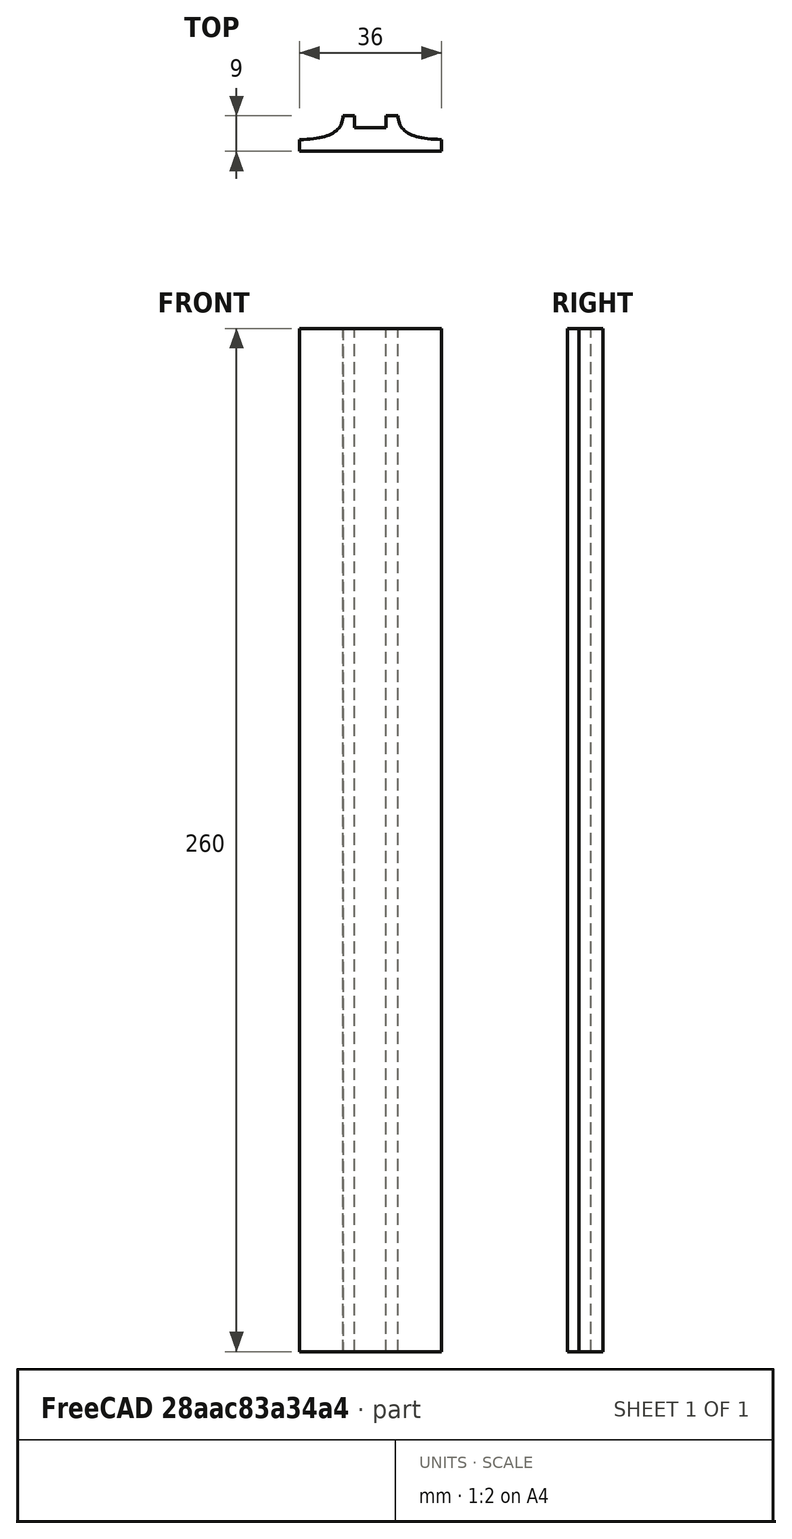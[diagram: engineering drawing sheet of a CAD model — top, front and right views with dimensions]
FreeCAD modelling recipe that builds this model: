
FCSTD DOCUMENT  (FreeCAD 0.19R0.19.2)
Label: laptopStand302.FCStd
License: All rights reserved
LicenseURL: http://en.wikipedia.org/wiki/All_rights_reserved
objects: Sketcher::SketchObject×12, Part::Extrusion×1
note: 13 computed .brp shape members not serialized (recipe doc carries the construction recipe); baked Part::Feature solids carry a one-line shape summary decoded from their .brp

FEATURE [Sketcher::SketchObject] Sketch001  label="legTop"
  FullyConstrained = true
  MapMode = 4
  Placement = pos=(0,0,0) rot=(0.57735,0.57735,0.57735;2.0944rad)
  sketch-geometry (41):
    g0: BSplineCurve PolesCount=3 KnotsCount=2 Degree=2 IsPeriodic=0
    g1: ArcOfCircle CenterX=73.1223 CenterY=-32.291 CenterZ=0 NormalX=0 NormalY=0 NormalZ=1 AngleXU=0 Radius=13 StartAngle=5.92268 EndAngle=9.06428
    g2: ArcOfCircle CenterX=66.7816 CenterY=-49.1439 CenterZ=0 NormalX=0 NormalY=0 NormalZ=1 AngleXU=0 Radius=13 StartAngle=2.78068 EndAngle=5.92131
    g3-g6: Circle x4 (B-spline internal-alignment scaffolding for g7; pole/knot coordinates omitted)
    g7: BSplineCurve PolesCount=4 KnotsCount=2 Degree=3 IsPeriodic=0
    g8: GeomPoint X=28.8094 Y=-19.0875 Z=0
    g9: GeomPoint X=47.0443 Y=-50.4712 Z=0
    g10: Circle CenterX=53.5586 CenterY=-23.2695 CenterZ=0 NormalX=0 NormalY=0 NormalZ=1 AngleXU=0 Radius=3.24518
    g11: LineSegment StartX=17.2232 StartY=-16.0875 StartZ=0 EndX=17.2232 EndY=-19.0875 EndZ=0
    g12: ArcOfCircle CenterX=17.2475 CenterY=-181.166 CenterZ=0 NormalX=0 NormalY=0 NormalZ=1 AngleXU=0 Radius=13 StartAngle=5.92268 EndAngle=7.49361
    g13: ArcOfCircle CenterX=29.5716 CenterY=-148.408 CenterZ=0 NormalX=0 NormalY=0 NormalZ=1 AngleXU=0 Radius=13 StartAngle=4.35228 EndAngle=5.92131
    g14: ArcOfCircle CenterX=35.8967 CenterY=-131.555 CenterZ=0 NormalX=0 NormalY=0 NormalZ=1 AngleXU=0 Radius=13 StartAngle=5.92268 EndAngle=7.49902
    g15: ArcOfCircle CenterX=48.1805 CenterY=-98.7782 CenterZ=0 NormalX=0 NormalY=0 NormalZ=1 AngleXU=0 Radius=13 StartAngle=4.34921 EndAngle=5.92131
    g16: ArcOfCircle CenterX=54.5183 CenterY=-81.9247 CenterZ=0 NormalX=0 NormalY=0 NormalZ=1 AngleXU=0 Radius=13 StartAngle=5.92268 EndAngle=8.70432
    g17: ArcOfCircle CenterX=20.184 CenterY=-217.506 CenterZ=0 NormalX=0 NormalY=0 NormalZ=1 AngleXU=0 Radius=3.81084 StartAngle=1.88136 EndAngle=6.80465
    g18: ArcOfCircle CenterX=36.3663 CenterY=-113.042 CenterZ=0 NormalX=0 NormalY=0 NormalZ=1 AngleXU=0 Radius=3.60555 StartAngle=0.230024 EndAngle=5.3372
    g19: ArcOfCircle CenterX=17.7945 CenterY=-162.686 CenterZ=0 NormalX=0 NormalY=0 NormalZ=1 AngleXU=0 Radius=3.60555 StartAngle=0.230024 EndAngle=5.3372
    g20: ArcOfCircle CenterX=49.8795 CenterY=-62.6074 CenterZ=0 NormalX=0 NormalY=0 NormalZ=1 AngleXU=0 Radius=3.84187 StartAngle=4.46973 EndAngle=9.40343
    g21: LineSegment StartX=48.9563 StartY=-66.3367 StartZ=0 EndX=44.7488 EndY=-73.3482 EndZ=0
    g22: LineSegment StartX=41.085 StartY=-66.3176 StartZ=0 EndX=46.0385 EndY=-62.5254 EndZ=0
    g23: LineSegment StartX=47.0443 StartY=-50.4712 StartZ=0 EndX=41.085 EndY=-66.3176 EndZ=0
    g24: LineSegment StartX=17.2232 StartY=-16.0875 StartZ=0 EndX=117.223 EndY=-16.0875 EndZ=0
    g25: LineSegment StartX=28.8094 StartY=-19.0875 StartZ=0 EndX=17.2232 EndY=-19.0875 EndZ=0
    g26: LineSegment StartX=117.223 StartY=-16.0875 StartZ=0 EndX=117.223 EndY=-19.0875 EndZ=0
    g27: LineSegment StartX=85.2866 StartY=-36.8766 StartZ=0 EndX=78.9396 EndY=-53.7463 EndZ=0
    g28: LineSegment StartX=60.9579 StartY=-27.7053 StartZ=0 EndX=54.6191 EndY=-44.5532 EndZ=0
    g29: LineSegment StartX=23.4884 StartY=-215.608 StartZ=0 EndX=94.6579 EndY=-26.1359 EndZ=0
    g30: LineSegment StartX=19.0195 StartY=-213.878 StartZ=0 EndX=29.4118 EndY=-185.752 EndZ=0
    g31: LineSegment StartX=22.7134 StartY=-166.661 StartZ=0 EndX=21.8316 EndY=-169.001 EndZ=0
    g32: LineSegment StartX=19.9036 StartY=-165.61 StartZ=0 EndX=22.7134 EndY=-166.661 EndZ=0
    g33: LineSegment StartX=21.3051 StartY=-161.864 StartZ=0 EndX=24.1149 EndY=-162.915 EndZ=0
    g34: LineSegment StartX=24.1149 StartY=-162.915 StartZ=0 EndX=24.9906 EndY=-160.574 EndZ=0
    g35: LineSegment StartX=41.7296 StartY=-153.01 StartZ=0 EndX=48.061 EndY=-136.14 EndZ=0
    g36: LineSegment StartX=41.2852 StartY=-117.017 StartZ=0 EndX=40.4148 EndY=-119.365 EndZ=0
    g37: LineSegment StartX=38.4753 StartY=-115.966 StartZ=0 EndX=41.2852 EndY=-117.017 EndZ=0
    g38: LineSegment StartX=39.8769 StartY=-112.22 StartZ=0 EndX=42.6867 EndY=-113.271 EndZ=0
    g39: LineSegment StartX=42.6867 StartY=-113.271 StartZ=0 EndX=43.5622 EndY=-110.93 EndZ=0
    g40: LineSegment StartX=66.6827 StartY=-86.5104 StartZ=0 EndX=60.3386 EndY=-103.381 EndZ=0
  constraints (65):
    c: Block(g0)
    c: Block(g1)
    c: Block(g2)
    c: Weight(g3) = 1
    c: Equal(g3,g4)
    c: Equal(g3,g5)
    c: Equal(g3,g6)
    c: InternalAlignment(g3-g6 -> g7) x4
    c: InternalAlignment(g8,g7)
    c: InternalAlignment(g9,g7)
    c: Block(g10)
    c: Block(g7)
    c: Vertical(g11)
    c: Block(g12)
    c: Block(g13)
    c: Block(g14)
    c: Block(g15)
    c: Block(g16)
    c: Block(g17)
    c: Block(g18)
    c: Block(g19)
    c: Block(g20)
    c: Coincident(g21,g20)
    c: Coincident(g21,g16)
    c: Coincident(g22,g20)
    c: Block(g22)
    c: Coincident(g23,g7)
    c: Coincident(g23,g22)
    c: Coincident(g24,g11)
    c: Horizontal(g24)
    c: Coincident(g25,g7)
    c: Coincident(g25,g11)
    c: Horizontal(g25)
    c: Coincident(g26,g24)
    c: Coincident(g26,g0)
    c: Vertical(g26)
    c: Block(g24)
    c: Coincident(g27,g1)
    c: Coincident(g27,g2)
    c: Coincident(g28,g1)
    c: Coincident(g28,g2)
    c: Coincident(g29,g17)
    c: Coincident(g29,g0)
    c: Coincident(g30,g17)
    c: Coincident(g30,g12)
    c: Coincident(g31,g12)
    c: Coincident(g32,g19)
    c: Coincident(g32,g31)
    c: Block(g31)
    c: Coincident(g33,g19)
    c: Coincident(g34,g33)
    c: Coincident(g34,g13)
    c: Block(g34)
    c: Coincident(g35,g13)
    c: Coincident(g35,g14)
    c: Coincident(g36,g14)
    c: Coincident(g37,g18)
    c: Coincident(g37,g36)
    c: Block(g36)
    c: Coincident(g38,g18)
    c: Coincident(g39,g38)
    c: Coincident(g39,g15)
    c: Block(g39)
    c: Coincident(g40,g16)
    c: Coincident(g40,g15)
FEATURE [Sketcher::SketchObject] Sketch002
  FullyConstrained = true
  sketch-geometry (20):
    g0: LineSegment StartX=-2.77179 StartY=-200.304 StartZ=0 EndX=5.22821 EndY=-200.304 EndZ=0
    g1: LineSegment StartX=5.22821 StartY=-200.304 StartZ=0 EndX=5.22821 EndY=-197.304 EndZ=0
    g2: LineSegment StartX=-2.77179 StartY=-200.304 StartZ=0 EndX=-2.77179 EndY=-197.304 EndZ=0
    g3: LineSegment StartX=5.22821 StartY=-197.304 StartZ=0 EndX=8.22821 EndY=-197.304 EndZ=0
    g4: LineSegment StartX=-2.77179 StartY=-197.304 StartZ=0 EndX=-5.77179 EndY=-197.304 EndZ=0
    g5: LineSegment StartX=19.2282 StartY=-203.304 StartZ=0 EndX=19.2282 EndY=-206.304 EndZ=0
    g6: LineSegment StartX=-16.7718 StartY=-203.304 StartZ=0 EndX=-16.7718 EndY=-206.304 EndZ=0
    g7: LineSegment StartX=-16.7718 StartY=-206.304 StartZ=0 EndX=19.2282 EndY=-206.304 EndZ=0
    g8: Circle CenterX=-16.7718 CenterY=-203.304 CenterZ=0 NormalX=0 NormalY=0 NormalZ=1 AngleXU=0 Radius=1
    g9: Circle CenterX=-5.77179 CenterY=-203.304 CenterZ=0 NormalX=0 NormalY=0 NormalZ=1 AngleXU=0 Radius=1
    g10: Circle CenterX=-5.77179 CenterY=-197.304 CenterZ=0 NormalX=0 NormalY=0 NormalZ=1 AngleXU=0 Radius=1
    g11: BSplineCurve PolesCount=3 KnotsCount=2 Degree=2 IsPeriodic=0
    g12: GeomPoint X=-16.7718 Y=-203.304 Z=0
    g13: GeomPoint X=-5.77179 Y=-197.304 Z=0
    g14: Circle CenterX=19.2282 CenterY=-203.304 CenterZ=0 NormalX=0 NormalY=0 NormalZ=1 AngleXU=0 Radius=1
    g15: Circle CenterX=8.22821 CenterY=-203.304 CenterZ=0 NormalX=0 NormalY=0 NormalZ=1 AngleXU=0 Radius=1
    g16: Circle CenterX=8.22821 CenterY=-197.304 CenterZ=0 NormalX=0 NormalY=0 NormalZ=1 AngleXU=0 Radius=1
    g17: BSplineCurve PolesCount=3 KnotsCount=2 Degree=2 IsPeriodic=0
    g18: GeomPoint X=19.2282 Y=-203.304 Z=0
    g19: GeomPoint X=8.22821 Y=-197.304 Z=0
  constraints (41):
    c: Horizontal(g0)
    c: Distance(g0) = 8
    c: Coincident(g1,g0)
    c: Vertical(g1)
    c: Distance(g1) = 3
    c: Coincident(g2,g0)
    c: Vertical(g2)
    c: Distance(g2) = 3
    c: Coincident(g3,g1)
    c: Horizontal(g3)
    c: Distance(g3) = 3
    c: Coincident(g4,g2)
    c: Horizontal(g4)
    c: Distance(g4) = 3
    c: Vertical(g5)
    c: Vertical(g6)
    c: Coincident(g7,g6)
    c: Coincident(g7,g5)
    c: Weight(g8) = 1
    c: Equal(g8,g9)
    c: Equal(g8,g10)
    c: Coincident(g11,g4)
    c: InternalAlignment(g8,g11)
    c: InternalAlignment(g9,g11)
    c: InternalAlignment(g10,g11)
    c: InternalAlignment(g12,g11)
    c: InternalAlignment(g13,g11)
    c: Coincident(g17,g5)
    c: Weight(g14) = 1
    c: Equal(g14,g15)
    c: Equal(g14,g16)
    c: Coincident(g17,g3)
    c: InternalAlignment(g14,g17)
    c: InternalAlignment(g15,g17)
    c: InternalAlignment(g16,g17)
    c: InternalAlignment(g18,g17)
    c: InternalAlignment(g19,g17)
    c: Block(g7)
    c: Block(g17)
    c: Block(g11)
    c: Block(g6)
FEATURE [Part::Extrusion] Extrude003
  Base = -> Sketch002
  Dir = (0,0,1)
  DirMode = 2
  FaceMakerClass = Part::FaceMakerBullseye
  LengthFwd = 260
  LengthRev = 0
  Solid = true
  Symmetric = false
FEATURE [Sketcher::SketchObject] Sketch003  label="original"
  FullyConstrained = false
  sketch-geometry (469):
    g0: LineSegment StartX=-42.9272 StartY=136.221 StartZ=0 EndX=-42.9272 EndY=-103.779 EndZ=0
    g1: LineSegment StartX=407.073 StartY=136.221 StartZ=0 EndX=407.073 EndY=-103.779 EndZ=0
    g2: ArcOfCircle CenterX=-26.9272 CenterY=-83.7794 CenterZ=0 NormalX=0 NormalY=0 NormalZ=1 AngleXU=0 Radius=8 StartAngle=3.14159 EndAngle=6.28319
    g3: ArcOfCircle CenterX=391.073 CenterY=-83.7794 CenterZ=0 NormalX=0 NormalY=0 NormalZ=1 AngleXU=0 Radius=8 StartAngle=3.14159 EndAngle=6.28319
    g4: Circle CenterX=175.022 CenterY=27.0628 CenterZ=0 NormalX=0 NormalY=0 NormalZ=1 AngleXU=0 Radius=1
    g5: Circle CenterX=179.022 CenterY=24.8665 CenterZ=0 NormalX=0 NormalY=0 NormalZ=1 AngleXU=0 Radius=1
    g6: Circle CenterX=179.022 CenterY=27.0628 CenterZ=0 NormalX=0 NormalY=0 NormalZ=1 AngleXU=0 Radius=1
    g7: BSplineCurve PolesCount=3 KnotsCount=2 Degree=2 IsPeriodic=0
    g8: GeomPoint X=175.022 Y=27.0628 Z=0
    g9: GeomPoint X=179.022 Y=27.0628 Z=0
    g10: Circle CenterX=189.124 CenterY=27.0628 CenterZ=0 NormalX=0 NormalY=0 NormalZ=1 AngleXU=0 Radius=1
    g11: Circle CenterX=185.124 CenterY=24.8665 CenterZ=0 NormalX=0 NormalY=0 NormalZ=1 AngleXU=0 Radius=1
    g12: Circle CenterX=185.124 CenterY=27.0628 CenterZ=0 NormalX=0 NormalY=0 NormalZ=1 AngleXU=0 Radius=1
    g13: BSplineCurve PolesCount=3 KnotsCount=2 Degree=2 IsPeriodic=0
    g14: GeomPoint X=189.124 Y=27.0628 Z=0
    g15: GeomPoint X=185.124 Y=27.0628 Z=0
    g16: Circle CenterX=175.022 CenterY=5.37834 CenterZ=0 NormalX=0 NormalY=0 NormalZ=1 AngleXU=0 Radius=1
    g17: Circle CenterX=179.022 CenterY=7.57463 CenterZ=0 NormalX=0 NormalY=0 NormalZ=1 AngleXU=0 Radius=1
    g18: Circle CenterX=179.022 CenterY=5.34704 CenterZ=0 NormalX=0 NormalY=0 NormalZ=1 AngleXU=0 Radius=1
    g19: BSplineCurve PolesCount=3 KnotsCount=2 Degree=2 IsPeriodic=0
    g20: GeomPoint X=175.022 Y=5.37834 Z=0
    g21: GeomPoint X=179.022 Y=5.34704 Z=0
    g22: Circle CenterX=189.124 CenterY=5.37834 CenterZ=0 NormalX=0 NormalY=0 NormalZ=1 AngleXU=0 Radius=1
    g23: Circle CenterX=185.124 CenterY=7.57463 CenterZ=0 NormalX=0 NormalY=0 NormalZ=1 AngleXU=0 Radius=1
    g24: Circle CenterX=185.124 CenterY=5.34704 CenterZ=0 NormalX=0 NormalY=0 NormalZ=1 AngleXU=0 Radius=1
    g25: BSplineCurve PolesCount=3 KnotsCount=2 Degree=2 IsPeriodic=0
    g26: GeomPoint X=189.124 Y=5.37834 Z=0
    g27: GeomPoint X=185.124 Y=5.34704 Z=0
    g28: Circle CenterX=165.871 CenterY=18.1458 CenterZ=0 NormalX=0 NormalY=0 NormalZ=1 AngleXU=0 Radius=1
    g29: Circle CenterX=169.377 CenterY=16.2206 CenterZ=0 NormalX=0 NormalY=0 NormalZ=1 AngleXU=0 Radius=1
    g30: Circle CenterX=165.871 CenterY=14.2956 CenterZ=0 NormalX=0 NormalY=0 NormalZ=1 AngleXU=0 Radius=1
    g31: BSplineCurve PolesCount=3 KnotsCount=2 Degree=2 IsPeriodic=0
    g32: GeomPoint X=165.871 Y=18.1458 Z=0
    g33: GeomPoint X=165.871 Y=14.2956 Z=0
    g34: Circle CenterX=198.275 CenterY=18.1318 CenterZ=0 NormalX=0 NormalY=0 NormalZ=1 AngleXU=0 Radius=1
    g35: Circle CenterX=194.768 CenterY=16.2206 CenterZ=0 NormalX=0 NormalY=0 NormalZ=1 AngleXU=0 Radius=1
    g36: Circle CenterX=198.264 CenterY=14.2963 CenterZ=0 NormalX=0 NormalY=0 NormalZ=1 AngleXU=0 Radius=1
    g37: BSplineCurve PolesCount=3 KnotsCount=2 Degree=2 IsPeriodic=0
    g38: GeomPoint X=198.275 Y=18.1318 Z=0
    g39: GeomPoint X=198.264 Y=14.2963 Z=0
    g40: LineSegment StartX=407.073 StartY=-103.779 StartZ=0 EndX=-42.9272 EndY=-103.779 EndZ=0
    g41: Circle CenterX=125.607 CenterY=54.1951 CenterZ=0 NormalX=0 NormalY=0 NormalZ=1 AngleXU=0 Radius=1
    g42: Circle CenterX=139.632 CenterY=46.4944 CenterZ=0 NormalX=0 NormalY=0 NormalZ=1 AngleXU=0 Radius=1
    g43: Circle CenterX=127.326 CenterY=56.7187 CenterZ=0 NormalX=0 NormalY=0 NormalZ=1 AngleXU=0 Radius=1
    g44: BSplineCurve PolesCount=3 KnotsCount=2 Degree=2 IsPeriodic=0
    g45: GeomPoint X=125.607 Y=54.1951 Z=0
    g46: GeomPoint X=127.326 Y=56.7187 Z=0
    g47: Circle CenterX=236.824 CenterY=56.7187 CenterZ=0 NormalX=0 NormalY=0 NormalZ=1 AngleXU=0 Radius=1
    g48: Circle CenterX=224.513 CenterY=46.4944 CenterZ=0 NormalX=0 NormalY=0 NormalZ=1 AngleXU=0 Radius=1
    g49: Circle CenterX=238.538 CenterY=54.1951 CenterZ=0 NormalX=0 NormalY=0 NormalZ=1 AngleXU=0 Radius=1
    g50: BSplineCurve PolesCount=3 KnotsCount=2 Degree=2 IsPeriodic=0
    g51: GeomPoint X=236.824 Y=56.7187 Z=0
    g52: GeomPoint X=238.538 Y=54.1951 Z=0
    g53: Circle CenterX=238.538 CenterY=-21.7516 CenterZ=0 NormalX=0 NormalY=0 NormalZ=1 AngleXU=0 Radius=1
    g54: Circle CenterX=224.513 CenterY=-14.0532 CenterZ=0 NormalX=0 NormalY=0 NormalZ=1 AngleXU=0 Radius=1
    g55: Circle CenterX=236.584 CenterY=-24.2775 CenterZ=0 NormalX=0 NormalY=0 NormalZ=1 AngleXU=0 Radius=1
    g56: BSplineCurve PolesCount=3 KnotsCount=2 Degree=2 IsPeriodic=0
    g57: GeomPoint X=238.538 Y=-21.7516 Z=0
    g58: GeomPoint X=236.584 Y=-24.2775 Z=0
    g59: Circle CenterX=125.607 CenterY=-21.7539 CenterZ=0 NormalX=0 NormalY=0 NormalZ=1 AngleXU=0 Radius=1
    g60: Circle CenterX=139.632 CenterY=-14.0532 CenterZ=0 NormalX=0 NormalY=0 NormalZ=1 AngleXU=0 Radius=1
    g61: Circle CenterX=127.325 CenterY=-24.2775 CenterZ=0 NormalX=0 NormalY=0 NormalZ=1 AngleXU=0 Radius=1
    g62: BSplineCurve PolesCount=3 KnotsCount=2 Degree=2 IsPeriodic=0
    g63: GeomPoint X=125.607 Y=-21.7539 Z=0
    g64: GeomPoint X=127.325 Y=-24.2775 Z=0
    g65: Circle CenterX=302.996 CenterY=111.695 CenterZ=0 NormalX=0 NormalY=0 NormalZ=1 AngleXU=0 Radius=1
    g66: Circle CenterX=306.073 CenterY=114.251 CenterZ=0 NormalX=0 NormalY=0 NormalZ=1 AngleXU=0 Radius=1
    g67: Circle CenterX=306.073 CenterY=110.251 CenterZ=0 NormalX=0 NormalY=0 NormalZ=1 AngleXU=0 Radius=1
    g68: BSplineCurve PolesCount=3 KnotsCount=2 Degree=2 IsPeriodic=0
    g69: GeomPoint X=302.996 Y=111.695 Z=0
    g70: GeomPoint X=306.073 Y=110.251 Z=0
    g71: Circle CenterX=306.073 CenterY=95.2763 CenterZ=0 NormalX=0 NormalY=0 NormalZ=1 AngleXU=0 Radius=1
    g72: Circle CenterX=306.073 CenterY=91.2763 CenterZ=0 NormalX=0 NormalY=0 NormalZ=1 AngleXU=0 Radius=1
    g73: Circle CenterX=302.567 CenterY=89.3511 CenterZ=0 NormalX=0 NormalY=0 NormalZ=1 AngleXU=0 Radius=1
    g74: BSplineCurve PolesCount=3 KnotsCount=2 Degree=2 IsPeriodic=0
    g75: GeomPoint X=306.073 Y=95.2763 Z=0
    g76: GeomPoint X=302.567 Y=89.3511 Z=0
    g77: LineSegment StartX=306.073 StartY=110.251 StartZ=0 EndX=306.073 EndY=95.2763 EndZ=0
    g78: LineSegment StartX=302.996 StartY=111.695 StartZ=0 EndX=236.824 EndY=56.7187 EndZ=0
    g79: LineSegment StartX=238.538 StartY=54.1951 StartZ=0 EndX=302.567 EndY=89.3511 EndZ=0
    g80: Circle CenterX=61.1496 CenterY=111.695 CenterZ=0 NormalX=0 NormalY=0 NormalZ=1 AngleXU=0 Radius=1
    g81: Circle CenterX=58.0728 CenterY=114.251 CenterZ=0 NormalX=0 NormalY=0 NormalZ=1 AngleXU=0 Radius=1
    g82: Circle CenterX=58.0728 CenterY=110.251 CenterZ=0 NormalX=0 NormalY=0 NormalZ=1 AngleXU=0 Radius=1
    g83: BSplineCurve PolesCount=3 KnotsCount=2 Degree=2 IsPeriodic=0
    g84: GeomPoint X=61.1496 Y=111.695 Z=0
    g85: GeomPoint X=58.0728 Y=110.251 Z=0
    g86: Circle CenterX=61.5791 CenterY=89.3511 CenterZ=0 NormalX=0 NormalY=0 NormalZ=1 AngleXU=0 Radius=1
    g87: Circle CenterX=58.0728 CenterY=91.2763 CenterZ=0 NormalX=0 NormalY=0 NormalZ=1 AngleXU=0 Radius=1
    g88: Circle CenterX=58.0728 CenterY=95.2763 CenterZ=0 NormalX=0 NormalY=0 NormalZ=1 AngleXU=0 Radius=1
    g89: BSplineCurve PolesCount=3 KnotsCount=2 Degree=2 IsPeriodic=0
    g90: GeomPoint X=61.5791 Y=89.3511 Z=0
    g91: GeomPoint X=58.0728 Y=95.2763 Z=0
    g92: LineSegment StartX=58.0728 StartY=110.251 StartZ=0 EndX=58.0728 EndY=95.2763 EndZ=0
    g93: LineSegment StartX=61.1496 StartY=111.695 StartZ=0 EndX=127.326 EndY=56.7187 EndZ=0
    g94: LineSegment StartX=125.607 StartY=54.1951 StartZ=0 EndX=61.5791 EndY=89.3511 EndZ=0
    g95: Circle CenterX=61.5791 CenterY=-56.9099 CenterZ=0 NormalX=0 NormalY=0 NormalZ=1 AngleXU=0 Radius=1
    g96: Circle CenterX=58.0728 CenterY=-58.8351 CenterZ=0 NormalX=0 NormalY=0 NormalZ=1 AngleXU=0 Radius=1
    g97: Circle CenterX=58.0728 CenterY=-62.8351 CenterZ=0 NormalX=0 NormalY=0 NormalZ=1 AngleXU=0 Radius=1
    g98: BSplineCurve PolesCount=3 KnotsCount=2 Degree=2 IsPeriodic=0
    g99: GeomPoint X=61.5791 Y=-56.9099 Z=0
    g100: GeomPoint X=58.0728 Y=-62.8351 Z=0
    g101: Circle CenterX=58.0728 CenterY=-77.8102 CenterZ=0 NormalX=0 NormalY=0 NormalZ=1 AngleXU=0 Radius=1
    g102: Circle CenterX=58.0728 CenterY=-81.8102 CenterZ=0 NormalX=0 NormalY=0 NormalZ=1 AngleXU=0 Radius=1
    g103: Circle CenterX=61.1496 CenterY=-79.2541 CenterZ=0 NormalX=0 NormalY=0 NormalZ=1 AngleXU=0 Radius=1
    g104: BSplineCurve PolesCount=3 KnotsCount=2 Degree=2 IsPeriodic=0
    g105: GeomPoint X=58.0728 Y=-77.8102 Z=0
    g106: GeomPoint X=61.1496 Y=-79.2541 Z=0
    g107: LineSegment StartX=58.0728 StartY=-62.8351 StartZ=0 EndX=58.0728 EndY=-77.8102 EndZ=0
    g108: LineSegment StartX=61.1496 StartY=-79.2541 StartZ=0 EndX=127.325 EndY=-24.2775 EndZ=0
    g109: LineSegment StartX=125.607 StartY=-21.7539 StartZ=0 EndX=61.5791 EndY=-56.9099 EndZ=0
    g110: Circle CenterX=302.567 CenterY=-56.9099 CenterZ=0 NormalX=0 NormalY=0 NormalZ=1 AngleXU=0 Radius=1
    g111: Circle CenterX=306.073 CenterY=-58.8351 CenterZ=0 NormalX=0 NormalY=0 NormalZ=1 AngleXU=0 Radius=1
    g112: Circle CenterX=306.073 CenterY=-62.8351 CenterZ=0 NormalX=0 NormalY=0 NormalZ=1 AngleXU=0 Radius=1
    g113: BSplineCurve PolesCount=3 KnotsCount=2 Degree=2 IsPeriodic=0
    g114: GeomPoint X=302.567 Y=-56.9099 Z=0
    g115: GeomPoint X=306.073 Y=-62.8351 Z=0
    g116: Circle CenterX=302.996 CenterY=-79.2541 CenterZ=0 NormalX=0 NormalY=0 NormalZ=1 AngleXU=0 Radius=1
    g117: Circle CenterX=306.073 CenterY=-81.8102 CenterZ=0 NormalX=0 NormalY=0 NormalZ=1 AngleXU=0 Radius=1
    g118: Circle CenterX=306.073 CenterY=-77.8102 CenterZ=0 NormalX=0 NormalY=0 NormalZ=1 AngleXU=0 Radius=1
    g119: BSplineCurve PolesCount=3 KnotsCount=2 Degree=2 IsPeriodic=0
    g120: GeomPoint X=302.996 Y=-79.2541 Z=0
    g121: GeomPoint X=306.073 Y=-77.8102 Z=0
    g122: LineSegment StartX=306.073 StartY=-62.8351 StartZ=0 EndX=306.073 EndY=-77.8102 EndZ=0
    g123: LineSegment StartX=302.996 StartY=-79.2541 StartZ=0 EndX=236.584 EndY=-24.2775 EndZ=0
    g124: LineSegment StartX=238.538 StartY=-21.7516 StartZ=0 EndX=302.567 EndY=-56.9099 EndZ=0
    g125: Circle CenterX=61.6457 CenterY=-88.8112 CenterZ=0 NormalX=0 NormalY=0 NormalZ=1 AngleXU=0 Radius=1
    g126: Circle CenterX=58.0728 CenterY=-91.7794 CenterZ=0 NormalX=0 NormalY=0 NormalZ=1 AngleXU=0 Radius=1
    g127: Circle CenterX=63.9135 CenterY=-91.7791 CenterZ=0 NormalX=0 NormalY=0 NormalZ=1 AngleXU=0 Radius=1
    g128: BSplineCurve PolesCount=3 KnotsCount=2 Degree=2 IsPeriodic=0
    g129: GeomPoint X=61.6457 Y=-88.8112 Z=0
    g130: GeomPoint X=63.9135 Y=-91.7791 Z=0
    g131: Circle CenterX=179.022 CenterY=-85.8163 CenterZ=0 NormalX=0 NormalY=0 NormalZ=1 AngleXU=0 Radius=1
    g132: Circle CenterX=179.022 CenterY=-91.7794 CenterZ=0 NormalX=0 NormalY=0 NormalZ=1 AngleXU=0 Radius=1
    g133: Circle CenterX=171.895 CenterY=-91.7791 CenterZ=0 NormalX=0 NormalY=0 NormalZ=1 AngleXU=0 Radius=1
    g134: BSplineCurve PolesCount=3 KnotsCount=2 Degree=2 IsPeriodic=0
    g135: GeomPoint X=179.022 Y=-85.8163 Z=0
    g136: GeomPoint X=171.895 Y=-91.7791 Z=0
    g137: Circle CenterX=185.124 CenterY=-86.2028 CenterZ=0 NormalX=0 NormalY=0 NormalZ=1 AngleXU=0 Radius=1
    g138: Circle CenterX=185.124 CenterY=-91.7794 CenterZ=0 NormalX=0 NormalY=0 NormalZ=1 AngleXU=0 Radius=1
    g139: Circle CenterX=191.747 CenterY=-91.7794 CenterZ=0 NormalX=0 NormalY=0 NormalZ=1 AngleXU=0 Radius=1
    g140: BSplineCurve PolesCount=3 KnotsCount=2 Degree=2 IsPeriodic=0
    g141: GeomPoint X=185.124 Y=-86.2028 Z=0
    g142: GeomPoint X=191.747 Y=-91.7794 Z=0
    g143: Circle CenterX=299.888 CenterY=-86.6413 CenterZ=0 NormalX=0 NormalY=0 NormalZ=1 AngleXU=0 Radius=1
    g144: Circle CenterX=306.073 CenterY=-91.7794 CenterZ=0 NormalX=0 NormalY=0 NormalZ=1 AngleXU=0 Radius=1
    g145: Circle CenterX=298.776 CenterY=-91.7794 CenterZ=0 NormalX=0 NormalY=0 NormalZ=1 AngleXU=0 Radius=1
    g146: BSplineCurve PolesCount=3 KnotsCount=2 Degree=2 IsPeriodic=0
    g147: GeomPoint X=299.888 Y=-86.6413 Z=0
    g148: GeomPoint X=298.776 Y=-91.7794 Z=0
    g149: LineSegment StartX=189.124 StartY=5.37834 StartZ=0 EndX=299.888 EndY=-86.6413 EndZ=0
    g150: LineSegment StartX=298.776 StartY=-91.7794 StartZ=0 EndX=191.747 EndY=-91.7794 EndZ=0
    g151: LineSegment StartX=185.124 StartY=-86.2028 StartZ=0 EndX=185.124 EndY=5.34704 EndZ=0
    g152: LineSegment StartX=179.022 StartY=5.34704 StartZ=0 EndX=179.022 EndY=-85.8163 EndZ=0
    g153: LineSegment StartX=171.895 StartY=-91.7791 StartZ=0 EndX=63.9135 EndY=-91.7791 EndZ=0
    g154: LineSegment StartX=61.6457 StartY=-88.8112 StartZ=0 EndX=175.022 EndY=5.37834 EndZ=0
    g155: Circle CenterX=302.073 CenterY=124.221 CenterZ=0 NormalX=0 NormalY=0 NormalZ=1 AngleXU=0 Radius=1
    g156: Circle CenterX=306.073 CenterY=124.221 CenterZ=0 NormalX=0 NormalY=0 NormalZ=1 AngleXU=0 Radius=1
    g157: Circle CenterX=302.996 CenterY=121.665 CenterZ=0 NormalX=0 NormalY=0 NormalZ=1 AngleXU=0 Radius=1
    g158: BSplineCurve PolesCount=3 KnotsCount=2 Degree=2 IsPeriodic=0
    g159: GeomPoint X=302.073 Y=124.221 Z=0
    g160: GeomPoint X=302.996 Y=121.665 Z=0
    g161: Circle CenterX=189.124 CenterY=124.221 CenterZ=0 NormalX=0 NormalY=0 NormalZ=1 AngleXU=0 Radius=1
    g162: Circle CenterX=185.124 CenterY=124.221 CenterZ=0 NormalX=0 NormalY=0 NormalZ=1 AngleXU=0 Radius=1
    g163: Circle CenterX=185.124 CenterY=120.221 CenterZ=0 NormalX=0 NormalY=0 NormalZ=1 AngleXU=0 Radius=1
    g164: BSplineCurve PolesCount=3 KnotsCount=2 Degree=2 IsPeriodic=0
    g165: GeomPoint X=189.124 Y=124.221 Z=0
    g166: GeomPoint X=185.124 Y=120.221 Z=0
    g167: Circle CenterX=175.022 CenterY=124.221 CenterZ=0 NormalX=0 NormalY=0 NormalZ=1 AngleXU=0 Radius=1
    g168: Circle CenterX=179.022 CenterY=124.221 CenterZ=0 NormalX=0 NormalY=0 NormalZ=1 AngleXU=0 Radius=1
    g169: Circle CenterX=179.022 CenterY=120.221 CenterZ=0 NormalX=0 NormalY=0 NormalZ=1 AngleXU=0 Radius=1
    g170: BSplineCurve PolesCount=3 KnotsCount=2 Degree=2 IsPeriodic=0
    g171: GeomPoint X=175.022 Y=124.221 Z=0
    g172: GeomPoint X=179.022 Y=120.221 Z=0
    g173: Circle CenterX=62.0728 CenterY=124.221 CenterZ=0 NormalX=0 NormalY=0 NormalZ=1 AngleXU=0 Radius=1
    g174: Circle CenterX=58.0728 CenterY=124.221 CenterZ=0 NormalX=0 NormalY=0 NormalZ=1 AngleXU=0 Radius=1
    g175: Circle CenterX=61.1496 CenterY=121.665 CenterZ=0 NormalX=0 NormalY=0 NormalZ=1 AngleXU=0 Radius=1
    g176: BSplineCurve PolesCount=3 KnotsCount=2 Degree=2 IsPeriodic=0
    g177: GeomPoint X=62.0728 Y=124.221 Z=0
    g178: GeomPoint X=61.1496 Y=121.665 Z=0
    g179: LineSegment StartX=179.022 StartY=120.221 StartZ=0 EndX=179.022 EndY=27.0628 EndZ=0
    g180: LineSegment StartX=185.124 StartY=27.0628 StartZ=0 EndX=185.124 EndY=120.221 EndZ=0
    g181: LineSegment StartX=302.996 StartY=121.665 StartZ=0 EndX=189.124 EndY=27.0628 EndZ=0
    g182: LineSegment StartX=175.022 StartY=27.0628 StartZ=0 EndX=61.1496 EndY=121.665 EndZ=0
    g183: Circle CenterX=61.5791 CenterY=75.4095 CenterZ=0 NormalX=0 NormalY=0 NormalZ=1 AngleXU=0 Radius=1
    g184: Circle CenterX=58.0728 CenterY=77.3346 CenterZ=0 NormalX=0 NormalY=0 NormalZ=1 AngleXU=0 Radius=1
    g185: Circle CenterX=58.0728 CenterY=73.3346 CenterZ=0 NormalX=0 NormalY=0 NormalZ=1 AngleXU=0 Radius=1
    g186: BSplineCurve PolesCount=3 KnotsCount=2 Degree=2 IsPeriodic=0
    g187: GeomPoint X=61.5791 Y=75.4095 Z=0
    g188: GeomPoint X=58.0728 Y=73.3346 Z=0
    g189: Circle CenterX=58.0728 CenterY=-40.8935 CenterZ=0 NormalX=0 NormalY=0 NormalZ=1 AngleXU=0 Radius=1
    g190: Circle CenterX=58.0728 CenterY=-44.8935 CenterZ=0 NormalX=0 NormalY=0 NormalZ=1 AngleXU=0 Radius=1
    g191: Circle CenterX=61.5791 CenterY=-42.9683 CenterZ=0 NormalX=0 NormalY=0 NormalZ=1 AngleXU=0 Radius=1
    g192: BSplineCurve PolesCount=3 KnotsCount=2 Degree=2 IsPeriodic=0
    g193: GeomPoint X=58.0728 Y=-40.8935 Z=0
    g194: GeomPoint X=61.5791 Y=-42.9683 Z=0
    g195: LineSegment StartX=61.5791 StartY=-42.9683 StartZ=0 EndX=165.871 EndY=14.2956 EndZ=0
    g196: LineSegment StartX=165.871 StartY=18.1458 StartZ=0 EndX=61.5791 EndY=75.4095 EndZ=0
    g197: LineSegment StartX=58.0728 StartY=73.3346 StartZ=0 EndX=58.0728 EndY=-40.8935 EndZ=0
    g198: Circle CenterX=302.567 CenterY=-42.9683 CenterZ=0 NormalX=0 NormalY=0 NormalZ=1 AngleXU=0 Radius=1
    g199: Circle CenterX=306.073 CenterY=-44.8935 CenterZ=0 NormalX=0 NormalY=0 NormalZ=1 AngleXU=0 Radius=1
    g200: Circle CenterX=306.073 CenterY=-40.8935 CenterZ=0 NormalX=0 NormalY=0 NormalZ=1 AngleXU=0 Radius=1
    g201: BSplineCurve PolesCount=3 KnotsCount=2 Degree=2 IsPeriodic=0
    g202: GeomPoint X=302.567 Y=-42.9683 Z=0
    g203: GeomPoint X=306.073 Y=-40.8935 Z=0
    g204: Circle CenterX=306.073 CenterY=73.3346 CenterZ=0 NormalX=0 NormalY=0 NormalZ=1 AngleXU=0 Radius=1
    g205: Circle CenterX=306.073 CenterY=77.3346 CenterZ=0 NormalX=0 NormalY=0 NormalZ=1 AngleXU=0 Radius=1
    g206: Circle CenterX=302.535 CenterY=75.4095 CenterZ=0 NormalX=0 NormalY=0 NormalZ=1 AngleXU=0 Radius=1
    g207: BSplineCurve PolesCount=3 KnotsCount=2 Degree=2 IsPeriodic=0
    g208: GeomPoint X=306.073 Y=73.3346 Z=0
    g209: GeomPoint X=302.535 Y=75.4095 Z=0
    g210: LineSegment StartX=302.567 StartY=-42.9683 StartZ=0 EndX=198.264 EndY=14.2963 EndZ=0
    g211: LineSegment StartX=198.275 StartY=18.1318 StartZ=0 EndX=302.535 EndY=75.4095 EndZ=0
    g212: LineSegment StartX=306.073 StartY=73.3346 StartZ=0 EndX=306.073 EndY=-40.8935 EndZ=0
    g213: LineSegment StartX=322.073 StartY=105.865 StartZ=0 EndX=328.643 EndY=105.865 EndZ=0
    g214: LineSegment StartX=318.073 StartY=120.221 StartZ=0 EndX=318.073 EndY=109.865 EndZ=0
    g215: LineSegment StartX=336.157 StartY=107.779 StartZ=0 EndX=362.567 EndY=122.294 EndZ=0
    g216: Circle CenterX=362.073 CenterY=124.221 CenterZ=0 NormalX=0 NormalY=0 NormalZ=1 AngleXU=0 Radius=1
    g217: Circle CenterX=366.073 CenterY=124.221 CenterZ=0 NormalX=0 NormalY=0 NormalZ=1 AngleXU=0 Radius=1
    g218: Circle CenterX=362.567 CenterY=122.294 CenterZ=0 NormalX=0 NormalY=0 NormalZ=1 AngleXU=0 Radius=1
    g219: BSplineCurve PolesCount=3 KnotsCount=2 Degree=2 IsPeriodic=0
    g220: GeomPoint X=362.073 Y=124.221 Z=0
    g221: GeomPoint X=362.567 Y=122.294 Z=0
    g222: Circle CenterX=322.073 CenterY=124.221 CenterZ=0 NormalX=0 NormalY=0 NormalZ=1 AngleXU=0 Radius=1
    g223: Circle CenterX=318.073 CenterY=124.221 CenterZ=0 NormalX=0 NormalY=0 NormalZ=1 AngleXU=0 Radius=1
    g224: Circle CenterX=318.073 CenterY=120.221 CenterZ=0 NormalX=0 NormalY=0 NormalZ=1 AngleXU=0 Radius=1
    g225: BSplineCurve PolesCount=3 KnotsCount=2 Degree=2 IsPeriodic=0
    g226: GeomPoint X=322.073 Y=124.221 Z=0
    g227: GeomPoint X=318.073 Y=120.221 Z=0
    g228: Circle CenterX=322.073 CenterY=105.865 CenterZ=0 NormalX=0 NormalY=0 NormalZ=1 AngleXU=0 Radius=1
    g229: Circle CenterX=318.073 CenterY=105.865 CenterZ=0 NormalX=0 NormalY=0 NormalZ=1 AngleXU=0 Radius=1
    g230: Circle CenterX=318.073 CenterY=109.865 CenterZ=0 NormalX=0 NormalY=0 NormalZ=1 AngleXU=0 Radius=1
    g231: BSplineCurve PolesCount=3 KnotsCount=2 Degree=2 IsPeriodic=0
    g232: GeomPoint X=322.073 Y=105.865 Z=0
    g233: GeomPoint X=318.073 Y=109.865 Z=0
    g234: Circle CenterX=336.157 CenterY=107.779 CenterZ=0 NormalX=0 NormalY=0 NormalZ=1 AngleXU=0 Radius=1
    g235: Circle CenterX=332.651 CenterY=105.853 CenterZ=0 NormalX=0 NormalY=0 NormalZ=1 AngleXU=0 Radius=1
    g236: Circle CenterX=328.643 CenterY=105.865 CenterZ=0 NormalX=0 NormalY=0 NormalZ=1 AngleXU=0 Radius=1
    g237: BSplineCurve PolesCount=3 KnotsCount=2 Degree=2 IsPeriodic=0
    g238: GeomPoint X=336.157 Y=107.779 Z=0
    g239: GeomPoint X=328.643 Y=105.865 Z=0
    g240: LineSegment StartX=322.073 StartY=124.221 StartZ=0 EndX=362.073 EndY=124.221 EndZ=0
    g241: Circle CenterX=371.567 CenterY=-80.8644 CenterZ=0 NormalX=0 NormalY=0 NormalZ=1 AngleXU=0 Radius=1
    g242: Circle CenterX=375.073 CenterY=-82.7896 CenterZ=0 NormalX=0 NormalY=0 NormalZ=1 AngleXU=0 Radius=1
    g243: Circle CenterX=375.073 CenterY=-78.7896 CenterZ=0 NormalX=0 NormalY=0 NormalZ=1 AngleXU=0 Radius=1
    g244: BSplineCurve PolesCount=3 KnotsCount=2 Degree=2 IsPeriodic=0
    g245: GeomPoint X=371.567 Y=-80.8644 Z=0
    g246: GeomPoint X=375.073 Y=-78.7896 Z=0
    g247: Circle CenterX=321.579 CenterY=-53.4075 CenterZ=0 NormalX=0 NormalY=0 NormalZ=1 AngleXU=0 Radius=1
    g248: Circle CenterX=318.073 CenterY=-51.4823 CenterZ=0 NormalX=0 NormalY=0 NormalZ=1 AngleXU=0 Radius=1
    g249: Circle CenterX=318.073 CenterY=-47.4805 CenterZ=0 NormalX=0 NormalY=0 NormalZ=1 AngleXU=0 Radius=1
    g250: BSplineCurve PolesCount=3 KnotsCount=2 Degree=2 IsPeriodic=0
    g251: GeomPoint X=321.579 Y=-53.4075 Z=0
    g252: GeomPoint X=318.073 Y=-47.4805 Z=0
    g253: LineSegment StartX=371.567 StartY=-80.8644 StartZ=0 EndX=321.579 EndY=-53.4075 EndZ=0
    g254: Circle CenterX=321.579 CenterY=-67.3492 CenterZ=0 NormalX=0 NormalY=0 NormalZ=1 AngleXU=0 Radius=1
    g255: Circle CenterX=318.073 CenterY=-65.424 CenterZ=0 NormalX=0 NormalY=0 NormalZ=1 AngleXU=0 Radius=1
    g256: Circle CenterX=318.073 CenterY=-69.424 CenterZ=0 NormalX=0 NormalY=0 NormalZ=1 AngleXU=0 Radius=1
    g257: BSplineCurve PolesCount=3 KnotsCount=2 Degree=2 IsPeriodic=0
    g258: GeomPoint X=321.579 Y=-67.3492 Z=0
    g259: GeomPoint X=318.073 Y=-69.424 Z=0
    g260: Circle CenterX=362.567 CenterY=-89.8542 CenterZ=0 NormalX=0 NormalY=0 NormalZ=1 AngleXU=0 Radius=1
    g261: Circle CenterX=366.073 CenterY=-91.7794 CenterZ=0 NormalX=0 NormalY=0 NormalZ=1 AngleXU=0 Radius=1
    g262: Circle CenterX=362.073 CenterY=-91.7794 CenterZ=0 NormalX=0 NormalY=0 NormalZ=1 AngleXU=0 Radius=1
    g263: BSplineCurve PolesCount=3 KnotsCount=2 Degree=2 IsPeriodic=0
    g264: GeomPoint X=362.567 Y=-89.8542 Z=0
    g265: GeomPoint X=362.073 Y=-91.7794 Z=0
    g266: Circle CenterX=322.073 CenterY=-91.7794 CenterZ=0 NormalX=0 NormalY=0 NormalZ=1 AngleXU=0 Radius=1
    g267: Circle CenterX=318.073 CenterY=-91.7794 CenterZ=0 NormalX=0 NormalY=0 NormalZ=1 AngleXU=0 Radius=1
    g268: Circle CenterX=318.073 CenterY=-87.7794 CenterZ=0 NormalX=0 NormalY=0 NormalZ=1 AngleXU=0 Radius=1
    g269: BSplineCurve PolesCount=3 KnotsCount=2 Degree=2 IsPeriodic=0
    g270: GeomPoint X=322.073 Y=-91.7794 Z=0
    g271: GeomPoint X=318.073 Y=-87.7794 Z=0
    g272: LineSegment StartX=362.567 StartY=-89.8542 StartZ=0 EndX=321.579 EndY=-67.3492 EndZ=0
    g273: LineSegment StartX=318.073 StartY=-69.424 StartZ=0 EndX=318.073 EndY=-87.7794 EndZ=0
    g274: LineSegment StartX=322.073 StartY=-91.7794 StartZ=0 EndX=362.073 EndY=-91.7794 EndZ=0
    g275: Circle CenterX=2.07281 CenterY=124.221 CenterZ=0 NormalX=0 NormalY=0 NormalZ=1 AngleXU=0 Radius=1
    g276: Circle CenterX=1.57905 CenterY=122.295 CenterZ=0 NormalX=0 NormalY=0 NormalZ=1 AngleXU=0 Radius=1
    g277: BSplineCurve PolesCount=3 KnotsCount=2 Degree=2 IsPeriodic=0
    g278: GeomPoint X=2.07281 Y=124.221 Z=0
    g279: GeomPoint X=1.57905 Y=122.295 Z=0
    g280: Circle CenterX=42.0728 CenterY=124.221 CenterZ=0 NormalX=0 NormalY=0 NormalZ=1 AngleXU=0 Radius=1
    g281: Circle CenterX=46.0728 CenterY=124.221 CenterZ=0 NormalX=0 NormalY=0 NormalZ=1 AngleXU=0 Radius=1
    g282: Circle CenterX=46.0728 CenterY=120.221 CenterZ=0 NormalX=0 NormalY=0 NormalZ=1 AngleXU=0 Radius=1
    g283: BSplineCurve PolesCount=3 KnotsCount=2 Degree=2 IsPeriodic=0
    g284: GeomPoint X=42.0728 Y=124.221 Z=0
    g285: GeomPoint X=46.0728 Y=120.221 Z=0
    g286: Circle CenterX=46.0728 CenterY=109.865 CenterZ=0 NormalX=0 NormalY=0 NormalZ=1 AngleXU=0 Radius=1
    g287: Circle CenterX=46.0728 CenterY=105.865 CenterZ=0 NormalX=0 NormalY=0 NormalZ=1 AngleXU=0 Radius=1
    g288: Circle CenterX=42.0728 CenterY=105.865 CenterZ=0 NormalX=0 NormalY=0 NormalZ=1 AngleXU=0 Radius=1
    g289: BSplineCurve PolesCount=3 KnotsCount=2 Degree=2 IsPeriodic=0
    g290: GeomPoint X=46.0728 Y=109.865 Z=0
    g291: GeomPoint X=42.0728 Y=105.865 Z=0
    g292: Circle CenterX=35.5028 CenterY=105.865 CenterZ=0 NormalX=0 NormalY=0 NormalZ=1 AngleXU=0 Radius=1
    g293: Circle CenterX=31.5028 CenterY=105.865 CenterZ=0 NormalX=0 NormalY=0 NormalZ=1 AngleXU=0 Radius=1
    g294: Circle CenterX=27.9965 CenterY=107.79 CenterZ=0 NormalX=0 NormalY=0 NormalZ=1 AngleXU=0 Radius=1
    g295: BSplineCurve PolesCount=3 KnotsCount=2 Degree=2 IsPeriodic=0
    g296: GeomPoint X=35.5028 Y=105.865 Z=0
    g297: GeomPoint X=27.9965 Y=107.79 Z=0
    g298: LineSegment StartX=2.07281 StartY=124.221 StartZ=0 EndX=42.0728 EndY=124.221 EndZ=0
    g299: LineSegment StartX=46.0728 StartY=120.221 StartZ=0 EndX=46.0728 EndY=109.865 EndZ=0
    g300: LineSegment StartX=42.0728 StartY=105.865 StartZ=0 EndX=35.5028 EndY=105.865 EndZ=0
    g301: LineSegment StartX=27.9965 StartY=107.79 StartZ=0 EndX=1.57905 EndY=122.295 EndZ=0
    g302: Circle CenterX=42.5666 CenterY=-67.3492 CenterZ=0 NormalX=0 NormalY=0 NormalZ=1 AngleXU=0 Radius=1
    g303: Circle CenterX=46.0728 CenterY=-65.424 CenterZ=0 NormalX=0 NormalY=0 NormalZ=1 AngleXU=0 Radius=1
    g304: Circle CenterX=46.0728 CenterY=-69.424 CenterZ=0 NormalX=0 NormalY=0 NormalZ=1 AngleXU=0 Radius=1
    g305: BSplineCurve PolesCount=3 KnotsCount=2 Degree=2 IsPeriodic=0
    g306: GeomPoint X=42.5666 Y=-67.3492 Z=0
    g307: GeomPoint X=46.0728 Y=-69.424 Z=0
    g308: Circle CenterX=46.0728 CenterY=-87.7794 CenterZ=0 NormalX=0 NormalY=0 NormalZ=1 AngleXU=0 Radius=1
    g309: Circle CenterX=46.0728 CenterY=-91.7794 CenterZ=0 NormalX=0 NormalY=0 NormalZ=1 AngleXU=0 Radius=1
    g310: Circle CenterX=42.0728 CenterY=-91.7794 CenterZ=0 NormalX=0 NormalY=0 NormalZ=1 AngleXU=0 Radius=1
    g311: BSplineCurve PolesCount=3 KnotsCount=2 Degree=2 IsPeriodic=0
    g312: GeomPoint X=46.0728 Y=-87.7794 Z=0
    g313: GeomPoint X=42.0728 Y=-91.7794 Z=0
    g314: Circle CenterX=2.07281 CenterY=-91.7794 CenterZ=0 NormalX=0 NormalY=0 NormalZ=1 AngleXU=0 Radius=1
    g315: Circle CenterX=-1.92719 CenterY=-91.7794 CenterZ=0 NormalX=0 NormalY=0 NormalZ=1 AngleXU=0 Radius=1
    g316: Circle CenterX=1.57905 CenterY=-89.8542 CenterZ=0 NormalX=0 NormalY=0 NormalZ=1 AngleXU=0 Radius=1
    g317: BSplineCurve PolesCount=3 KnotsCount=2 Degree=2 IsPeriodic=0
    g318: GeomPoint X=2.07281 Y=-91.7794 Z=0
    g319: GeomPoint X=1.57905 Y=-89.8542 Z=0
    g320: LineSegment StartX=2.07281 StartY=-91.7794 StartZ=0 EndX=42.0728 EndY=-91.7794 EndZ=0
    g321: LineSegment StartX=46.0728 StartY=-87.7794 StartZ=0 EndX=46.0728 EndY=-69.424 EndZ=0
    g322: LineSegment StartX=42.5666 StartY=-67.3492 StartZ=0 EndX=1.57905 EndY=-89.8542 EndZ=0
    g323: Circle CenterX=322.073 CenterY=76.4095 CenterZ=0 NormalX=0 NormalY=0 NormalZ=1 AngleXU=0 Radius=4
    g324: BSplineCurve PolesCount=3 KnotsCount=2 Degree=2 IsPeriodic=0
    g325: GeomPoint X=318.073 Y=72.4095 Z=0
    g326: GeomPoint X=322.073 Y=76.4095 Z=0
    g327: Circle CenterX=375.073 CenterY=72.4095 CenterZ=0 NormalX=0 NormalY=0 NormalZ=1 AngleXU=0 Radius=1
    g328: Circle CenterX=375.073 CenterY=76.4095 CenterZ=0 NormalX=0 NormalY=0 NormalZ=1 AngleXU=0 Radius=1
    g329: Circle CenterX=371.073 CenterY=76.4095 CenterZ=0 NormalX=0 NormalY=0 NormalZ=1 AngleXU=0 Radius=1
    g330: BSplineCurve PolesCount=3 KnotsCount=2 Degree=2 IsPeriodic=0
    g331: GeomPoint X=375.073 Y=72.4095 Z=0
    g332: GeomPoint X=371.073 Y=76.4095 Z=0
    g333: LineSegment StartX=322.073 StartY=76.4095 StartZ=0 EndX=371.073 EndY=76.4095 EndZ=0
    g334: LineSegment StartX=318.073 StartY=72.4095 StartZ=0 EndX=318.073 EndY=-47.4805 EndZ=0
    g335: LineSegment StartX=375.073 StartY=72.4095 StartZ=0 EndX=375.073 EndY=-78.7896 EndZ=0
    g336: ArcOfCircle CenterX=-26.9272 CenterY=22.1087 CenterZ=0 NormalX=0 NormalY=0 NormalZ=1 AngleXU=0 Radius=4 StartAngle=5e-16 EndAngle=3.14159
    g337: LineSegment StartX=-22.9272 StartY=22.1087 StartZ=0 EndX=-18.9272 EndY=-83.7794 EndZ=0
    g338: LineSegment StartX=-34.9272 StartY=-83.7794 StartZ=0 EndX=-30.9272 EndY=22.1087 EndZ=0
    g339: ArcOfCircle CenterX=391.073 CenterY=22.1087 CenterZ=0 NormalX=0 NormalY=0 NormalZ=1 AngleXU=0 Radius=4 StartAngle=0 EndAngle=3.14159
    g340: LineSegment StartX=387.073 StartY=22.1087 StartZ=0 EndX=383.073 EndY=-83.7794 EndZ=0
    g341: LineSegment StartX=395.073 StartY=22.1087 StartZ=0 EndX=399.073 EndY=-83.7794 EndZ=0
    g342: Circle CenterX=-10.9272 CenterY=-78.7794 CenterZ=0 NormalX=0 NormalY=0 NormalZ=1 AngleXU=0 Radius=1
    g343: Circle CenterX=-10.9272 CenterY=-82.7794 CenterZ=0 NormalX=0 NormalY=0 NormalZ=1 AngleXU=0 Radius=1
    g344: Circle CenterX=-7.42095 CenterY=-80.8542 CenterZ=0 NormalX=0 NormalY=0 NormalZ=1 AngleXU=0 Radius=1
    g345: BSplineCurve PolesCount=3 KnotsCount=2 Degree=2 IsPeriodic=0
    g346: GeomPoint X=-10.9272 Y=-78.7794 Z=0
    g347: GeomPoint X=-7.42095 Y=-80.8542 Z=0
    g348: Circle CenterX=42.5666 CenterY=-53.4075 CenterZ=0 NormalX=0 NormalY=0 NormalZ=1 AngleXU=0 Radius=1
    g349: Circle CenterX=46.0728 CenterY=-51.4823 CenterZ=0 NormalX=0 NormalY=0 NormalZ=1 AngleXU=0 Radius=1
    g350: Circle CenterX=46.0728 CenterY=-47.4823 CenterZ=0 NormalX=0 NormalY=0 NormalZ=1 AngleXU=0 Radius=1
    g351: BSplineCurve PolesCount=3 KnotsCount=2 Degree=2 IsPeriodic=0
    g352: GeomPoint X=42.5666 Y=-53.4075 Z=0
    g353: GeomPoint X=46.0728 Y=-47.4823 Z=0
    g354: Circle CenterX=46.0728 CenterY=72.4095 CenterZ=0 NormalX=0 NormalY=0 NormalZ=1 AngleXU=0 Radius=1
    g355: Circle CenterX=46.0728 CenterY=76.4095 CenterZ=0 NormalX=0 NormalY=0 NormalZ=1 AngleXU=0 Radius=1
    g356: Circle CenterX=42.0728 CenterY=76.4095 CenterZ=0 NormalX=0 NormalY=0 NormalZ=1 AngleXU=0 Radius=1
    g357: BSplineCurve PolesCount=3 KnotsCount=2 Degree=2 IsPeriodic=0
    g358: GeomPoint X=46.0728 Y=72.4095 Z=0
    g359: GeomPoint X=42.0728 Y=76.4095 Z=0
    g360: Circle CenterX=-6.92719 CenterY=76.4095 CenterZ=0 NormalX=0 NormalY=0 NormalZ=1 AngleXU=0 Radius=1
    g361: Circle CenterX=-10.9272 CenterY=76.4095 CenterZ=0 NormalX=0 NormalY=0 NormalZ=1 AngleXU=0 Radius=1
    g362: Circle CenterX=-10.9272 CenterY=72.4095 CenterZ=0 NormalX=0 NormalY=0 NormalZ=1 AngleXU=0 Radius=1
    g363: BSplineCurve PolesCount=3 KnotsCount=2 Degree=2 IsPeriodic=0
    g364: GeomPoint X=-6.92719 Y=76.4095 Z=0
    g365: GeomPoint X=-10.9272 Y=72.4095 Z=0
    g366: LineSegment StartX=-10.9272 StartY=72.4095 StartZ=0 EndX=-10.9272 EndY=-78.7794 EndZ=0
    g367: LineSegment StartX=-7.42095 StartY=-80.8542 StartZ=0 EndX=42.5666 EndY=-53.4075 EndZ=0
    g368: LineSegment StartX=46.0728 StartY=-47.4823 StartZ=0 EndX=46.0728 EndY=72.4095 EndZ=0
    g369: LineSegment StartX=42.0728 StartY=76.4095 StartZ=0 EndX=-6.92719 EndY=76.4095 EndZ=0
    g370: LineSegment StartX=-42.9272 StartY=136.221 StartZ=0 EndX=407.073 EndY=136.221 EndZ=0
    g371: LineSegment StartX=232.072 StartY=136.221 StartZ=0 EndX=220.072 EndY=136.221 EndZ=0
    g372: LineSegment StartX=232.072 StartY=136.221 StartZ=0 EndX=232.072 EndY=124.221 EndZ=0
    g373: LineSegment StartX=220.072 StartY=136.221 StartZ=0 EndX=220.072 EndY=124.221 EndZ=0
    g374: LineSegment StartX=220.072 StartY=136.221 StartZ=0 EndX=226.072 EndY=136.221 EndZ=0
    g375: LineSegment StartX=220.072 StartY=136.221 StartZ=0 EndX=220.072 EndY=130.221 EndZ=0
    g376: LineSegment StartX=220.072 StartY=124.221 StartZ=0 EndX=226.072 EndY=124.221 EndZ=0
    g377: LineSegment StartX=232.072 StartY=124.221 StartZ=0 EndX=232.072 EndY=127.221 EndZ=0
    g378: LineSegment StartX=232.072 StartY=136.221 StartZ=0 EndX=232.072 EndY=133.221 EndZ=0
    g379-g383: Circle x5 (B-spline internal-alignment scaffolding for g384; pole/knot coordinates omitted)
    g384: BSplineCurve PolesCount=5 KnotsCount=3 Degree=3 IsPeriodic=0
    g385: GeomPoint X=232.072 Y=133.221 Z=0
    g386: GeomPoint X=223.072 Y=130.221 Z=0
    g387: GeomPoint X=232.072 Y=127.221 Z=0
    g388: LineSegment StartX=189.124 StartY=124.221 StartZ=0 EndX=302.073 EndY=124.221 EndZ=0
    g389: LineSegment StartX=132.072 StartY=136.221 StartZ=0 EndX=132.072 EndY=124.221 EndZ=0
    g390: LineSegment StartX=132.072 StartY=136.221 StartZ=0 EndX=144.072 EndY=136.221 EndZ=0
    g391: LineSegment StartX=144.072 StartY=136.221 StartZ=0 EndX=144.072 EndY=124.221 EndZ=0
    g392: LineSegment StartX=144.072 StartY=136.221 StartZ=0 EndX=138.072 EndY=136.221 EndZ=0
    g393: LineSegment StartX=144.072 StartY=136.221 StartZ=0 EndX=144.072 EndY=130.221 EndZ=0
    g394: LineSegment StartX=132.072 StartY=136.221 StartZ=0 EndX=132.072 EndY=133.221 EndZ=0
    g395: LineSegment StartX=132.072 StartY=133.221 StartZ=0 EndX=132.072 EndY=127.221 EndZ=0
    g396-g400: Circle x5 (B-spline internal-alignment scaffolding for g401; pole/knot coordinates omitted)
    g401: BSplineCurve PolesCount=5 KnotsCount=3 Degree=3 IsPeriodic=0
    g402: GeomPoint X=132.072 Y=133.221 Z=0
    g403: GeomPoint X=141.072 Y=130.221 Z=0
    g404: GeomPoint X=132.072 Y=127.221 Z=0
    g405: LineSegment StartX=132.072 StartY=124.221 StartZ=0 EndX=175.022 EndY=124.221 EndZ=0
    g406: LineSegment StartX=62.0728 StartY=124.221 StartZ=0 EndX=132.072 EndY=124.221 EndZ=0
    g407: LineSegment StartX=132.072 StartY=136.221 StartZ=0 EndX=131.457 EndY=138.832 EndZ=0
    ... +61 more geometry lines
  constraints (808):
    c: Vertical(g0)
    c: Vertical(g1)
    c: Block(g1)
    c: Block(g0)
    c: Weight(g4) = 1
    c: Equal(g4,g5)
    c: Equal(g4,g6)
    c: InternalAlignment(g4,g7)
    c: InternalAlignment(g5,g7)
    c: InternalAlignment(g6,g7)
    c: InternalAlignment(g8,g7)
    c: InternalAlignment(g9,g7)
    c: Weight(g10) = 1
    c: Equal(g10,g11)
    c: Equal(g10,g12)
    c: InternalAlignment(g10,g13)
    c: InternalAlignment(g11,g13)
    c: InternalAlignment(g12,g13)
    c: InternalAlignment(g14,g13)
    c: InternalAlignment(g15,g13)
    c: Block(g13)
    c: Block(g7)
    c: Weight(g16) = 1
    c: Equal(g16,g17)
    c: Equal(g16,g18)
    c: InternalAlignment(g16,g19)
    c: InternalAlignment(g17,g19)
    c: InternalAlignment(g18,g19)
    c: InternalAlignment(g20,g19)
    c: InternalAlignment(g21,g19)
    c: Weight(g22) = 1
    c: Equal(g22,g23)
    c: Equal(g22,g24)
    c: InternalAlignment(g22,g25)
    c: InternalAlignment(g23,g25)
    c: InternalAlignment(g24,g25)
    c: InternalAlignment(g26,g25)
    c: InternalAlignment(g27,g25)
    c: Block(g25)
    c: Block(g19)
    c: Weight(g28) = 1
    c: Equal(g28,g29)
    c: Equal(g28,g30)
    c: InternalAlignment(g28,g31)
    c: InternalAlignment(g29,g31)
    c: InternalAlignment(g30,g31)
    c: InternalAlignment(g32,g31)
    c: InternalAlignment(g33,g31)
    c: Weight(g34) = 1
    c: Equal(g34,g35)
    c: Equal(g34,g36)
    c: InternalAlignment(g34,g37)
    c: InternalAlignment(g35,g37)
    c: InternalAlignment(g36,g37)
    c: InternalAlignment(g38,g37)
    c: InternalAlignment(g39,g37)
    c: Block(g31)
    c: Block(g37)
    c: Coincident(g40,g1)
    c: Coincident(g40,g0)
    c: Horizontal(g40)
    c: Distance(g40) = 450
    c: Weight(g41) = 1
    c: Equal(g41,g42)
    c: Equal(g41,g43)
    c: InternalAlignment(g41,g44)
    c: InternalAlignment(g42,g44)
    c: InternalAlignment(g43,g44)
    c: InternalAlignment(g45,g44)
    c: InternalAlignment(g46,g44)
    c: Block(g44)
    c: Weight(g47) = 1
    c: Equal(g47,g48)
    c: Equal(g47,g49)
    c: InternalAlignment(g47,g50)
    c: InternalAlignment(g48,g50)
    c: InternalAlignment(g49,g50)
    c: InternalAlignment(g51,g50)
    c: InternalAlignment(g52,g50)
    c: Block(g50)
    c: Weight(g53) = 1
    c: Equal(g53,g54)
    c: Equal(g53,g55)
    c: InternalAlignment(g53,g56)
    c: InternalAlignment(g54,g56)
    c: InternalAlignment(g55,g56)
    c: InternalAlignment(g57,g56)
    c: InternalAlignment(g58,g56)
    c: Block(g56)
    c: Weight(g59) = 1
    c: Equal(g59,g60)
    c: Equal(g59,g61)
    c: InternalAlignment(g59,g62)
    c: InternalAlignment(g60,g62)
    c: InternalAlignment(g61,g62)
    c: InternalAlignment(g63,g62)
    c: InternalAlignment(g64,g62)
    c: Block(g62)
    c: Weight(g65) = 1
    c: Equal(g65,g66)
    c: Equal(g65,g67)
    c: InternalAlignment(g65,g68)
    c: InternalAlignment(g66,g68)
    c: InternalAlignment(g67,g68)
    c: InternalAlignment(g69,g68)
    c: InternalAlignment(g70,g68)
    c: Weight(g71) = 1
    c: Equal(g71,g72)
    c: Equal(g71,g73)
    c: InternalAlignment(g71,g74)
    c: InternalAlignment(g72,g74)
    c: InternalAlignment(g73,g74)
    c: InternalAlignment(g75,g74)
    c: InternalAlignment(g76,g74)
    c: Block(g68)
    c: Block(g74)
    c: Coincident(g77,g68)
    c: Coincident(g77,g74)
    c: Vertical(g77)
    c: Coincident(g78,g68)
    c: Coincident(g78,g50)
    c: Coincident(g79,g50)
    c: Coincident(g79,g74)
    c: Weight(g80) = 1
    c: Equal(g80,g81)
    c: Equal(g80,g82)
    c: InternalAlignment(g80,g83)
    c: InternalAlignment(g81,g83)
    c: InternalAlignment(g82,g83)
    c: InternalAlignment(g84,g83)
    c: InternalAlignment(g85,g83)
    c: Weight(g86) = 1
    c: Equal(g86,g87)
    c: Equal(g86,g88)
    c: InternalAlignment(g86,g89)
    c: InternalAlignment(g87,g89)
    c: InternalAlignment(g88,g89)
    c: InternalAlignment(g90,g89)
    c: InternalAlignment(g91,g89)
    c: Block(g83)
    c: Block(g89)
    c: Coincident(g92,g83)
    c: Coincident(g92,g89)
    c: Vertical(g92)
    c: Coincident(g93,g83)
    c: Coincident(g93,g44)
    c: Coincident(g94,g44)
    c: Coincident(g94,g89)
    c: Weight(g95) = 1
    c: Equal(g95,g96)
    c: Equal(g95,g97)
    c: InternalAlignment(g95,g98)
    c: InternalAlignment(g96,g98)
    c: InternalAlignment(g97,g98)
    c: InternalAlignment(g99,g98)
    c: InternalAlignment(g100,g98)
    c: Weight(g101) = 1
    c: Equal(g101,g102)
    c: Equal(g101,g103)
    c: InternalAlignment(g101,g104)
    c: InternalAlignment(g102,g104)
    c: InternalAlignment(g103,g104)
    c: InternalAlignment(g105,g104)
    c: InternalAlignment(g106,g104)
    c: Block(g98)
    c: Block(g104)
    c: Coincident(g107,g98)
    c: Coincident(g107,g104)
    c: Vertical(g107)
    c: Coincident(g108,g104)
    c: Coincident(g108,g62)
    c: Coincident(g109,g62)
    c: Coincident(g109,g98)
    c: Weight(g110) = 1
    c: Equal(g110,g111)
    c: Equal(g110,g112)
    c: InternalAlignment(g110,g113)
    c: InternalAlignment(g111,g113)
    c: InternalAlignment(g112,g113)
    c: InternalAlignment(g114,g113)
    c: InternalAlignment(g115,g113)
    c: Weight(g116) = 1
    c: Equal(g116,g117)
    c: Equal(g116,g118)
    c: InternalAlignment(g116,g119)
    c: InternalAlignment(g117,g119)
    c: InternalAlignment(g118,g119)
    c: InternalAlignment(g120,g119)
    c: InternalAlignment(g121,g119)
    c: Block(g113)
    c: Block(g119)
    c: Coincident(g122,g113)
    c: Coincident(g122,g119)
    c: Vertical(g122)
    c: Coincident(g123,g119)
    c: Coincident(g123,g56)
    c: Coincident(g124,g56)
    c: Coincident(g124,g113)
    c: Weight(g125) = 1
    c: Equal(g125,g126)
    c: Equal(g125,g127)
    c: InternalAlignment(g125,g128)
    c: InternalAlignment(g126,g128)
    c: InternalAlignment(g127,g128)
    c: InternalAlignment(g129,g128)
    c: InternalAlignment(g130,g128)
    c: Weight(g131) = 1
    c: Equal(g131,g132)
    c: Equal(g131,g133)
    c: InternalAlignment(g131,g134)
    c: InternalAlignment(g132,g134)
    c: InternalAlignment(g133,g134)
    c: InternalAlignment(g135,g134)
    c: InternalAlignment(g136,g134)
    c: Weight(g137) = 1
    c: Equal(g137,g138)
    c: Equal(g137,g139)
    c: InternalAlignment(g137,g140)
    c: InternalAlignment(g138,g140)
    c: InternalAlignment(g139,g140)
    c: InternalAlignment(g141,g140)
    c: InternalAlignment(g142,g140)
    c: Weight(g143) = 1
    c: Equal(g143,g144)
    c: Equal(g143,g145)
    c: InternalAlignment(g143,g146)
    c: InternalAlignment(g144,g146)
    c: InternalAlignment(g145,g146)
    c: InternalAlignment(g147,g146)
    c: InternalAlignment(g148,g146)
    c: Block(g146)
    c: Block(g140)
    c: Block(g134)
    c: Block(g128)
    c: Coincident(g149,g25)
    c: Coincident(g149,g146)
    c: Coincident(g150,g146)
    c: Coincident(g150,g140)
    c: Horizontal(g150)
    c: Coincident(g151,g140)
    c: Coincident(g151,g25)
    c: Vertical(g151)
    c: Coincident(g152,g19)
    c: Coincident(g152,g134)
    c: Vertical(g152)
    c: Coincident(g153,g134)
    c: Coincident(g153,g128)
    c: Horizontal(g153)
    c: Coincident(g154,g128)
    c: Coincident(g154,g19)
    c: Weight(g155) = 1
    c: Equal(g155,g156)
    c: Equal(g155,g157)
    c: InternalAlignment(g155,g158)
    c: InternalAlignment(g156,g158)
    c: InternalAlignment(g157,g158)
    c: InternalAlignment(g159,g158)
    c: InternalAlignment(g160,g158)
    c: Weight(g161) = 1
    c: Equal(g161,g162)
    c: Equal(g161,g163)
    c: InternalAlignment(g161,g164)
    c: InternalAlignment(g162,g164)
    c: InternalAlignment(g163,g164)
    c: InternalAlignment(g165,g164)
    c: InternalAlignment(g166,g164)
    c: Weight(g167) = 1
    c: Equal(g167,g168)
    c: Equal(g167,g169)
    c: InternalAlignment(g167,g170)
    c: InternalAlignment(g168,g170)
    c: InternalAlignment(g169,g170)
    c: InternalAlignment(g171,g170)
    c: InternalAlignment(g172,g170)
    c: Weight(g173) = 1
    c: Equal(g173,g174)
    c: Equal(g173,g175)
    c: InternalAlignment(g173,g176)
    c: InternalAlignment(g174,g176)
    c: InternalAlignment(g175,g176)
    c: InternalAlignment(g177,g176)
    c: InternalAlignment(g178,g176)
    c: Block(g176)
    c: Block(g170)
    c: Block(g164)
    c: Block(g158)
    c: Coincident(g179,g170)
    c: Coincident(g179,g7)
    c: Vertical(g179)
    c: Coincident(g180,g13)
    c: Coincident(g180,g164)
    c: Vertical(g180)
    c: Coincident(g181,g158)
    c: Coincident(g181,g13)
    c: Coincident(g182,g7)
    c: Weight(g183) = 1
    c: Equal(g183,g184)
    c: Equal(g183,g185)
    c: InternalAlignment(g183,g186)
    c: InternalAlignment(g184,g186)
    c: InternalAlignment(g185,g186)
    c: InternalAlignment(g187,g186)
    c: InternalAlignment(g188,g186)
    c: Weight(g189) = 1
    c: Equal(g189,g190)
    c: Equal(g189,g191)
    c: InternalAlignment(g189,g192)
    c: InternalAlignment(g190,g192)
    c: InternalAlignment(g191,g192)
    c: InternalAlignment(g193,g192)
    c: InternalAlignment(g194,g192)
    c: Block(g192)
    c: Block(g186)
    c: Coincident(g195,g192)
    c: Coincident(g195,g31)
    c: Coincident(g196,g31)
    c: Coincident(g196,g186)
    c: Coincident(g197,g186)
    c: Coincident(g197,g192)
    c: Vertical(g197)
    c: Weight(g198) = 1
    c: Equal(g198,g199)
    c: Equal(g198,g200)
    c: InternalAlignment(g198,g201)
    c: InternalAlignment(g199,g201)
    c: InternalAlignment(g200,g201)
    c: InternalAlignment(g202,g201)
    c: InternalAlignment(g203,g201)
    c: Weight(g204) = 1
    c: Equal(g204,g205)
    c: Equal(g204,g206)
    c: InternalAlignment(g204,g207)
    c: InternalAlignment(g205,g207)
    c: InternalAlignment(g206,g207)
    c: InternalAlignment(g208,g207)
    c: InternalAlignment(g209,g207)
    c: Block(g207)
    c: Block(g201)
    c: Coincident(g210,g201)
    c: Coincident(g210,g37)
    c: Coincident(g211,g37)
    c: Coincident(g211,g207)
    c: Coincident(g212,g207)
    c: Coincident(g212,g201)
    c: Vertical(g212)
    c: Horizontal(g213)
    c: Block(g213)
    c: Vertical(g214)
    c: Block(g214)
    c: Block(g215)
    c: Weight(g216) = 1
    c: Equal(g216,g217)
    c: Equal(g216,g218)
    c: InternalAlignment(g216,g219)
    c: InternalAlignment(g217,g219)
    c: InternalAlignment(g218,g219)
    c: InternalAlignment(g220,g219)
    c: InternalAlignment(g221,g219)
    c: Weight(g222) = 1
    c: Equal(g222,g223)
    c: Equal(g222,g224)
    c: InternalAlignment(g222,g225)
    c: InternalAlignment(g223,g225)
    c: InternalAlignment(g224,g225)
    c: InternalAlignment(g226,g225)
    c: InternalAlignment(g227,g225)
    c: Weight(g228) = 1
    c: Equal(g228,g229)
    c: Equal(g228,g230)
    c: InternalAlignment(g228,g231)
    c: InternalAlignment(g229,g231)
    c: InternalAlignment(g230,g231)
    c: InternalAlignment(g232,g231)
    c: InternalAlignment(g233,g231)
    c: Weight(g234) = 1
    c: Equal(g234,g235)
    c: Equal(g234,g236)
    c: InternalAlignment(g234,g237)
    c: InternalAlignment(g235,g237)
    c: InternalAlignment(g236,g237)
    c: InternalAlignment(g238,g237)
    c: InternalAlignment(g239,g237)
    c: Block(g219)
    c: Block(g225)
    c: Block(g231)
    c: Block(g237)
    c: Coincident(g240,g225)
    c: Coincident(g240,g219)
    c: Horizontal(g240)
    c: Block(g182)
    c: Weight(g241) = 1
    c: Equal(g241,g242)
    c: Equal(g241,g243)
    c: InternalAlignment(g241,g244)
    c: InternalAlignment(g242,g244)
    c: InternalAlignment(g243,g244)
    c: InternalAlignment(g245,g244)
    c: InternalAlignment(g246,g244)
    c: Weight(g247) = 1
    c: Equal(g247,g248)
    c: Equal(g247,g249)
    c: InternalAlignment(g247,g250)
    c: InternalAlignment(g248,g250)
    c: InternalAlignment(g249,g250)
    c: InternalAlignment(g251,g250)
    c: InternalAlignment(g252,g250)
    c: Block(g244)
    c: Block(g250)
    c: Coincident(g253,g244)
    c: Coincident(g253,g250)
    c: Weight(g254) = 1
    c: Equal(g254,g255)
    c: Equal(g254,g256)
    c: InternalAlignment(g254,g257)
    c: InternalAlignment(g255,g257)
    c: InternalAlignment(g256,g257)
    c: InternalAlignment(g258,g257)
    c: InternalAlignment(g259,g257)
    c: Weight(g260) = 1
    c: Equal(g260,g261)
    c: Equal(g260,g262)
    c: InternalAlignment(g260,g263)
    c: InternalAlignment(g261,g263)
    c: InternalAlignment(g262,g263)
    c: InternalAlignment(g264,g263)
    c: InternalAlignment(g265,g263)
    c: Weight(g266) = 1
    c: Equal(g266,g267)
    c: Equal(g266,g268)
    c: InternalAlignment(g266,g269)
    c: InternalAlignment(g267,g269)
    c: InternalAlignment(g268,g269)
    c: InternalAlignment(g270,g269)
    c: InternalAlignment(g271,g269)
    c: Block(g269)
    c: Block(g263)
    c: Block(g257)
    c: Coincident(g272,g263)
    c: Coincident(g272,g257)
    c: Coincident(g273,g257)
    c: Coincident(g273,g269)
    c: Vertical(g273)
    c: Coincident(g274,g269)
    c: Coincident(g274,g263)
    c: Horizontal(g274)
    c: Weight(g275) = 1
    c: Equal(g275,g276)
    c: InternalAlignment(g275,g277)
    c: InternalAlignment(g276,g277)
    c: InternalAlignment(g278,g277)
    c: InternalAlignment(g279,g277)
    c: Weight(g280) = 1
    c: InternalAlignment(g281,g283)
    c: InternalAlignment(g282,g283)
    c: InternalAlignment(g284,g283)
    c: InternalAlignment(g285,g283)
    c: Weight(g286) = 1
    c: Equal(g286,g287)
    c: Equal(g286,g288)
    c: InternalAlignment(g286,g289)
    c: InternalAlignment(g287,g289)
    c: InternalAlignment(g288,g289)
    c: InternalAlignment(g290,g289)
    c: InternalAlignment(g291,g289)
    c: Equal(g292,g293)
    c: Equal(g292,g294)
    c: InternalAlignment(g292,g295)
    c: InternalAlignment(g293,g295)
    c: InternalAlignment(g294,g295)
    c: InternalAlignment(g296,g295)
    c: InternalAlignment(g297,g295)
    c: Block(g283)
    c: Block(g289)
    c: Block(g295)
    c: Block(g277)
    c: Coincident(g298,g277)
    c: Coincident(g298,g283)
    c: Horizontal(g298)
    c: Coincident(g299,g283)
    c: Coincident(g299,g289)
    c: Vertical(g299)
    c: Coincident(g300,g289)
    c: Coincident(g300,g295)
    c: Horizontal(g300)
    c: Coincident(g301,g295)
    c: Coincident(g301,g277)
    c: Weight(g302) = 1
    c: Equal(g302,g303)
    c: Equal(g302,g304)
    c: InternalAlignment(g302,g305)
    c: InternalAlignment(g303,g305)
    c: InternalAlignment(g304,g305)
    c: InternalAlignment(g306,g305)
    c: InternalAlignment(g307,g305)
    c: Weight(g308) = 1
    c: Equal(g308,g309)
    c: Equal(g308,g310)
    c: InternalAlignment(g308,g311)
    c: InternalAlignment(g309,g311)
    c: InternalAlignment(g310,g311)
    c: InternalAlignment(g312,g311)
    c: Weight(g314) = 1
    c: Equal(g314,g315)
    c: Equal(g314,g316)
    c: InternalAlignment(g314,g317)
    c: InternalAlignment(g315,g317)
    c: InternalAlignment(g316,g317)
    c: InternalAlignment(g318,g317)
    c: InternalAlignment(g319,g317)
    c: Block(g317)
    c: Block(g311)
    c: Block(g305)
    c: Coincident(g320,g317)
    c: Coincident(g320,g311)
    c: Horizontal(g320)
    c: Coincident(g321,g311)
    c: Coincident(g321,g305)
    c: Vertical(g321)
    c: Coincident(g322,g305)
    c: Coincident(g322,g317)
    c: InternalAlignment(g323,g324)
    c: InternalAlignment(g325,g324)
    c: InternalAlignment(g326,g324)
    c: Block(g324)
    c: Equal(g327,g328)
    c: Equal(g327,g329)
    c: InternalAlignment(g327,g330)
    c: InternalAlignment(g328,g330)
    c: InternalAlignment(g329,g330)
    c: InternalAlignment(g331,g330)
    c: InternalAlignment(g332,g330)
    c: Block(g330)
    c: Coincident(g333,g324)
    c: Horizontal(g333)
    c: Block(g333)
    c: Coincident(g334,g324)
    c: Coincident(g334,g250)
    c: Vertical(g334)
    c: Coincident(g335,g330)
    c: Coincident(g335,g244)
    c: Vertical(g335)
    c: Block(g336)
    c: Block(g2)
    c: Distance(g334) = 119.89
    c: Coincident(g337,g336)
    c: Coincident(g337,g2)
    c: Coincident(g338,g2)
    c: Coincident(g338,g336)
    c: Block(g3)
    c: Block(g339)
    c: Coincident(g340,g339)
    c: Coincident(g340,g3)
    c: Coincident(g341,g339)
    c: Coincident(g341,g3)
    c: Block(g341)
    c: Block(g340)
    c: Weight(g342) = 1
    c: Equal(g342,g344)
    c: InternalAlignment(g342,g345)
    c: InternalAlignment(g343,g345)
    c: InternalAlignment(g344,g345)
    c: InternalAlignment(g346,g345)
    c: InternalAlignment(g347,g345)
    c: InternalAlignment(g352,g351)
    c: InternalAlignment(g353,g351)
    c: InternalAlignment(g355,g357)
    c: Horizontal(g369)
    c: Coincident(g370,g0)
    c: Horizontal(g370)
    c: Block(g370)
    c: Distance(g370) = 450
    c: Horizontal(g371)
    c: Distance(g371) = 12
    c: Coincident(g373,g371)
    c: Vertical(g373)
    c: Horizontal(g374)
    c: Vertical(g375)
    c: Distance(g375) = 6
    c: Coincident(g375,g371)
    c: Coincident(g374,g371)
    c: Block(g373)
    c: Coincident(g376,g373)
    c: Horizontal(g376)
    c: Distance(g376) = 6
    c: Vertical(g377)
    c: Distance(g377) = 3
    c: Vertical(g378)
    c: Distance(g378) = 3
    c: Coincident(g372,g377)
    c: Coincident(g384,g378)
    c: Weight(g379) = 1
    c: Equal(g379,g380)
    c: Coincident(g380,g374)
    c: Equal(g379,g381)
    c: Coincident(g381,g375)
    c: Equal(g379,g382)
    c: Coincident(g382,g376)
    c: Equal(g379,g383)
    c: Coincident(g384,g377)
    c: InternalAlignment(g379-g383 -> g384) x5
    c: InternalAlignment(g385,g384)
    c: InternalAlignment(g386,g384)
    c: InternalAlignment(g387,g384)
    c: Coincident(g388,g164)
    c: Coincident(g388,g158)
    c: Coincident(g392,g390)
    c: Vertical(g393)
    c: Distance(g393) = 6
    c: Coincident(g393,g390)
    c: Vertical(g394)
    c: Distance(g394) = 3
    c: Vertical(g395)
    c: Distance(g395) = 6
    c: Coincident(g395,g394)
    c: Coincident(g401,g394)
    c: Weight(g396) = 1
    c: Equal(g396,g397)
    c: Coincident(g397,g392)
    c: Equal(g396,g398)
    c: Coincident(g398,g393)
    c: Equal(g396,g399)
    c: Equal(g396,g400)
    c: Coincident(g401,g395)
    c: InternalAlignment(g396-g400 -> g401) x5
    c: InternalAlignment(g402,g401)
    c: InternalAlignment(g403,g401)
    c: InternalAlignment(g404,g401)
    c: Coincident(g405,g389)
    c: Coincident(g405,g170)
    c: Horizontal(g405)
    c: Block(g401)
    c: Coincident(g406,g176)
    c: Coincident(g406,g389)
    c: Horizontal(g406)
    c: Block(g405)
    c: Coincident(g408,g389)
    c: PointOnObject(g408,g153)
    c: Vertical(g408)
    c: Block(g409)
    c: Coincident(g410,g409)
    c: Vertical(g410)
    c: PointOnObject(g410,g40)
    c: Block(g410)
    c: Coincident(g411,g409)
    c: Vertical(g411)
    c: Block(g411)
    c: Vertical(g412)
    c: Distance(g412) = 3
    c: Equal(g379,g415) = 1
    c: Equal(g415,g416)
    c: InternalAlignment(g415,g417)
    c: InternalAlignment(g416,g417)
    c: InternalAlignment(g413,g417)
    c: InternalAlignment(g414,g417)
    c: InternalAlignment(g418,g417)
    c: Block(g417)
    c: Coincident(g418,g412)
    c: Coincident(g419,g417)
    c: PointOnObject(g419,g150)
    c: Vertical(g419)
    c: Distance(g420) = 3
    c: Block(g420)
    c: Distance(g421) = 3
    c: Parallel(g421,g420)
    c: Coincident(g421,g420)
    c: Coincident(g422,g420)
    c: Perpendicular(g422,g420)
    c: Distance(g422) = 3
    c: Coincident(g423,g421)
    c: Perpendicular(g423,g421)
    c: Distance(g423) = 3
    c: Coincident(g424,g420)
    c: Perpendicular(g424,g421)
    c: Distance(g424) = 6
    c: Coincident(g425,g424)
    c: PointOnObject(g423,g425)
    c: Coincident(g426,g420)
    c: PointOnObject(g426,g79)
    c: Block(g426)
    c: Distance(g427) = 2.76
    c: Coincident(g428,g427)
    c: Parallel(g427,g428)
    c: PointOnObject(g428,g181)
    c: Distance(g428) = 2.41
    c: Block(g428)
    c: Coincident(g429,g427)
    c: Distance(g429) = 6.6
    c: Perpendicular(g429,g428)
    c: Distance(g430) = 6.6
    c: Coincident(g431,g429)
    c: Coincident(g431,g430)
    c: Block(g432)
    c: Coincident(g433,g432)
    c: Vertical(g433)
    c: Distance(g433) = 3.6
    c: Coincident(g434,g427)
    c: Parallel(g427,g434)
    c: PointOnObject(g434,g78)
    c: Block(g434)
    c: Coincident(g435,g421)
    c: Parallel(g435,g421)
    c: PointOnObject(g435,g211)
    c: Block(g435)
    c: Coincident(g436,g435)
    c: Vertical(g436)
    c: PointOnObject(g436,g210)
    c: Coincident(g437,g436)
    c: Perpendicular(g437,g210)
    c: Distance(g437) = 3
    c: Coincident(g438,g437)
    c: Block(g437)
    c: Distance(g438) = 3
    c: Parallel(g437,g438)
    c: Coincident(g439,g438)
    c: Distance(g439) = 3
    c: Parallel(g438,g439)
    c: Coincident(g440,g439)
    c: Parallel(g440,g437)
    c: PointOnObject(g440,g124)
    c: PointOnObject(g441,g53)
    c: Tangent(g440,g441)
    c: Coincident(g442,g439)
    c: Perpendicular(g442,g439)
    c: Coincident(g443,g437)
    c: Parallel(g443,g442)
    c: Distance(g443) = 3
    c: Distance(g442) = 3
    c: PointOnObject(g442,g444)
    c: Block(g444)
    c: PointOnObject(g445,g123)
    c: Perpendicular(g123,g445)
    c: Distance(g445) = 2.41
    c: Block(g445)
    c: Coincident(g446,g445)
    c: Perpendicular(g123,g446)
    c: Distance(g446) = 2.76
    c: Coincident(g447,g446)
    c: Perpendicular(g123,g447)
    c: PointOnObject(g447,g149)
    c: Coincident(g448,g445)
    c: Parallel(g123,g448)
    c: Distance(g448) = 6.6
    c: Coincident(g449,g446)
    c: Parallel(g123,g449)
    c: Coincident(g450,g448)
    c: Distance(g449) = 6.6
    c: Coincident(g449,g450)
    c: Block(g149)
    c: Block(g124)
    c: Block(g211)
    c: Block(g181)
    c: Block(g78)
    c: Block(g79)
    c: Block(g430)
    c: Coincident(g451,g447)
    c: Distance(g451) = 46
    c: Parallel(g149,g451)
    c: Coincident(g452,g451)
    c: Horizontal(g452)
    c: PointOnObject(g452,g154)
    c: Coincident(g453,g451)
    c: Vertical(g453)
    c: Distance(g453) = 9
    c: Block(g452)
    c: PointOnObject(g454,g93)
    c: Distance(g455) = 6.6
    c: Distance(g456) = 6.6
    c: Block(g454)
    c: Coincident(g457,g456)
    c: Coincident(g457,g455)
    c: Perpendicular(g457,g182)
    c: Coincident(g458,g455)
    c: Perpendicular(g458,g182)
    c: PointOnObject(g458,g182)
    c: Block(g458)
    c: Block(g457)
    c: Block(g456)
    c: PointOnObject(g459,g196)
    c: Perpendicular(g196,g459)
    c: Distance(g459) = 3
    c: Coincident(g460,g459)
    c: Perpendicular(g196,g460)
    c: Distance(g460) = 3
    c: Coincident(g461,g460)
    c: Perpendicular(g196,g461)
    c: Distance(g461) = 3
    c: Coincident(g462,g461)
    c: Tangent(g462,g41)
    c: PointOnObject(g462,g94)
    c: Block(g462)
    c: Block(g459)
    c: Coincident(g463,g459)
    c: Parallel(g196,g463)
    c: Distance(g463) = 3
    c: Coincident(g464,g461)
    c: Distance(g464) = 3
    c: Parallel(g196,g464)
    c: Coincident(g465,g460)
    c: Distance(g465) = 6
    c: Parallel(g465,g196)
    c: Coincident(g466,g465)
    c: PointOnObject(g464,g466)
    c: Block(g466)
    c: Coincident(g467,g458)
    c: Vertical(g467)
    c: PointOnObject(g467,g195)
    c: Coincident(g468,g467)
    c: Perpendicular(g195,g468)
FEATURE [Sketcher::SketchObject] Sketch004  label="rightSideBottom"
  FullyConstrained = false
  sketch-geometry (91):
    g0: ArcOfCircle CenterX=391.073 CenterY=-83.7794 CenterZ=0 NormalX=0 NormalY=0 NormalZ=1 AngleXU=0 Radius=8 StartAngle=3.14159 EndAngle=6.28319
    g1: Circle CenterX=306.073 CenterY=-81.8102 CenterZ=0 NormalX=0 NormalY=0 NormalZ=1 AngleXU=0 Radius=1
    g2: Circle CenterX=306.073 CenterY=-77.8102 CenterZ=0 NormalX=0 NormalY=0 NormalZ=1 AngleXU=0 Radius=1
    g3: Circle CenterX=302.567 CenterY=-42.9683 CenterZ=0 NormalX=0 NormalY=0 NormalZ=1 AngleXU=0 Radius=1
    g4: Circle CenterX=306.073 CenterY=-44.8935 CenterZ=0 NormalX=0 NormalY=0 NormalZ=1 AngleXU=0 Radius=1
    g5: Circle CenterX=306.073 CenterY=-40.8935 CenterZ=0 NormalX=0 NormalY=0 NormalZ=1 AngleXU=0 Radius=1
    g6: BSplineCurve PolesCount=3 KnotsCount=2 Degree=2 IsPeriodic=0
    g7: GeomPoint X=302.567 Y=-42.9683 Z=0
    g8: GeomPoint X=306.073 Y=-40.8935 Z=0
    g9: Circle CenterX=371.567 CenterY=-80.8644 CenterZ=0 NormalX=0 NormalY=0 NormalZ=1 AngleXU=0 Radius=1
    g10: Circle CenterX=375.073 CenterY=-82.7896 CenterZ=0 NormalX=0 NormalY=0 NormalZ=1 AngleXU=0 Radius=1
    g11: Circle CenterX=375.073 CenterY=-78.7896 CenterZ=0 NormalX=0 NormalY=0 NormalZ=1 AngleXU=0 Radius=1
    g12: GeomPoint X=371.567 Y=-80.8644 Z=0
    g13: GeomPoint X=375.073 Y=-78.7896 Z=0
    g14: Circle CenterX=318.073 CenterY=-51.4823 CenterZ=0 NormalX=0 NormalY=0 NormalZ=1 AngleXU=0 Radius=1
    g15: Circle CenterX=318.073 CenterY=-47.4805 CenterZ=0 NormalX=0 NormalY=0 NormalZ=1 AngleXU=0 Radius=1
    g16: GeomPoint X=321.579 Y=-53.4075 Z=0
    g17: GeomPoint X=318.073 Y=-47.4805 Z=0
    g18: Circle CenterX=321.579 CenterY=-67.3492 CenterZ=0 NormalX=0 NormalY=0 NormalZ=1 AngleXU=0 Radius=1
    g19: Circle CenterX=318.073 CenterY=-65.424 CenterZ=0 NormalX=0 NormalY=0 NormalZ=1 AngleXU=0 Radius=1
    g20: Circle CenterX=318.073 CenterY=-69.424 CenterZ=0 NormalX=0 NormalY=0 NormalZ=1 AngleXU=0 Radius=1
    g21: GeomPoint X=321.579 Y=-67.3492 Z=0
    g22: GeomPoint X=318.073 Y=-69.424 Z=0
    g23: Circle CenterX=362.567 CenterY=-89.8542 CenterZ=0 NormalX=0 NormalY=0 NormalZ=1 AngleXU=0 Radius=1
    g24: Circle CenterX=366.073 CenterY=-91.7794 CenterZ=0 NormalX=0 NormalY=0 NormalZ=1 AngleXU=0 Radius=1
    g25: Circle CenterX=362.073 CenterY=-91.7794 CenterZ=0 NormalX=0 NormalY=0 NormalZ=1 AngleXU=0 Radius=1
    g26: GeomPoint X=362.567 Y=-89.8542 Z=0
    g27: GeomPoint X=362.073 Y=-91.7794 Z=0
    g28: Circle CenterX=322.073 CenterY=-91.7794 CenterZ=0 NormalX=0 NormalY=0 NormalZ=1 AngleXU=0 Radius=1
    g29: Circle CenterX=318.073 CenterY=-91.7794 CenterZ=0 NormalX=0 NormalY=0 NormalZ=1 AngleXU=0 Radius=1
    g30: Circle CenterX=318.073 CenterY=-87.7794 CenterZ=0 NormalX=0 NormalY=0 NormalZ=1 AngleXU=0 Radius=1
    g31: GeomPoint X=322.073 Y=-91.7794 Z=0
    g32: GeomPoint X=318.073 Y=-87.7794 Z=0
    g33: ArcOfCircle CenterX=391.073 CenterY=22.1087 CenterZ=0 NormalX=0 NormalY=0 NormalZ=1 AngleXU=0 Radius=4 StartAngle=0 EndAngle=3.14159
    g34: LineSegment StartX=387.073 StartY=22.1087 StartZ=0 EndX=383.073 EndY=-83.7794 EndZ=0
    g35: LineSegment StartX=395.073 StartY=22.1087 StartZ=0 EndX=399.073 EndY=-83.7794 EndZ=0
    g36: LineSegment StartX=232.072 StartY=-103.779 StartZ=0 EndX=232.072 EndY=-100.779 EndZ=0
    g37: GeomPoint X=232.072 Y=-94.7794 Z=0
    g38: GeomPoint X=223.072 Y=-97.7794 Z=0
    g39: Circle CenterX=232.072 CenterY=-94.7794 CenterZ=0 NormalX=0 NormalY=0 NormalZ=1 AngleXU=0 Radius=1
    g40: Circle CenterX=232.072 CenterY=-100.779 CenterZ=0 NormalX=0 NormalY=0 NormalZ=1 AngleXU=0 Radius=1
    g41: BSplineCurve PolesCount=5 KnotsCount=3 Degree=3 IsPeriodic=0
    g42: GeomPoint X=232.072 Y=-100.779 Z=0
    g43: LineSegment StartX=232.072 StartY=-94.7794 StartZ=0 EndX=232.072 EndY=-91.7794 EndZ=0
    g44: LineSegment StartX=245.072 StartY=-31.3037 StartZ=0 EndX=243.535 EndY=-33.1602 EndZ=0
    g45: LineSegment StartX=241.775 StartY=-35.2862 StartZ=0 EndX=240.266 EndY=-37.1092 EndZ=0
    g46: LineSegment StartX=243.535 StartY=-33.1602 StartZ=0 EndX=248.619 EndY=-37.3688 EndZ=0
    g47: LineSegment StartX=241.775 StartY=-35.2862 StartZ=0 EndX=246.859 EndY=-39.4949 EndZ=0
    g48: LineSegment StartX=248.619 StartY=-37.3688 StartZ=0 EndX=246.859 EndY=-39.4949 EndZ=0
    g49: LineSegment StartX=232.072 StartY=-103.779 StartZ=0 EndX=407.073 EndY=-103.779 EndZ=0
    g50: LineSegment StartX=299.888 StartY=-86.6413 StartZ=0 EndX=240.266 EndY=-37.1092 EndZ=0
    g51: LineSegment StartX=245.072 StartY=-11.4025 StartZ=0 EndX=302.567 EndY=-42.9683 EndZ=0
    g52: BSplineCurve PolesCount=3 KnotsCount=2 Degree=2 IsPeriodic=0
    g53: BSplineCurve PolesCount=3 KnotsCount=2 Degree=2 IsPeriodic=0
    g54: LineSegment StartX=321.579 StartY=-53.4075 StartZ=0 EndX=371.567 EndY=-80.8644 EndZ=0
    g55: BSplineCurve PolesCount=3 KnotsCount=2 Degree=2 IsPeriodic=0
    g56: BSplineCurve PolesCount=3 KnotsCount=2 Degree=2 IsPeriodic=0
    g57: BSplineCurve PolesCount=3 KnotsCount=2 Degree=2 IsPeriodic=0
    g58: LineSegment StartX=318.073 StartY=-69.424 StartZ=0 EndX=318.073 EndY=-87.7794 EndZ=0
    g59: LineSegment StartX=321.579 StartY=-67.3492 StartZ=0 EndX=362.567 EndY=-89.8542 EndZ=0
    g60: LineSegment StartX=362.073 StartY=-91.7794 StartZ=0 EndX=322.073 EndY=-91.7794 EndZ=0
    g61: BSplineCurve PolesCount=3 KnotsCount=2 Degree=2 IsPeriodic=0
    g62: BSplineCurve PolesCount=3 KnotsCount=2 Degree=2 IsPeriodic=0
    g63: LineSegment StartX=245.072 StartY=-31.3037 StartZ=0 EndX=302.996 EndY=-79.2541 EndZ=0
    g64: LineSegment StartX=302.567 StartY=-56.9099 StartZ=0 EndX=239.193 EndY=-22.1109 EndZ=0
    g65: LineSegment StartX=306.073 StartY=-62.8351 StartZ=0 EndX=306.073 EndY=-77.8102 EndZ=0
    g66: BSplineCurve PolesCount=3 KnotsCount=2 Degree=2 IsPeriodic=0
    g67: LineSegment StartX=298.776 StartY=-91.7794 StartZ=0 EndX=232.072 EndY=-91.7794 EndZ=0
    g68: LineSegment StartX=245.072 StartY=-11.4025 StartZ=0 EndX=243.628 EndY=-14.0323 EndZ=0
    g69: LineSegment StartX=240.741 StartY=-19.2917 StartZ=0 EndX=239.193 EndY=-22.1109 EndZ=0
    g70: LineSegment StartX=243.628 StartY=-14.0323 StartZ=0 EndX=246.258 EndY=-15.476 EndZ=0
    g71: LineSegment StartX=240.741 StartY=-19.2917 StartZ=0 EndX=243.37 EndY=-20.7355 EndZ=0
    g72: ArcOfCircle CenterX=247.444 CenterY=-19.5495 CenterZ=0 NormalX=0 NormalY=0 NormalZ=1 AngleXU=0 Radius=4.24264 StartAngle=3.4249 EndAngle=8.13729
    g73: LineSegment StartX=407.073 StartY=-103.779 StartZ=0 EndX=407.073 EndY=48.2206 EndZ=0
    g74: LineSegment StartX=375.073 StartY=48.2206 StartZ=0 EndX=375.073 EndY=-78.7896 EndZ=0
    g75: LineSegment StartX=375.073 StartY=48.2206 StartZ=0 EndX=382.073 EndY=48.2206 EndZ=0
    g76: LineSegment StartX=407.073 StartY=48.2206 StartZ=0 EndX=400.073 EndY=48.2206 EndZ=0
    g77: LineSegment StartX=394.073 StartY=48.2206 StartZ=0 EndX=394.073 EndY=52.2206 EndZ=0
    g78: LineSegment StartX=388.073 StartY=48.2206 StartZ=0 EndX=388.073 EndY=58.2206 EndZ=0
    g79: ArcOfCircle CenterX=385.073 CenterY=61.2206 CenterZ=0 NormalX=0 NormalY=0 NormalZ=1 AngleXU=0 Radius=4.24264 StartAngle=5.49779 EndAngle=10.2102
    g80: ArcOfCircle CenterX=397.073 CenterY=55.2206 CenterZ=0 NormalX=0 NormalY=0 NormalZ=1 AngleXU=0 Radius=4.24264 StartAngle=5.49779 EndAngle=10.2102
    g81: LineSegment StartX=382.073 StartY=58.2206 StartZ=0 EndX=382.073 EndY=48.2206 EndZ=0
    g82: LineSegment StartX=400.073 StartY=52.2206 StartZ=0 EndX=400.073 EndY=48.2206 EndZ=0
    g83: LineSegment StartX=394.073 StartY=48.2206 StartZ=0 EndX=388.073 EndY=48.2206 EndZ=0
    g84: LineSegment StartX=306.073 StartY=-40.8935 StartZ=0 EndX=306.073 EndY=-27.5935 EndZ=0
    g85: LineSegment StartX=318.073 StartY=-27.5935 StartZ=0 EndX=318.073 EndY=-47.4805 EndZ=0
    g86: LineSegment StartX=306.073 StartY=-27.5935 StartZ=0 EndX=310.073 EndY=-27.5935 EndZ=0
    g87: LineSegment StartX=318.073 StartY=-27.5935 StartZ=0 EndX=314.073 EndY=-27.5935 EndZ=0
    g88: LineSegment StartX=310.073 StartY=-27.5935 StartZ=0 EndX=310.073 EndY=-31.5935 EndZ=0
    g89: LineSegment StartX=314.073 StartY=-27.5935 StartZ=0 EndX=314.073 EndY=-31.5935 EndZ=0
    g90: ArcOfCircle CenterX=312.073 CenterY=-33.5935 CenterZ=0 NormalX=0 NormalY=0 NormalZ=1 AngleXU=0 Radius=2.82843 StartAngle=2.35619 EndAngle=7.06858
  constraints (121):
    c: Distance(g44) = 2.41
    c: Block(g44)
    c: Coincident(g46,g44)
    c: Coincident(g49,g36)
    c: Horizontal(g49)
    c: Block(g49)
    c: Coincident(g50,g45)
    c: Block(g50)
    c: Coincident(g51,g6)
    c: Block(g51)
    c: Coincident(g54,g52)
    c: Coincident(g54,g53)
    c: Coincident(g58,g56)
    c: Coincident(g58,g57)
    c: Vertical(g58)
    c: Coincident(g59,g56)
    c: Coincident(g59,g55)
    c: Coincident(g60,g55)
    c: Coincident(g60,g57)
    c: Horizontal(g60)
    c: Block(g61)
    c: Block(g62)
    c: Coincident(g63,g44)
    c: Coincident(g63,g62)
    c: Coincident(g64,g61)
    c: Coincident(g65,g61)
    c: Coincident(g65,g62)
    c: Vertical(g65)
    c: Block(g66)
    c: Coincident(g66,g50)
    c: Coincident(g67,g66)
    c: Coincident(g67,g43)
    c: Horizontal(g67)
    c: Coincident(g68,g51)
    c: Perpendicular(g68,g51)
    c: Coincident(g69,g64)
    c: Coincident(g70,g68)
    c: Distance(g70) = 3
    c: Distance(g71) = 3
    c: Perpendicular(g68,g70)
    c: Coincident(g72,g70)
    c: Coincident(g72,g71)
    c: Block(g72)
    c: Block(g69)
    c: Block(g71)
    c: Block(g54)
    c: Block(g59)
    c: Block(g58)
    c: Block(g60)
    c: Block(g67)
    c: Block(g43)
    c: Block(g36)
    c: Block(g48)
    c: Block(g46)
    c: Block(g47)
    c: Block(g45)
    c: Block(g35)
    c: Block(g34)
    c: Block(g0)
    c: Block(g33)
    c: Block(g52)
    c: Block(g6)
    c: Block(g41)
    c: Block(g57)
    c: Block(g55)
    c: Block(g53)
    c: Block(g68)
    c: Distance(g48) = 2.76
    c: Distance(g47) = 6.6
    c: Distance(g45) = 2.36657
    c: Coincident(g73,g49)
    c: Vertical(g73)
    c: Distance(g73) = 152
    c: Coincident(g74,g53)
    c: Vertical(g74)
    c: Block(g74)
    c: Coincident(g75,g74)
    c: Horizontal(g75)
    c: Distance(g75) = 7
    c: Horizontal(g76)
    c: Distance(g76) = 7
    c: Coincident(g76,g73)
    c: Vertical(g77)
    c: Distance(g77) = 4
    c: Vertical(g78)
    c: Distance(g78) = 10
    c: Coincident(g79,g78)
    c: Coincident(g80,g77)
    c: Block(g80)
    c: Block(g79)
    c: Coincident(g81,g79)
    c: Coincident(g81,g75)
    c: Vertical(g81)
    c: Coincident(g82,g80)
    c: Coincident(g82,g76)
    c: Vertical(g82)
    c: Coincident(g83,g77)
    c: Coincident(g83,g78)
    c: Horizontal(g83)
    c: Coincident(g84,g6)
    c: Vertical(g84)
    c: Distance(g84) = 13.3
    c: Coincident(g85,g52)
    c: Vertical(g85)
    c: Block(g85)
    c: Coincident(g86,g84)
    c: Horizontal(g86)
    c: Distance(g86) = 4
    c: Coincident(g87,g85)
    c: Horizontal(g87)
    c: Distance(g87) = 4
    c: Coincident(g88,g86)
    c: Vertical(g88)
    c: Coincident(g89,g87)
    c: Vertical(g89)
    c: Distance(g88) = 4
    c: Distance(g89) = 4
    c: Coincident(g90,g88)
    c: Coincident(g90,g89)
    c: Block(g90)
    c: Block(g56)
FEATURE [Sketcher::SketchObject] Sketch005  label="middleTop"
  FullyConstrained = true
  sketch-geometry (133):
    g0: Circle CenterX=175.025 CenterY=27.0667 CenterZ=0 NormalX=0 NormalY=0 NormalZ=1 AngleXU=0 Radius=1
    g1: Circle CenterX=179.022 CenterY=24.8665 CenterZ=0 NormalX=0 NormalY=0 NormalZ=1 AngleXU=0 Radius=1
    g2: Circle CenterX=179.022 CenterY=27.0606 CenterZ=0 NormalX=0 NormalY=0 NormalZ=1 AngleXU=0 Radius=1
    g3: BSplineCurve PolesCount=3 KnotsCount=2 Degree=2 IsPeriodic=0
    g4: GeomPoint X=175.025 Y=27.0667 Z=0
    g5: GeomPoint X=179.022 Y=27.0606 Z=0
    g6: Circle CenterX=189.124 CenterY=27.0628 CenterZ=0 NormalX=0 NormalY=0 NormalZ=1 AngleXU=0 Radius=1
    g7: Circle CenterX=185.124 CenterY=24.8665 CenterZ=0 NormalX=0 NormalY=0 NormalZ=1 AngleXU=0 Radius=1
    g8: Circle CenterX=185.124 CenterY=27.0606 CenterZ=0 NormalX=0 NormalY=0 NormalZ=1 AngleXU=0 Radius=1
    g9: BSplineCurve PolesCount=3 KnotsCount=2 Degree=2 IsPeriodic=0
    g10: GeomPoint X=189.124 Y=27.0628 Z=0
    g11: GeomPoint X=185.124 Y=27.0606 Z=0
    g12: Circle CenterX=165.871 CenterY=18.1458 CenterZ=0 NormalX=0 NormalY=0 NormalZ=1 AngleXU=0 Radius=1
    g13: Circle CenterX=169.377 CenterY=16.2206 CenterZ=0 NormalX=0 NormalY=0 NormalZ=1 AngleXU=0 Radius=1
    g14: Circle CenterX=165.871 CenterY=14.2956 CenterZ=0 NormalX=0 NormalY=0 NormalZ=1 AngleXU=0 Radius=1
    g15: BSplineCurve PolesCount=3 KnotsCount=2 Degree=2 IsPeriodic=0
    g16: GeomPoint X=165.871 Y=18.1458 Z=0
    g17: GeomPoint X=165.871 Y=14.2956 Z=0
    g18: Circle CenterX=198.275 CenterY=18.1318 CenterZ=0 NormalX=0 NormalY=0 NormalZ=1 AngleXU=0 Radius=1
    g19: Circle CenterX=194.768 CenterY=16.2206 CenterZ=0 NormalX=0 NormalY=0 NormalZ=1 AngleXU=0 Radius=1
    g20: Circle CenterX=198.264 CenterY=14.2963 CenterZ=0 NormalX=0 NormalY=0 NormalZ=1 AngleXU=0 Radius=1
    g21: BSplineCurve PolesCount=3 KnotsCount=2 Degree=2 IsPeriodic=0
    g22: GeomPoint X=198.275 Y=18.1318 Z=0
    g23: GeomPoint X=198.264 Y=14.2963 Z=0
    g24: Circle CenterX=125.607 CenterY=54.1951 CenterZ=0 NormalX=0 NormalY=0 NormalZ=1 AngleXU=0 Radius=1
    g25: Circle CenterX=139.632 CenterY=46.4944 CenterZ=0 NormalX=0 NormalY=0 NormalZ=1 AngleXU=0 Radius=1
    g26: Circle CenterX=127.326 CenterY=56.7187 CenterZ=0 NormalX=0 NormalY=0 NormalZ=1 AngleXU=0 Radius=1
    g27: BSplineCurve PolesCount=3 KnotsCount=2 Degree=2 IsPeriodic=0
    g28: GeomPoint X=125.607 Y=54.1951 Z=0
    g29: GeomPoint X=127.326 Y=56.7187 Z=0
    g30: Circle CenterX=236.824 CenterY=56.7187 CenterZ=0 NormalX=0 NormalY=0 NormalZ=1 AngleXU=0 Radius=1
    g31: Circle CenterX=224.513 CenterY=46.4944 CenterZ=0 NormalX=0 NormalY=0 NormalZ=1 AngleXU=0 Radius=1
    g32: Circle CenterX=238.538 CenterY=54.1951 CenterZ=0 NormalX=0 NormalY=0 NormalZ=1 AngleXU=0 Radius=1
    g33: BSplineCurve PolesCount=3 KnotsCount=2 Degree=2 IsPeriodic=0
    g34: GeomPoint X=236.824 Y=56.7187 Z=0
    g35: GeomPoint X=238.538 Y=54.1951 Z=0
    g36: Circle CenterX=189.121 CenterY=124.221 CenterZ=0 NormalX=0 NormalY=0 NormalZ=1 AngleXU=0 Radius=1
    g37: Circle CenterX=185.124 CenterY=124.221 CenterZ=0 NormalX=0 NormalY=0 NormalZ=1 AngleXU=0 Radius=1
    g38: Circle CenterX=185.124 CenterY=120.221 CenterZ=0 NormalX=0 NormalY=0 NormalZ=1 AngleXU=0 Radius=1
    g39: BSplineCurve PolesCount=3 KnotsCount=2 Degree=2 IsPeriodic=0
    g40: GeomPoint X=189.121 Y=124.221 Z=0
    g41: GeomPoint X=185.124 Y=120.221 Z=0
    g42: Circle CenterX=175.022 CenterY=124.221 CenterZ=0 NormalX=0 NormalY=0 NormalZ=1 AngleXU=0 Radius=1
    g43: Circle CenterX=179.022 CenterY=124.221 CenterZ=0 NormalX=0 NormalY=0 NormalZ=1 AngleXU=0 Radius=1
    g44: Circle CenterX=179.022 CenterY=120.221 CenterZ=0 NormalX=0 NormalY=0 NormalZ=1 AngleXU=0 Radius=1
    g45: BSplineCurve PolesCount=3 KnotsCount=2 Degree=2 IsPeriodic=0
    g46: GeomPoint X=175.022 Y=124.221 Z=0
    g47: GeomPoint X=179.022 Y=120.221 Z=0
    g48: LineSegment StartX=232.071 StartY=124.221 StartZ=0 EndX=232.071 EndY=127.221 EndZ=0
    g49-g52: Circle x4 (B-spline internal-alignment scaffolding for g53; pole/knot coordinates omitted)
    g53: BSplineCurve PolesCount=5 KnotsCount=3 Degree=3 IsPeriodic=0
    g54: GeomPoint X=232.072 Y=133.221 Z=0
    g55: GeomPoint X=223.072 Y=130.221 Z=0
    g56: GeomPoint X=232.071 Y=127.221 Z=0
    g57-g61: Circle x5 (B-spline internal-alignment scaffolding for g62; pole/knot coordinates omitted)
    g62: BSplineCurve PolesCount=5 KnotsCount=3 Degree=3 IsPeriodic=0
    g63: GeomPoint X=132.072 Y=133.221 Z=0
    g64: GeomPoint X=141.072 Y=130.221 Z=0
    g65: GeomPoint X=132.072 Y=127.221 Z=0
    g66: ArcOfCircle CenterX=247.391 CenterY=52.0843 CenterZ=0 NormalX=0 NormalY=0 NormalZ=1 AngleXU=0 Radius=4.24264 StartAngle=4.42912 EndAngle=9.14151
    g67: LineSegment StartX=240.687 StartY=51.8263 StartZ=0 EndX=239.192 EndY=54.5542 EndZ=0
    g68: LineSegment StartX=243.575 StartY=46.5669 StartZ=0 EndX=245.072 EndY=43.8408 EndZ=0
    g69: LineSegment StartX=240.168 StartY=69.471 StartZ=0 EndX=241.708 EndY=67.6172 EndZ=0
    g70: LineSegment StartX=246.783 StartY=71.8328 StartZ=0 EndX=248.546 EndY=69.7098 EndZ=0
    g71: LineSegment StartX=245.073 StartY=63.5726 StartZ=0 EndX=243.476 EndY=65.4955 EndZ=0
    g72: LineSegment StartX=123.967 StartY=69.4706 StartZ=0 EndX=122.37 EndY=67.5474 EndZ=0
    g73: LineSegment StartX=232.072 StartY=133.221 StartZ=0 EndX=232.072 EndY=136.221 EndZ=0
    g74: LineSegment StartX=232.072 StartY=136.221 StartZ=0 EndX=132.072 EndY=136.221 EndZ=0
    g75: LineSegment StartX=132.072 StartY=136.221 StartZ=0 EndX=132.072 EndY=133.221 EndZ=0
    g76: LineSegment StartX=132.072 StartY=127.221 StartZ=0 EndX=132.072 EndY=124.221 EndZ=0
    g77: LineSegment StartX=132.072 StartY=124.221 StartZ=0 EndX=175.022 EndY=124.221 EndZ=0
    g78: LineSegment StartX=189.121 StartY=124.221 StartZ=0 EndX=232.071 EndY=124.221 EndZ=0
    g79: LineSegment StartX=185.124 StartY=120.221 StartZ=0 EndX=185.124 EndY=27.0606 EndZ=0
    g80: LineSegment StartX=189.124 StartY=27.0628 StartZ=0 EndX=240.168 EndY=69.471 EndZ=0
    g81: LineSegment StartX=241.708 StartY=67.6172 StartZ=0 EndX=246.783 EndY=71.8328 EndZ=0
    g82: LineSegment StartX=248.546 StartY=69.7098 StartZ=0 EndX=243.476 EndY=65.4955 EndZ=0
    g83: LineSegment StartX=245.073 StartY=63.5726 StartZ=0 EndX=236.824 EndY=56.7187 EndZ=0
    g84: LineSegment StartX=238.538 StartY=54.1951 StartZ=0 EndX=239.192 EndY=54.5542 EndZ=0
    g85: LineSegment StartX=240.687 StartY=51.8263 StartZ=0 EndX=243.317 EndY=53.2701 EndZ=0
    g86: LineSegment StartX=246.205 StartY=48.0108 StartZ=0 EndX=243.575 EndY=46.5669 EndZ=0
    g87: LineSegment StartX=245.072 StartY=43.8408 StartZ=0 EndX=198.275 EndY=18.1318 EndZ=0
    g88: LineSegment StartX=165.871 StartY=18.1458 StartZ=0 EndX=118.934 EndY=43.9178 EndZ=0
    g89: LineSegment StartX=118.934 StartY=43.9178 StartZ=0 EndX=120.377 EndY=46.5474 EndZ=0
    g90: LineSegment StartX=117.748 StartY=47.9913 StartZ=0 EndX=120.377 EndY=46.5474 EndZ=0
    g91: LineSegment StartX=120.635 StartY=53.2507 StartZ=0 EndX=123.265 EndY=51.8068 EndZ=0
    g92: LineSegment StartX=123.265 StartY=51.8068 StartZ=0 EndX=124.73 EndY=54.6766 EndZ=0
    g93: ArcOfCircle CenterX=116.562 CenterY=52.0649 CenterZ=0 NormalX=0 NormalY=0 NormalZ=1 AngleXU=0 Radius=4.24264 StartAngle=0.283267 EndAngle=4.99566
    g94: LineSegment StartX=124.73 StartY=54.6766 StartZ=0 EndX=125.607 EndY=54.1951 EndZ=0
    g95: LineSegment StartX=127.326 StartY=56.7187 StartZ=0 EndX=119.072 EndY=63.5741 EndZ=0
    g96: LineSegment StartX=119.072 StartY=63.5741 StartZ=0 EndX=120.669 EndY=65.4973 EndZ=0
    g97: LineSegment StartX=120.669 StartY=65.4973 StartZ=0 EndX=115.591 EndY=69.7147 EndZ=0
    g98: LineSegment StartX=115.591 StartY=69.7147 StartZ=0 EndX=117.293 EndY=71.7641 EndZ=0
    g99: LineSegment StartX=117.293 StartY=71.7641 StartZ=0 EndX=122.37 EndY=67.5474 EndZ=0
    g100: LineSegment StartX=123.967 StartY=69.4706 StartZ=0 EndX=175.025 EndY=27.0667 EndZ=0
    g101: LineSegment StartX=179.022 StartY=27.0606 StartZ=0 EndX=179.022 EndY=120.221 EndZ=0
    g102-g117: Circle x16 (B-spline internal-alignment scaffolding for g118; pole/knot coordinates omitted)
    g118: BSplineCurve PolesCount=16 KnotsCount=14 Degree=3 IsPeriodic=0
    g119-g132: GeomPoint x14 (B-spline internal-alignment scaffolding for g118; pole/knot coordinates omitted)
  constraints (180):
    c: Weight(g0) = 1
    c: Equal(g0,g1)
    c: Equal(g0,g2)
    c: InternalAlignment(g0,g3)
    c: InternalAlignment(g1,g3)
    c: InternalAlignment(g2,g3)
    c: InternalAlignment(g4,g3)
    c: InternalAlignment(g5,g3)
    c: Weight(g6) = 1
    c: Equal(g6,g7)
    c: Equal(g6,g8)
    c: InternalAlignment(g6,g9)
    c: InternalAlignment(g7,g9)
    c: InternalAlignment(g8,g9)
    c: InternalAlignment(g10,g9)
    c: InternalAlignment(g11,g9)
    c: Block(g9)
    c: Block(g3)
    c: Weight(g12) = 1
    c: Equal(g12,g13)
    c: Equal(g12,g14)
    c: InternalAlignment(g12,g15)
    c: InternalAlignment(g13,g15)
    c: InternalAlignment(g14,g15)
    c: InternalAlignment(g16,g15)
    c: InternalAlignment(g17,g15)
    c: Weight(g18) = 1
    c: Equal(g18,g19)
    c: Equal(g18,g20)
    c: InternalAlignment(g18,g21)
    c: InternalAlignment(g19,g21)
    c: InternalAlignment(g20,g21)
    c: InternalAlignment(g22,g21)
    c: InternalAlignment(g23,g21)
    c: Block(g15)
    c: Block(g21)
    c: Weight(g24) = 1
    c: Equal(g24,g25)
    c: Equal(g24,g26)
    c: InternalAlignment(g24,g27)
    c: InternalAlignment(g25,g27)
    c: InternalAlignment(g26,g27)
    c: InternalAlignment(g28,g27)
    c: InternalAlignment(g29,g27)
    c: Block(g27)
    c: Weight(g30) = 1
    c: Equal(g30,g31)
    c: Equal(g30,g32)
    c: InternalAlignment(g30,g33)
    c: InternalAlignment(g31,g33)
    c: InternalAlignment(g32,g33)
    c: InternalAlignment(g34,g33)
    c: InternalAlignment(g35,g33)
    c: Block(g33)
    c: Weight(g36) = 1
    c: Equal(g36,g37)
    c: Equal(g36,g38)
    c: InternalAlignment(g36,g39)
    c: InternalAlignment(g37,g39)
    c: InternalAlignment(g38,g39)
    c: InternalAlignment(g40,g39)
    c: InternalAlignment(g41,g39)
    c: Weight(g42) = 1
    c: Equal(g42,g43)
    c: Equal(g42,g44)
    c: InternalAlignment(g42,g45)
    c: InternalAlignment(g43,g45)
    c: InternalAlignment(g44,g45)
    c: InternalAlignment(g46,g45)
    c: InternalAlignment(g47,g45)
    c: Block(g45)
    c: Block(g39)
    c: Vertical(g48)
    c: Distance(g48) = 3
    c: Weight(g49) = 1
    c: Equal(g49,g50)
    c: Equal(g49,g51)
    c: Equal(g49,g52)
    c: Coincident(g53,g48)
    c: InternalAlignment(g49-g52 -> g53) x4
    c: InternalAlignment(g54,g53)
    c: InternalAlignment(g55,g53)
    c: InternalAlignment(g56,g53)
    c: Weight(g57) = 1
    c: Equal(g57, g58-g61) x4
    c: InternalAlignment(g57-g61 -> g62) x5
    c: InternalAlignment(g63,g62)
    c: InternalAlignment(g64,g62)
    c: InternalAlignment(g65,g62)
    c: Block(g62)
    c: Block(g67)
    c: Block(g68)
    c: Distance(g69) = 2.41
    c: Distance(g70) = 2.76
    c: Distance(g71) = 2.5
    c: Distance(g72) = 2.5
    c: Block(g66)
    c: Block(g48)
    c: Block(g53)
    c: Coincident(g73,g53)
    c: Vertical(g73)
    c: Distance(g73) = 3
    c: Coincident(g74,g73)
    c: Horizontal(g74)
    c: Distance(g74) = 100
    c: Coincident(g75,g74)
    c: Coincident(g75,g62)
    c: Vertical(g75)
    c: Distance(g75) = 3
    c: Coincident(g76,g62)
    c: Vertical(g76)
    c: Distance(g76) = 3
    c: Coincident(g77,g76)
    c: Coincident(g77,g45)
    c: Horizontal(g77)
    c: Distance(g77) = 42.95
    c: Coincident(g78,g39)
    c: Coincident(g78,g48)
    c: Horizontal(g78)
    c: Distance(g78) = 42.95
    c: Coincident(g79,g39)
    c: Coincident(g79,g9)
    c: Vertical(g79)
    c: Distance(g79) = 93.16
    c: Coincident(g80,g9)
    c: Coincident(g80,g69)
    c: Angle(g80) = 0.693245
    c: Block(g80)
    c: Coincident(g81,g69)
    c: Coincident(g81,g70)
    c: Block(g81)
    c: Coincident(g82,g70)
    c: Coincident(g82,g71)
    c: Block(g82)
    c: Coincident(g83,g71)
    c: Coincident(g83,g33)
    c: Block(g71)
    c: Coincident(g84,g33)
    c: Coincident(g84,g67)
    c: Coincident(g85,g67)
    c: Coincident(g85,g66)
    c: Coincident(g86,g66)
    c: Coincident(g86,g68)
    c: Coincident(g87,g68)
    c: Coincident(g87,g21)
    c: Coincident(g88,g15)
    c: Coincident(g89,g88)
    c: Block(g89)
    c: Coincident(g90,g89)
    c: Block(g90)
    c: Block(g91)
    c: Coincident(g92,g91)
    c: Block(g92)
    c: Coincident(g93,g91)
    c: Coincident(g93,g90)
    c: Block(g93)
    c: Coincident(g94,g92)
    c: Coincident(g94,g27)
    c: Coincident(g95,g27)
    c: Block(g95)
    c: Coincident(g96,g95)
    c: Coincident(g97,g96)
    c: Coincident(g98,g97)
    c: Coincident(g99,g98)
    c: Coincident(g99,g72)
    c: Block(g98)
    c: Block(g96)
    c: Block(g72)
    c: Coincident(g100,g72)
    c: Coincident(g100,g3)
    c: Coincident(g101,g3)
    c: Coincident(g101,g45)
    c: Vertical(g101)
    c: Coincident(g118,g21)
    c: Weight(g102) = 1
    c: Equal(g102, g103-g117) x15
    c: Coincident(g118,g15)
    c: InternalAlignment(g102-g117 -> g118) x16
    c: InternalAlignment(g119-g132 -> g118) x14
    c: Block(g118)
FEATURE [Sketcher::SketchObject] Sketch006  label="leftSideTop"
  FullyConstrained = true
  sketch-geometry (99):
    g0: Circle CenterX=61.1495 CenterY=111.695 CenterZ=0 NormalX=0 NormalY=0 NormalZ=1 AngleXU=0 Radius=1
    g1: Circle CenterX=58.0728 CenterY=114.251 CenterZ=0 NormalX=0 NormalY=0 NormalZ=1 AngleXU=0 Radius=1
    g2: Circle CenterX=58.0728 CenterY=110.251 CenterZ=0 NormalX=0 NormalY=0 NormalZ=1 AngleXU=0 Radius=1
    g3: BSplineCurve PolesCount=3 KnotsCount=2 Degree=2 IsPeriodic=0
    g4: GeomPoint X=61.1495 Y=111.695 Z=0
    g5: GeomPoint X=58.0728 Y=110.251 Z=0
    g6: Circle CenterX=61.5791 CenterY=89.3511 CenterZ=0 NormalX=0 NormalY=0 NormalZ=1 AngleXU=0 Radius=1
    g7: Circle CenterX=58.0728 CenterY=91.2763 CenterZ=0 NormalX=0 NormalY=0 NormalZ=1 AngleXU=0 Radius=1
    g8: Circle CenterX=58.0728 CenterY=95.2763 CenterZ=0 NormalX=0 NormalY=0 NormalZ=1 AngleXU=0 Radius=1
    g9: BSplineCurve PolesCount=3 KnotsCount=2 Degree=2 IsPeriodic=0
    g10: GeomPoint X=61.5791 Y=89.3511 Z=0
    g11: GeomPoint X=58.0728 Y=95.2763 Z=0
    g12: Circle CenterX=62.0728 CenterY=124.221 CenterZ=0 NormalX=0 NormalY=0 NormalZ=1 AngleXU=0 Radius=1
    g13: Circle CenterX=58.0728 CenterY=124.221 CenterZ=0 NormalX=0 NormalY=0 NormalZ=1 AngleXU=0 Radius=1
    g14: Circle CenterX=61.1496 CenterY=121.665 CenterZ=0 NormalX=0 NormalY=0 NormalZ=1 AngleXU=0 Radius=1
    g15: BSplineCurve PolesCount=3 KnotsCount=2 Degree=2 IsPeriodic=0
    g16: GeomPoint X=62.0728 Y=124.221 Z=0
    g17: GeomPoint X=61.1496 Y=121.665 Z=0
    g18: Circle CenterX=61.5791 CenterY=75.4095 CenterZ=0 NormalX=0 NormalY=0 NormalZ=1 AngleXU=0 Radius=1
    g19: Circle CenterX=58.0728 CenterY=77.3346 CenterZ=0 NormalX=0 NormalY=0 NormalZ=1 AngleXU=0 Radius=1
    g20: Circle CenterX=58.0728 CenterY=73.3346 CenterZ=0 NormalX=0 NormalY=0 NormalZ=1 AngleXU=0 Radius=1
    g21: BSplineCurve PolesCount=3 KnotsCount=2 Degree=2 IsPeriodic=0
    g22: GeomPoint X=61.5791 Y=75.4095 Z=0
    g23: GeomPoint X=58.0728 Y=73.3346 Z=0
    g24: Circle CenterX=2.07281 CenterY=124.221 CenterZ=0 NormalX=0 NormalY=0 NormalZ=1 AngleXU=0 Radius=1
    g25: Circle CenterX=1.57905 CenterY=122.295 CenterZ=0 NormalX=0 NormalY=0 NormalZ=1 AngleXU=0 Radius=1
    g26: BSplineCurve PolesCount=3 KnotsCount=2 Degree=2 IsPeriodic=0
    g27: GeomPoint X=2.07281 Y=124.221 Z=0
    g28: GeomPoint X=1.57905 Y=122.295 Z=0
    g29: Circle CenterX=46.0728 CenterY=124.221 CenterZ=0 NormalX=0 NormalY=0 NormalZ=1 AngleXU=0 Radius=1
    g30: Circle CenterX=46.0728 CenterY=120.221 CenterZ=0 NormalX=0 NormalY=0 NormalZ=1 AngleXU=0 Radius=1
    g31: BSplineCurve PolesCount=3 KnotsCount=2 Degree=2 IsPeriodic=0
    g32: GeomPoint X=42.0728 Y=124.221 Z=0
    g33: GeomPoint X=46.0728 Y=120.221 Z=0
    g34: Circle CenterX=46.0728 CenterY=109.865 CenterZ=0 NormalX=0 NormalY=0 NormalZ=1 AngleXU=0 Radius=1
    g35: Circle CenterX=46.0728 CenterY=105.865 CenterZ=0 NormalX=0 NormalY=0 NormalZ=1 AngleXU=0 Radius=1
    g36: Circle CenterX=42.0728 CenterY=105.865 CenterZ=0 NormalX=0 NormalY=0 NormalZ=1 AngleXU=0 Radius=1
    g37: BSplineCurve PolesCount=3 KnotsCount=2 Degree=2 IsPeriodic=0
    g38: GeomPoint X=46.0728 Y=109.865 Z=0
    g39: GeomPoint X=42.0728 Y=105.865 Z=0
    g40: Circle CenterX=35.5028 CenterY=105.865 CenterZ=0 NormalX=0 NormalY=0 NormalZ=1 AngleXU=0 Radius=1
    g41: Circle CenterX=31.5028 CenterY=105.865 CenterZ=0 NormalX=0 NormalY=0 NormalZ=1 AngleXU=0 Radius=1
    g42: Circle CenterX=27.9965 CenterY=107.79 CenterZ=0 NormalX=0 NormalY=0 NormalZ=1 AngleXU=0 Radius=1
    g43: BSplineCurve PolesCount=3 KnotsCount=2 Degree=2 IsPeriodic=0
    g44: GeomPoint X=35.5028 Y=105.865 Z=0
    g45: GeomPoint X=27.9965 Y=107.79 Z=0
    g46-g50: Circle x5 (B-spline internal-alignment scaffolding for g51; pole/knot coordinates omitted)
    g51: BSplineCurve PolesCount=5 KnotsCount=3 Degree=3 IsPeriodic=0
    g52: GeomPoint X=132.072 Y=133.221 Z=0
    g53: GeomPoint X=141.072 Y=130.221 Z=0
    g54: GeomPoint X=132.072 Y=127.221 Z=0
    g55: ArcOfCircle CenterX=116.562 CenterY=52.0649 CenterZ=0 NormalX=0 NormalY=0 NormalZ=1 AngleXU=0 Radius=4.24264 StartAngle=0.283268 EndAngle=4.99566
    g56: LineSegment StartX=123.967 StartY=69.4706 StartZ=0 EndX=122.37 EndY=67.5474 EndZ=0
    g57: LineSegment StartX=117.293 StartY=71.7641 StartZ=0 EndX=115.591 EndY=69.7147 EndZ=0
    g58: LineSegment StartX=120.669 StartY=65.4973 StartZ=0 EndX=119.072 EndY=63.5741 EndZ=0
    g59: LineSegment StartX=124.73 StartY=54.6766 StartZ=0 EndX=123.265 EndY=51.8068 EndZ=0
    g60: LineSegment StartX=120.377 StartY=46.5474 StartZ=0 EndX=118.934 EndY=43.9178 EndZ=0
    g61: BSplineCurve PolesCount=3 KnotsCount=2 Degree=2 IsPeriodic=0
    g62: BSplineCurve PolesCount=3 KnotsCount=2 Degree=2 IsPeriodic=0
    g63: LineSegment StartX=61.5791 StartY=75.4095 StartZ=0 EndX=118.934 EndY=43.9178 EndZ=0
    g64: LineSegment StartX=117.748 StartY=47.9913 StartZ=0 EndX=120.377 EndY=46.5474 EndZ=0
    g65: LineSegment StartX=120.635 StartY=53.2507 StartZ=0 EndX=123.265 EndY=51.8068 EndZ=0
    g66: LineSegment StartX=124.73 StartY=54.6766 StartZ=0 EndX=61.5791 EndY=89.3511 EndZ=0
    g67: LineSegment StartX=58.0728 StartY=95.2763 StartZ=0 EndX=58.0728 EndY=110.251 EndZ=0
    g68: LineSegment StartX=61.1495 StartY=111.695 StartZ=0 EndX=119.072 EndY=63.5741 EndZ=0
    g69: LineSegment StartX=120.669 StartY=65.4973 StartZ=0 EndX=115.591 EndY=69.7147 EndZ=0
    g70: LineSegment StartX=117.293 StartY=71.7641 StartZ=0 EndX=122.37 EndY=67.5474 EndZ=0
    g71: LineSegment StartX=123.967 StartY=69.4706 StartZ=0 EndX=61.1496 EndY=121.665 EndZ=0
    g72: LineSegment StartX=62.0728 StartY=124.221 StartZ=0 EndX=132.072 EndY=124.221 EndZ=0
    g73: LineSegment StartX=132.072 StartY=127.221 StartZ=0 EndX=132.072 EndY=124.221 EndZ=0
    g74: LineSegment StartX=132.072 StartY=133.221 StartZ=0 EndX=132.072 EndY=136.221 EndZ=0
    g75: LineSegment StartX=132.072 StartY=136.221 StartZ=0 EndX=-42.9272 EndY=136.221 EndZ=0
    g76: LineSegment StartX=2.07281 StartY=124.221 StartZ=0 EndX=42.0728 EndY=124.221 EndZ=0
    g77: LineSegment StartX=46.0728 StartY=120.221 StartZ=0 EndX=46.0728 EndY=109.865 EndZ=0
    g78: LineSegment StartX=42.0728 StartY=105.865 StartZ=0 EndX=35.5028 EndY=105.865 EndZ=0
    g79: LineSegment StartX=27.9965 StartY=107.79 StartZ=0 EndX=1.57905 EndY=122.295 EndZ=0
    g80: LineSegment StartX=-6.92718 StartY=76.4095 StartZ=0 EndX=42.0728 EndY=76.4095 EndZ=0
    g81: LineSegment StartX=-17.9272 StartY=48.2206 StartZ=0 EndX=-17.9272 EndY=58.2206 EndZ=0
    g82: LineSegment StartX=-35.9272 StartY=48.2206 StartZ=0 EndX=-35.9272 EndY=52.2206 EndZ=0
    g83: LineSegment StartX=-29.9272 StartY=48.2206 StartZ=0 EndX=-29.9272 EndY=52.2206 EndZ=0
    g84: LineSegment StartX=-23.9272 StartY=48.2206 StartZ=0 EndX=-23.9272 EndY=58.2206 EndZ=0
    g85: ArcOfCircle CenterX=-32.9272 CenterY=55.2206 CenterZ=0 NormalX=0 NormalY=0 NormalZ=1 AngleXU=0 Radius=4.24264 StartAngle=5.49779 EndAngle=10.2102
    g86: ArcOfCircle CenterX=-20.9272 CenterY=61.2206 CenterZ=0 NormalX=0 NormalY=0 NormalZ=1 AngleXU=0 Radius=4.24264 StartAngle=5.49779 EndAngle=10.2102
    g87: LineSegment StartX=-10.9272 StartY=48.2206 StartZ=0 EndX=-10.9272 EndY=72.4095 EndZ=0
    g88: LineSegment StartX=-42.9272 StartY=48.2206 StartZ=0 EndX=-42.9272 EndY=136.221 EndZ=0
    g89: LineSegment StartX=46.0728 StartY=72.4095 StartZ=0 EndX=46.0728 EndY=-27.5905 EndZ=0
    g90: LineSegment StartX=58.0728 StartY=-27.5905 StartZ=0 EndX=58.0728 EndY=73.3346 EndZ=0
    g91: LineSegment StartX=50.0728 StartY=-27.5905 StartZ=0 EndX=50.0728 EndY=-31.5905 EndZ=0
    g92: LineSegment StartX=54.0728 StartY=-27.5905 StartZ=0 EndX=54.0728 EndY=-31.5905 EndZ=0
    g93: ArcOfCircle CenterX=52.0728 CenterY=-33.5905 CenterZ=0 NormalX=0 NormalY=0 NormalZ=1 AngleXU=0 Radius=2.82843 StartAngle=2.35619 EndAngle=7.06858
    g94: LineSegment StartX=46.0728 StartY=-27.5905 StartZ=0 EndX=50.0728 EndY=-27.5905 EndZ=0
    g95: LineSegment StartX=54.0728 StartY=-27.5905 StartZ=0 EndX=58.0728 EndY=-27.5905 EndZ=0
    g96: LineSegment StartX=-17.9272 StartY=48.2206 StartZ=0 EndX=-10.9272 EndY=48.2206 EndZ=0
    g97: LineSegment StartX=-29.9272 StartY=48.2206 StartZ=0 EndX=-23.9272 EndY=48.2206 EndZ=0
    g98: LineSegment StartX=-42.9272 StartY=48.2206 StartZ=0 EndX=-35.9272 EndY=48.2206 EndZ=0
  constraints (172):
    c: Weight(g0) = 1
    c: Equal(g0,g1)
    c: Equal(g0,g2)
    c: InternalAlignment(g0,g3)
    c: InternalAlignment(g1,g3)
    c: InternalAlignment(g2,g3)
    c: InternalAlignment(g4,g3)
    c: InternalAlignment(g5,g3)
    c: Weight(g6) = 1
    c: Equal(g6,g7)
    c: Equal(g6,g8)
    c: InternalAlignment(g6,g9)
    c: InternalAlignment(g7,g9)
    c: InternalAlignment(g8,g9)
    c: InternalAlignment(g10,g9)
    c: InternalAlignment(g11,g9)
    c: Block(g3)
    c: Block(g9)
    c: Weight(g12) = 1
    c: Equal(g12,g13)
    c: Equal(g12,g14)
    c: InternalAlignment(g12,g15)
    c: InternalAlignment(g13,g15)
    c: InternalAlignment(g14,g15)
    c: InternalAlignment(g16,g15)
    c: InternalAlignment(g17,g15)
    c: Block(g15)
    c: Weight(g18) = 1
    c: Equal(g18,g19)
    c: Equal(g18,g20)
    c: InternalAlignment(g18,g21)
    c: InternalAlignment(g19,g21)
    c: InternalAlignment(g20,g21)
    c: InternalAlignment(g22,g21)
    c: InternalAlignment(g23,g21)
    c: Block(g21)
    c: Weight(g24) = 1
    c: Equal(g24,g25)
    c: InternalAlignment(g24,g26)
    c: InternalAlignment(g25,g26)
    c: InternalAlignment(g27,g26)
    c: InternalAlignment(g28,g26)
    c: InternalAlignment(g29,g31)
    c: InternalAlignment(g30,g31)
    c: InternalAlignment(g32,g31)
    c: InternalAlignment(g33,g31)
    c: Weight(g34) = 1
    c: Equal(g34,g35)
    c: Equal(g34,g36)
    c: InternalAlignment(g34,g37)
    c: InternalAlignment(g35,g37)
    c: InternalAlignment(g36,g37)
    c: InternalAlignment(g38,g37)
    c: InternalAlignment(g39,g37)
    c: Equal(g40,g41)
    c: Equal(g40,g42)
    c: InternalAlignment(g40,g43)
    c: InternalAlignment(g41,g43)
    c: InternalAlignment(g42,g43)
    c: InternalAlignment(g44,g43)
    c: InternalAlignment(g45,g43)
    c: Block(g31)
    c: Block(g37)
    c: Block(g43)
    c: Block(g26)
    c: Weight(g46) = 1
    c: Equal(g46, g47-g50) x4
    c: InternalAlignment(g46-g50 -> g51) x5
    c: InternalAlignment(g52,g51)
    c: InternalAlignment(g53,g51)
    c: InternalAlignment(g54,g51)
    c: Block(g51)
    c: Block(g55)
    c: Block(g56)
    c: Block(g57)
    c: Block(g58)
    c: Block(g59)
    c: Block(g60)
    c: Block(g61)
    c: Block(g62)
    c: Coincident(g90,g21)
    c: Coincident(g63,g21)
    c: Coincident(g63,g60)
    c: Coincident(g64,g55)
    c: Coincident(g64,g60)
    c: Coincident(g65,g55)
    c: Coincident(g65,g59)
    c: Coincident(g66,g59)
    c: Coincident(g66,g9)
    c: Coincident(g67,g9)
    c: Coincident(g67,g3)
    c: Vertical(g67)
    c: Coincident(g68,g3)
    c: Coincident(g68,g58)
    c: Coincident(g69,g58)
    c: Coincident(g69,g57)
    c: Coincident(g70,g57)
    c: Coincident(g70,g56)
    c: Coincident(g71,g56)
    c: Coincident(g71,g15)
    c: Coincident(g72,g15)
    c: Horizontal(g72)
    c: Coincident(g73,g51)
    c: Coincident(g73,g72)
    c: Vertical(g73)
    c: Coincident(g74,g51)
    c: Vertical(g74)
    c: Coincident(g75,g74)
    c: Horizontal(g75)
    c: Coincident(g76,g26)
    c: Coincident(g76,g31)
    c: Horizontal(g76)
    c: Coincident(g77,g31)
    c: Coincident(g77,g37)
    c: Vertical(g77)
    c: Coincident(g78,g37)
    c: Coincident(g78,g43)
    c: Horizontal(g78)
    c: Coincident(g79,g43)
    c: Coincident(g79,g26)
    c: Coincident(g80,g62)
    c: Coincident(g80,g61)
    c: Horizontal(g80)
    c: Vertical(g81)
    c: Distance(g81) = 10
    c: Vertical(g82)
    c: Distance(g82) = 4
    c: Vertical(g83)
    c: Distance(g83) = 4
    c: Vertical(g84)
    c: Distance(g84) = 10
    c: Coincident(g85,g83)
    c: Coincident(g85,g82)
    c: Block(g85)
    c: Coincident(g86,g84)
    c: Coincident(g86,g81)
    c: Block(g86)
    c: Coincident(g87,g62)
    c: Vertical(g87)
    c: Coincident(g88,g75)
    c: Vertical(g88)
    c: Block(g75)
    c: Coincident(g89,g61)
    c: Vertical(g89)
    c: Distance(g89) = 100
    c: Block(g90)
    c: Vertical(g91)
    c: Distance(g91) = 4
    c: Vertical(g92)
    c: Distance(g92) = 4
    c: Coincident(g93,g91)
    c: Coincident(g93,g92)
    c: Block(g93)
    c: Coincident(g94,g89)
    c: Coincident(g94,g91)
    c: Horizontal(g94)
    c: Distance(g94) = 4
    c: Coincident(g95,g92)
    c: Coincident(g95,g90)
    c: Horizontal(g95)
    c: Distance(g95) = 4
    c: Block(g87)
    c: Block(g88)
    c: Coincident(g96,g81)
    c: Coincident(g96,g87)
    c: Horizontal(g96)
    c: Coincident(g97,g83)
    c: Coincident(g97,g84)
    c: Horizontal(g97)
    c: Coincident(g98,g88)
    c: Coincident(g98,g82)
    c: Horizontal(g98)
FEATURE [Sketcher::SketchObject] Sketch007  label="leftSideBottom"
  FullyConstrained = true
  sketch-geometry (92):
    g0: ArcOfCircle CenterX=-26.9272 CenterY=-83.7794 CenterZ=0 NormalX=0 NormalY=0 NormalZ=1 AngleXU=0 Radius=8 StartAngle=3.14159 EndAngle=6.28319
    g1: Circle CenterX=61.5791 CenterY=-56.9099 CenterZ=0 NormalX=0 NormalY=0 NormalZ=1 AngleXU=0 Radius=1
    g2: Circle CenterX=58.0728 CenterY=-58.8351 CenterZ=0 NormalX=0 NormalY=0 NormalZ=1 AngleXU=0 Radius=1
    g3: Circle CenterX=58.0728 CenterY=-62.8351 CenterZ=0 NormalX=0 NormalY=0 NormalZ=1 AngleXU=0 Radius=1
    g4: BSplineCurve PolesCount=3 KnotsCount=2 Degree=2 IsPeriodic=0
    g5: GeomPoint X=61.5791 Y=-56.9099 Z=0
    g6: GeomPoint X=58.0728 Y=-62.8351 Z=0
    g7: Circle CenterX=58.0728 CenterY=-77.8102 CenterZ=0 NormalX=0 NormalY=0 NormalZ=1 AngleXU=0 Radius=1
    g8: Circle CenterX=58.0728 CenterY=-81.8102 CenterZ=0 NormalX=0 NormalY=0 NormalZ=1 AngleXU=0 Radius=1
    g9: Circle CenterX=61.1496 CenterY=-79.2541 CenterZ=0 NormalX=0 NormalY=0 NormalZ=1 AngleXU=0 Radius=1
    g10: BSplineCurve PolesCount=3 KnotsCount=2 Degree=2 IsPeriodic=0
    g11: GeomPoint X=58.0728 Y=-77.8102 Z=0
    g12: GeomPoint X=61.1496 Y=-79.2541 Z=0
    g13: Circle CenterX=61.6457 CenterY=-88.8112 CenterZ=0 NormalX=0 NormalY=0 NormalZ=1 AngleXU=0 Radius=1
    g14: Circle CenterX=58.0728 CenterY=-91.7794 CenterZ=0 NormalX=0 NormalY=0 NormalZ=1 AngleXU=0 Radius=1
    g15: Circle CenterX=63.9135 CenterY=-91.8014 CenterZ=0 NormalX=0 NormalY=0 NormalZ=1 AngleXU=0 Radius=1
    g16: BSplineCurve PolesCount=3 KnotsCount=2 Degree=2 IsPeriodic=0
    g17: GeomPoint X=61.6457 Y=-88.8112 Z=0
    g18: GeomPoint X=63.9135 Y=-91.8014 Z=0
    g19: Circle CenterX=58.0728 CenterY=-40.8935 CenterZ=0 NormalX=0 NormalY=0 NormalZ=1 AngleXU=0 Radius=1
    g20: Circle CenterX=58.0728 CenterY=-44.8935 CenterZ=0 NormalX=0 NormalY=0 NormalZ=1 AngleXU=0 Radius=1
    g21: Circle CenterX=61.5791 CenterY=-42.9683 CenterZ=0 NormalX=0 NormalY=0 NormalZ=1 AngleXU=0 Radius=1
    g22: BSplineCurve PolesCount=3 KnotsCount=2 Degree=2 IsPeriodic=0
    g23: GeomPoint X=58.0728 Y=-40.8935 Z=0
    g24: GeomPoint X=61.5791 Y=-42.9683 Z=0
    g25: Circle CenterX=42.5666 CenterY=-67.3492 CenterZ=0 NormalX=0 NormalY=0 NormalZ=1 AngleXU=0 Radius=1
    g26: Circle CenterX=46.0728 CenterY=-65.424 CenterZ=0 NormalX=0 NormalY=0 NormalZ=1 AngleXU=0 Radius=1
    g27: Circle CenterX=46.0728 CenterY=-69.424 CenterZ=0 NormalX=0 NormalY=0 NormalZ=1 AngleXU=0 Radius=1
    g28: BSplineCurve PolesCount=3 KnotsCount=2 Degree=2 IsPeriodic=0
    g29: GeomPoint X=42.5666 Y=-67.3492 Z=0
    g30: GeomPoint X=46.0728 Y=-69.424 Z=0
    g31: Circle CenterX=2.07281 CenterY=-91.7794 CenterZ=0 NormalX=0 NormalY=0 NormalZ=1 AngleXU=0 Radius=1
    g32: Circle CenterX=-1.92719 CenterY=-91.7794 CenterZ=0 NormalX=0 NormalY=0 NormalZ=1 AngleXU=0 Radius=1
    g33: Circle CenterX=1.57905 CenterY=-89.8542 CenterZ=0 NormalX=0 NormalY=0 NormalZ=1 AngleXU=0 Radius=1
    g34: BSplineCurve PolesCount=3 KnotsCount=2 Degree=2 IsPeriodic=0
    g35: GeomPoint X=2.07281 Y=-91.7794 Z=0
    g36: GeomPoint X=1.57905 Y=-89.8542 Z=0
    g37: ArcOfCircle CenterX=-26.9272 CenterY=22.1087 CenterZ=0 NormalX=0 NormalY=0 NormalZ=1 AngleXU=0 Radius=4 StartAngle=5e-16 EndAngle=3.14159
    g38: Circle CenterX=-10.9272 CenterY=-78.7794 CenterZ=0 NormalX=0 NormalY=0 NormalZ=1 AngleXU=0 Radius=1
    g39: Circle CenterX=-10.9272 CenterY=-82.7794 CenterZ=0 NormalX=0 NormalY=0 NormalZ=1 AngleXU=0 Radius=1
    g40: Circle CenterX=-7.42095 CenterY=-80.8542 CenterZ=0 NormalX=0 NormalY=0 NormalZ=1 AngleXU=0 Radius=1
    g41: BSplineCurve PolesCount=3 KnotsCount=2 Degree=2 IsPeriodic=0
    g42: GeomPoint X=-10.9272 Y=-78.7794 Z=0
    g43: GeomPoint X=-7.42095 Y=-80.8542 Z=0
    g44: BSplineCurve PolesCount=3 KnotsCount=2 Degree=2 IsPeriodic=0
    g45: GeomPoint X=42.5666 Y=-53.4075 Z=0
    g46: GeomPoint X=46.0728 Y=-47.4823 Z=0
    g47: BSplineCurve PolesCount=5 KnotsCount=3 Degree=3 IsPeriodic=0
    g48: LineSegment StartX=124.814 StartY=-22.1885 StartZ=0 EndX=123.265 EndY=-19.3655 EndZ=0
    g49: ArcOfCircle CenterX=116.562 CenterY=-19.6236 CenterZ=0 NormalX=0 NormalY=0 NormalZ=1 AngleXU=0 Radius=4.24264 StartAngle=1.28753 EndAngle=6.00037
    g50: LineSegment StartX=-30.9272 StartY=22.1087 StartZ=0 EndX=-34.9272 EndY=-83.7794 EndZ=0
    g51: LineSegment StartX=-22.9272 StartY=22.1087 StartZ=0 EndX=-18.9272 EndY=-83.7794 EndZ=0
    g52: LineSegment StartX=118.934 StartY=-11.4765 StartZ=0 EndX=120.377 EndY=-14.1062 EndZ=0
    g53: LineSegment StartX=118.86 StartY=-31.3104 StartZ=0 EndX=120.377 EndY=-33.1447 EndZ=0
    g54: LineSegment StartX=115.291 StartY=-37.3514 StartZ=0 EndX=117.05 EndY=-39.4781 EndZ=0
    g55: LineSegment StartX=122.136 StartY=-35.2714 StartZ=0 EndX=123.656 EndY=-37.1092 EndZ=0
    g56: BSplineCurve PolesCount=3 KnotsCount=2 Degree=2 IsPeriodic=0
    g57: LineSegment StartX=132.072 StartY=-100.779 StartZ=0 EndX=132.072 EndY=-103.779 EndZ=0
    g58: LineSegment StartX=132.072 StartY=-91.8014 StartZ=0 EndX=132.072 EndY=-94.7791 EndZ=0
    g59: LineSegment StartX=63.9135 StartY=-91.8014 StartZ=0 EndX=132.072 EndY=-91.8014 EndZ=0
    g60: LineSegment StartX=61.6457 StartY=-88.8112 StartZ=0 EndX=123.656 EndY=-37.1092 EndZ=0
    g61: LineSegment StartX=122.136 StartY=-35.2714 StartZ=0 EndX=117.05 EndY=-39.4781 EndZ=0
    g62: LineSegment StartX=115.291 StartY=-37.3514 StartZ=0 EndX=120.377 EndY=-33.1447 EndZ=0
    g63: LineSegment StartX=118.86 StartY=-31.3104 StartZ=0 EndX=61.1496 EndY=-79.2541 EndZ=0
    g64: LineSegment StartX=58.0728 StartY=-77.8102 StartZ=0 EndX=58.0728 EndY=-62.8351 EndZ=0
    g65: LineSegment StartX=61.5791 StartY=-56.9099 StartZ=0 EndX=124.814 EndY=-22.1885 EndZ=0
    g66: LineSegment StartX=120.636 StartY=-20.8076 StartZ=0 EndX=123.265 EndY=-19.3655 EndZ=0
    g67: LineSegment StartX=117.748 StartY=-15.55 StartZ=0 EndX=120.377 EndY=-14.1062 EndZ=0
    g68: LineSegment StartX=118.934 StartY=-11.4765 StartZ=0 EndX=61.5791 EndY=-42.9683 EndZ=0
    g69: LineSegment StartX=-42.9272 StartY=-103.779 StartZ=0 EndX=132.072 EndY=-103.779 EndZ=0
    g70: LineSegment StartX=42.5666 StartY=-53.4075 StartZ=0 EndX=-7.42095 EndY=-80.8542 EndZ=0
    g71: LineSegment StartX=-10.9272 StartY=-78.7794 StartZ=0 EndX=-10.9272 EndY=48.2206 EndZ=0
    g72: LineSegment StartX=2.07281 StartY=-91.7794 StartZ=0 EndX=42.0728 EndY=-91.7794 EndZ=0
    g73: LineSegment StartX=46.0728 StartY=-87.7794 StartZ=0 EndX=46.0728 EndY=-69.424 EndZ=0
    g74: LineSegment StartX=42.5666 StartY=-67.3492 StartZ=0 EndX=1.57905 EndY=-89.8542 EndZ=0
    g75: LineSegment StartX=-42.9272 StartY=-103.779 StartZ=0 EndX=-42.9272 EndY=48.2206 EndZ=0
    g76: LineSegment StartX=-17.9272 StartY=48.2206 StartZ=0 EndX=-17.9272 EndY=58.2206 EndZ=0
    g77: LineSegment StartX=-35.9272 StartY=48.2206 StartZ=0 EndX=-35.9272 EndY=52.2206 EndZ=0
    g78: LineSegment StartX=-29.9272 StartY=48.2206 StartZ=0 EndX=-29.9272 EndY=52.2206 EndZ=0
    g79: LineSegment StartX=-23.9272 StartY=48.2206 StartZ=0 EndX=-23.9272 EndY=58.2206 EndZ=0
    g80: ArcOfCircle CenterX=-32.9272 CenterY=55.2206 CenterZ=0 NormalX=0 NormalY=0 NormalZ=1 AngleXU=0 Radius=4.24264 StartAngle=5.49779 EndAngle=10.2102
    g81: ArcOfCircle CenterX=-20.9272 CenterY=61.2206 CenterZ=0 NormalX=0 NormalY=0 NormalZ=1 AngleXU=0 Radius=4.24264 StartAngle=5.49779 EndAngle=10.2102
    g82: LineSegment StartX=-17.9272 StartY=48.2206 StartZ=0 EndX=-10.9272 EndY=48.2206 EndZ=0
    g83: LineSegment StartX=-42.9272 StartY=48.2206 StartZ=0 EndX=-35.9272 EndY=48.2206 EndZ=0
    g84: LineSegment StartX=50.0728 StartY=-27.5905 StartZ=0 EndX=50.0728 EndY=-31.5905 EndZ=0
    g85: LineSegment StartX=54.0728 StartY=-27.5905 StartZ=0 EndX=54.0728 EndY=-31.5905 EndZ=0
    g86: ArcOfCircle CenterX=52.0728 CenterY=-33.5905 CenterZ=0 NormalX=0 NormalY=0 NormalZ=1 AngleXU=0 Radius=2.82843 StartAngle=2.35619 EndAngle=7.06858
    g87: LineSegment StartX=46.0728 StartY=-27.5905 StartZ=0 EndX=50.0728 EndY=-27.5905 EndZ=0
    g88: LineSegment StartX=54.0728 StartY=-27.5905 StartZ=0 EndX=58.0728 EndY=-27.5905 EndZ=0
    g89: LineSegment StartX=46.0728 StartY=-27.5905 StartZ=0 EndX=46.0728 EndY=-47.4823 EndZ=0
    g90: LineSegment StartX=58.0728 StartY=-27.5905 StartZ=0 EndX=58.0728 EndY=-40.8935 EndZ=0
    g91: LineSegment StartX=-29.9272 StartY=48.2206 StartZ=0 EndX=-23.9272 EndY=48.2206 EndZ=0
  constraints (170):
    c: Weight(g1) = 1
    c: Equal(g1,g2)
    c: Equal(g1,g3)
    c: InternalAlignment(g1,g4)
    c: InternalAlignment(g2,g4)
    c: InternalAlignment(g3,g4)
    c: InternalAlignment(g5,g4)
    c: InternalAlignment(g6,g4)
    c: Weight(g7) = 1
    c: Equal(g7,g8)
    c: Equal(g7,g9)
    c: InternalAlignment(g7,g10)
    c: InternalAlignment(g8,g10)
    c: InternalAlignment(g9,g10)
    c: InternalAlignment(g11,g10)
    c: InternalAlignment(g12,g10)
    c: Block(g4)
    c: Block(g10)
    c: Weight(g13) = 1
    c: Equal(g13,g14)
    c: Equal(g13,g15)
    c: InternalAlignment(g13,g16)
    c: InternalAlignment(g14,g16)
    c: InternalAlignment(g15,g16)
    c: InternalAlignment(g17,g16)
    c: InternalAlignment(g18,g16)
    c: Block(g16)
    c: Weight(g19) = 1
    c: Equal(g19,g20)
    c: Equal(g19,g21)
    c: InternalAlignment(g19,g22)
    c: InternalAlignment(g20,g22)
    c: InternalAlignment(g21,g22)
    c: InternalAlignment(g23,g22)
    c: InternalAlignment(g24,g22)
    c: Block(g22)
    c: Weight(g25) = 1
    c: Equal(g25,g26)
    c: Equal(g25,g27)
    c: InternalAlignment(g25,g28)
    c: InternalAlignment(g26,g28)
    c: InternalAlignment(g27,g28)
    c: InternalAlignment(g29,g28)
    c: InternalAlignment(g30,g28)
    c: Weight(g31) = 1
    c: Equal(g31,g32)
    c: Equal(g31,g33)
    c: InternalAlignment(g31,g34)
    c: InternalAlignment(g32,g34)
    c: InternalAlignment(g33,g34)
    c: InternalAlignment(g35,g34)
    c: InternalAlignment(g36,g34)
    c: Block(g34)
    c: Block(g28)
    c: Block(g37)
    c: Block(g0)
    c: Weight(g38) = 1
    c: Equal(g38,g40)
    c: InternalAlignment(g38,g41)
    c: InternalAlignment(g39,g41)
    c: InternalAlignment(g40,g41)
    c: InternalAlignment(g42,g41)
    c: InternalAlignment(g43,g41)
    c: InternalAlignment(g45,g44)
    c: InternalAlignment(g46,g44)
    c: Block(g47)
    c: Block(g44)
    c: Block(g41)
    c: Block(g48)
    c: Block(g49)
    c: Coincident(g50,g37)
    c: Coincident(g50,g0)
    c: Coincident(g51,g37)
    c: Coincident(g51,g0)
    c: Block(g51)
    c: Block(g50)
    c: Block(g52)
    c: Block(g53)
    c: Block(g54)
    c: Block(g55)
    c: Block(g56)
    c: Coincident(g57,g47)
    c: Vertical(g57)
    c: Coincident(g58,g47)
    c: Vertical(g58)
    c: Coincident(g59,g16)
    c: Coincident(g59,g58)
    c: Horizontal(g59)
    c: Coincident(g60,g16)
    c: Coincident(g60,g55)
    c: Coincident(g61,g55)
    c: Coincident(g61,g54)
    c: Coincident(g62,g54)
    c: Coincident(g62,g53)
    c: Coincident(g63,g53)
    c: Coincident(g63,g10)
    c: Coincident(g64,g10)
    c: Coincident(g64,g4)
    c: Vertical(g64)
    c: Coincident(g65,g4)
    c: Coincident(g65,g48)
    c: Coincident(g66,g49)
    c: Coincident(g66,g48)
    c: Coincident(g67,g49)
    c: Coincident(g67,g52)
    c: Coincident(g68,g52)
    c: Coincident(g68,g22)
    c: Coincident(g69,g57)
    c: Horizontal(g69)
    c: Coincident(g70,g44)
    c: Coincident(g70,g41)
    c: Coincident(g71,g41)
    c: Vertical(g71)
    c: Coincident(g72,g34)
    c: Coincident(g72,g56)
    c: Horizontal(g72)
    c: Coincident(g73,g56)
    c: Coincident(g73,g28)
    c: Vertical(g73)
    c: Coincident(g74,g28)
    c: Coincident(g74,g34)
    c: Block(g69)
    c: Coincident(g75,g69)
    c: Vertical(g75)
    c: Distance(g75) = 152
    c: Block(g71)
    c: Vertical(g76)
    c: Distance(g76) = 10
    c: Vertical(g77)
    c: Distance(g77) = 4
    c: Vertical(g78)
    c: Distance(g78) = 4
    c: Vertical(g79)
    c: Distance(g79) = 10
    c: Coincident(g80,g78)
    c: Coincident(g80,g77)
    c: Block(g80)
    c: Coincident(g81,g79)
    c: Coincident(g81,g76)
    c: Block(g81)
    c: Coincident(g82,g76)
    c: Coincident(g82,g71)
    c: Horizontal(g82)
    c: Coincident(g83,g75)
    c: Coincident(g83,g77)
    c: Horizontal(g83)
    c: Distance(g83) = 7
    c: Distance(g82) = 7
    c: Vertical(g84)
    c: Distance(g84) = 4
    c: Vertical(g85)
    c: Distance(g85) = 4
    c: Coincident(g86,g84)
    c: Coincident(g86,g85)
    c: Block(g86)
    c: Coincident(g87,g84)
    c: Horizontal(g87)
    c: Distance(g87) = 4
    c: Coincident(g88,g85)
    c: Horizontal(g88)
    c: Distance(g88) = 4
    c: Coincident(g89,g87)
    c: Coincident(g89,g44)
    c: Vertical(g89)
    c: Coincident(g90,g88)
    c: Coincident(g90,g22)
    c: Vertical(g90)
    c: Coincident(g91,g78)
    c: Coincident(g91,g79)
    c: Horizontal(g91)
FEATURE [Sketcher::SketchObject] Sketch008  label="rightSideTop"
  FullyConstrained = false
  sketch-geometry (108):
    g0: Circle CenterX=302.996 CenterY=111.695 CenterZ=0 NormalX=0 NormalY=0 NormalZ=1 AngleXU=0 Radius=1
    g1: Circle CenterX=306.073 CenterY=114.251 CenterZ=0 NormalX=0 NormalY=0 NormalZ=1 AngleXU=0 Radius=1
    g2: Circle CenterX=306.073 CenterY=110.251 CenterZ=0 NormalX=0 NormalY=0 NormalZ=1 AngleXU=0 Radius=1
    g3: BSplineCurve PolesCount=3 KnotsCount=2 Degree=2 IsPeriodic=0
    g4: GeomPoint X=302.996 Y=111.695 Z=0
    g5: GeomPoint X=306.073 Y=110.251 Z=0
    g6: Circle CenterX=306.073 CenterY=95.2763 CenterZ=0 NormalX=0 NormalY=0 NormalZ=1 AngleXU=0 Radius=1
    g7: Circle CenterX=306.073 CenterY=91.2763 CenterZ=0 NormalX=0 NormalY=0 NormalZ=1 AngleXU=0 Radius=1
    g8: Circle CenterX=302.567 CenterY=89.3511 CenterZ=0 NormalX=0 NormalY=0 NormalZ=1 AngleXU=0 Radius=1
    g9: BSplineCurve PolesCount=3 KnotsCount=2 Degree=2 IsPeriodic=0
    g10: GeomPoint X=306.073 Y=95.2763 Z=0
    g11: GeomPoint X=302.567 Y=89.3511 Z=0
    g12: LineSegment StartX=306.073 StartY=110.251 StartZ=0 EndX=306.073 EndY=95.2763 EndZ=0
    g13: Circle CenterX=302.073 CenterY=124.221 CenterZ=0 NormalX=0 NormalY=0 NormalZ=1 AngleXU=0 Radius=1
    g14: Circle CenterX=306.073 CenterY=124.221 CenterZ=0 NormalX=0 NormalY=0 NormalZ=1 AngleXU=0 Radius=1
    g15: Circle CenterX=302.996 CenterY=121.665 CenterZ=0 NormalX=0 NormalY=0 NormalZ=1 AngleXU=0 Radius=1
    g16: BSplineCurve PolesCount=3 KnotsCount=2 Degree=2 IsPeriodic=0
    g17: GeomPoint X=302.073 Y=124.221 Z=0
    g18: GeomPoint X=302.996 Y=121.665 Z=0
    g19: Circle CenterX=306.073 CenterY=73.3346 CenterZ=0 NormalX=0 NormalY=0 NormalZ=1 AngleXU=0 Radius=1
    g20: Circle CenterX=306.073 CenterY=77.3346 CenterZ=0 NormalX=0 NormalY=0 NormalZ=1 AngleXU=0 Radius=1
    g21: Circle CenterX=302.535 CenterY=75.4095 CenterZ=0 NormalX=0 NormalY=0 NormalZ=1 AngleXU=0 Radius=1
    g22: BSplineCurve PolesCount=3 KnotsCount=2 Degree=2 IsPeriodic=0
    g23: GeomPoint X=306.073 Y=73.3346 Z=0
    g24: GeomPoint X=302.535 Y=75.4095 Z=0
    g25: Circle CenterX=362.073 CenterY=124.221 CenterZ=0 NormalX=0 NormalY=0 NormalZ=1 AngleXU=0 Radius=1
    g26: Circle CenterX=366.073 CenterY=124.221 CenterZ=0 NormalX=0 NormalY=0 NormalZ=1 AngleXU=0 Radius=1
    g27: Circle CenterX=362.567 CenterY=122.294 CenterZ=0 NormalX=0 NormalY=0 NormalZ=1 AngleXU=0 Radius=1
    g28: BSplineCurve PolesCount=3 KnotsCount=2 Degree=2 IsPeriodic=0
    g29: GeomPoint X=362.073 Y=124.221 Z=0
    g30: GeomPoint X=362.567 Y=122.294 Z=0
    g31: Circle CenterX=322.073 CenterY=124.221 CenterZ=0 NormalX=0 NormalY=0 NormalZ=1 AngleXU=0 Radius=1
    g32: Circle CenterX=318.073 CenterY=124.221 CenterZ=0 NormalX=0 NormalY=0 NormalZ=1 AngleXU=0 Radius=1
    g33: Circle CenterX=318.073 CenterY=120.221 CenterZ=0 NormalX=0 NormalY=0 NormalZ=1 AngleXU=0 Radius=1
    g34: BSplineCurve PolesCount=3 KnotsCount=2 Degree=2 IsPeriodic=0
    g35: GeomPoint X=322.073 Y=124.221 Z=0
    g36: GeomPoint X=318.073 Y=120.221 Z=0
    g37: Circle CenterX=322.073 CenterY=105.865 CenterZ=0 NormalX=0 NormalY=0 NormalZ=1 AngleXU=0 Radius=1
    g38: Circle CenterX=318.073 CenterY=105.865 CenterZ=0 NormalX=0 NormalY=0 NormalZ=1 AngleXU=0 Radius=1
    g39: Circle CenterX=318.073 CenterY=109.865 CenterZ=0 NormalX=0 NormalY=0 NormalZ=1 AngleXU=0 Radius=1
    g40: BSplineCurve PolesCount=3 KnotsCount=2 Degree=2 IsPeriodic=0
    g41: GeomPoint X=322.073 Y=105.865 Z=0
    g42: GeomPoint X=318.073 Y=109.865 Z=0
    g43: Circle CenterX=336.157 CenterY=107.779 CenterZ=0 NormalX=0 NormalY=0 NormalZ=1 AngleXU=0 Radius=1
    g44: Circle CenterX=332.651 CenterY=105.853 CenterZ=0 NormalX=0 NormalY=0 NormalZ=1 AngleXU=0 Radius=1
    g45: Circle CenterX=328.643 CenterY=105.865 CenterZ=0 NormalX=0 NormalY=0 NormalZ=1 AngleXU=0 Radius=1
    g46: BSplineCurve PolesCount=3 KnotsCount=2 Degree=2 IsPeriodic=0
    g47: GeomPoint X=336.157 Y=107.779 Z=0
    g48: GeomPoint X=328.643 Y=105.865 Z=0
    g49: Circle CenterX=322.073 CenterY=76.4095 CenterZ=0 NormalX=0 NormalY=0 NormalZ=1 AngleXU=0 Radius=4
    g50: BSplineCurve PolesCount=3 KnotsCount=2 Degree=2 IsPeriodic=0
    g51: GeomPoint X=318.073 Y=72.4095 Z=0
    g52: GeomPoint X=322.073 Y=76.4095 Z=0
    g53: Circle CenterX=375.073 CenterY=72.4095 CenterZ=0 NormalX=0 NormalY=0 NormalZ=1 AngleXU=0 Radius=1
    g54: Circle CenterX=375.073 CenterY=76.4095 CenterZ=0 NormalX=0 NormalY=0 NormalZ=1 AngleXU=0 Radius=1
    g55: Circle CenterX=371.073 CenterY=76.4095 CenterZ=0 NormalX=0 NormalY=0 NormalZ=1 AngleXU=0 Radius=1
    g56: BSplineCurve PolesCount=3 KnotsCount=2 Degree=2 IsPeriodic=0
    g57: GeomPoint X=375.073 Y=72.4095 Z=0
    g58: GeomPoint X=371.073 Y=76.4095 Z=0
    g59: LineSegment StartX=322.073 StartY=76.4095 StartZ=0 EndX=371.073 EndY=76.4095 EndZ=0
    g60: Circle CenterX=232.072 CenterY=133.221 CenterZ=0 NormalX=0 NormalY=0 NormalZ=1 AngleXU=0 Radius=1
    g61: Circle CenterX=226.072 CenterY=136.221 CenterZ=0 NormalX=0 NormalY=0 NormalZ=1 AngleXU=0 Radius=1
    g62: Circle CenterX=226.072 CenterY=124.221 CenterZ=0 NormalX=0 NormalY=0 NormalZ=1 AngleXU=0 Radius=1
    g63: Circle CenterX=232.072 CenterY=127.221 CenterZ=0 NormalX=0 NormalY=0 NormalZ=1 AngleXU=0 Radius=1
    g64: BSplineCurve PolesCount=5 KnotsCount=3 Degree=3 IsPeriodic=0
    g65: GeomPoint X=232.072 Y=133.221 Z=0
    g66: GeomPoint X=223.072 Y=130.221 Z=0
    g67: GeomPoint X=232.072 Y=127.221 Z=0
    g68: LineSegment StartX=240.687 StartY=51.8263 StartZ=0 EndX=243.317 EndY=53.2701 EndZ=0
    g69: LineSegment StartX=243.575 StartY=46.5669 StartZ=0 EndX=246.205 EndY=48.0108 EndZ=0
    g70: ArcOfCircle CenterX=247.391 CenterY=52.0843 CenterZ=0 NormalX=0 NormalY=0 NormalZ=1 AngleXU=0 Radius=4.24264 StartAngle=4.42912 EndAngle=9.14151
    g71: LineSegment StartX=243.475 StartY=65.4951 StartZ=0 EndX=245.073 EndY=63.5726 EndZ=0
    g72: LineSegment StartX=243.575 StartY=46.5669 StartZ=0 EndX=245.072 EndY=43.8408 EndZ=0
    g73: LineSegment StartX=245.072 StartY=43.8408 StartZ=0 EndX=302.535 EndY=75.4095 EndZ=0
    g74: LineSegment StartX=239.192 StartY=54.5542 StartZ=0 EndX=302.567 EndY=89.3511 EndZ=0
    g75: LineSegment StartX=232.072 StartY=127.221 StartZ=0 EndX=232.072 EndY=124.221 EndZ=0
    g76: LineSegment StartX=232.072 StartY=136.221 StartZ=0 EndX=232.072 EndY=133.221 EndZ=0
    g77: LineSegment StartX=232.072 StartY=136.221 StartZ=0 EndX=407.073 EndY=136.221 EndZ=0
    g78: LineSegment StartX=322.073 StartY=124.221 StartZ=0 EndX=362.073 EndY=124.221 EndZ=0
    g79: LineSegment StartX=362.567 StartY=122.294 StartZ=0 EndX=336.157 EndY=107.779 EndZ=0
    g80: LineSegment StartX=322.073 StartY=105.865 StartZ=0 EndX=328.643 EndY=105.865 EndZ=0
    g81: LineSegment StartX=318.073 StartY=120.221 StartZ=0 EndX=318.073 EndY=109.865 EndZ=0
    g82: LineSegment StartX=232.072 StartY=124.221 StartZ=0 EndX=302.073 EndY=124.221 EndZ=0
    g83: LineSegment StartX=302.996 StartY=121.665 StartZ=0 EndX=240.171 EndY=69.471 EndZ=0
    g84: LineSegment StartX=240.171 StartY=69.471 StartZ=0 EndX=241.711 EndY=67.6177 EndZ=0
    g85: LineSegment StartX=241.711 StartY=67.6177 StartZ=0 EndX=246.787 EndY=71.8365 EndZ=0
    g86: LineSegment StartX=246.787 StartY=71.8365 StartZ=0 EndX=248.551 EndY=69.712 EndZ=0
    g87: LineSegment StartX=248.551 StartY=69.712 StartZ=0 EndX=243.475 EndY=65.4951 EndZ=0
    g88: LineSegment StartX=245.073 StartY=63.5726 StartZ=0 EndX=302.996 EndY=111.695 EndZ=0
    g89: LineSegment StartX=239.192 StartY=54.5542 StartZ=0 EndX=240.687 EndY=51.8263 EndZ=0
    g90: LineSegment StartX=375.073 StartY=48.2206 StartZ=0 EndX=382.073 EndY=48.2206 EndZ=0
    g91: LineSegment StartX=407.073 StartY=48.2206 StartZ=0 EndX=400.073 EndY=48.2206 EndZ=0
    g92: LineSegment StartX=394.073 StartY=48.2206 StartZ=0 EndX=394.073 EndY=52.2206 EndZ=0
    g93: LineSegment StartX=388.073 StartY=48.2206 StartZ=0 EndX=388.073 EndY=58.2206 EndZ=0
    g94: ArcOfCircle CenterX=385.073 CenterY=61.2206 CenterZ=0 NormalX=0 NormalY=0 NormalZ=1 AngleXU=0 Radius=4.24264 StartAngle=5.49779 EndAngle=10.2102
    g95: ArcOfCircle CenterX=397.073 CenterY=55.2206 CenterZ=0 NormalX=0 NormalY=0 NormalZ=1 AngleXU=0 Radius=4.24264 StartAngle=5.49779 EndAngle=10.2102
    g96: LineSegment StartX=382.073 StartY=58.2206 StartZ=0 EndX=382.073 EndY=48.2206 EndZ=0
    g97: LineSegment StartX=400.073 StartY=52.2206 StartZ=0 EndX=400.073 EndY=48.2206 EndZ=0
    g98: LineSegment StartX=394.073 StartY=48.2206 StartZ=0 EndX=388.073 EndY=48.2206 EndZ=0
    g99: LineSegment StartX=306.073 StartY=-27.5935 StartZ=0 EndX=310.073 EndY=-27.5935 EndZ=0
    g100: LineSegment StartX=318.073 StartY=-27.5935 StartZ=0 EndX=314.073 EndY=-27.5935 EndZ=0
    g101: LineSegment StartX=310.073 StartY=-27.5935 StartZ=0 EndX=310.073 EndY=-31.5935 EndZ=0
    g102: LineSegment StartX=314.073 StartY=-27.5935 StartZ=0 EndX=314.073 EndY=-31.5935 EndZ=0
    g103: ArcOfCircle CenterX=312.073 CenterY=-33.5935 CenterZ=0 NormalX=0 NormalY=0 NormalZ=1 AngleXU=0 Radius=2.82843 StartAngle=2.35619 EndAngle=7.06858
    g104: LineSegment StartX=375.073 StartY=72.4095 StartZ=0 EndX=375.073 EndY=48.2206 EndZ=0
    g105: LineSegment StartX=407.073 StartY=48.2206 StartZ=0 EndX=407.073 EndY=136.221 EndZ=0
    g106: LineSegment StartX=318.073 StartY=-27.5935 StartZ=0 EndX=318.073 EndY=72.4095 EndZ=0
    g107: LineSegment StartX=306.073 StartY=73.3346 StartZ=0 EndX=306.073 EndY=-27.5935 EndZ=0
  constraints (136):
    c: Weight(g0) = 1
    c: Equal(g0,g1)
    c: Equal(g0,g2)
    c: InternalAlignment(g0,g3)
    c: InternalAlignment(g1,g3)
    c: InternalAlignment(g2,g3)
    c: InternalAlignment(g4,g3)
    c: InternalAlignment(g5,g3)
    c: Weight(g6) = 1
    c: Equal(g6,g7)
    c: Equal(g6,g8)
    c: InternalAlignment(g6,g9)
    c: InternalAlignment(g7,g9)
    c: InternalAlignment(g8,g9)
    c: InternalAlignment(g10,g9)
    c: InternalAlignment(g11,g9)
    c: Block(g3)
    c: Block(g9)
    c: Coincident(g12,g3)
    c: Coincident(g12,g9)
    c: Vertical(g12)
    c: Weight(g13) = 1
    c: Equal(g13,g14)
    c: Equal(g13,g15)
    c: InternalAlignment(g14,g16)
    c: InternalAlignment(g15,g16)
    c: InternalAlignment(g17,g16)
    c: InternalAlignment(g18,g16)
    c: Block(g71)
    c: Block(g72)
    c: Coincident(g73,g72)
    c: Coincident(g73,g22)
    c: Block(g73)
    c: Coincident(g70,g69)
    c: Coincident(g70,g68)
    c: Coincident(g74,g9)
    c: Block(g74)
    c: Distance(g71) = 2.5
    c: Block(g64)
    c: Block(g46)
    c: Block(g59)
    c: Coincident(g75,g64)
    c: Vertical(g75)
    c: Coincident(g76,g64)
    c: Vertical(g76)
    c: Coincident(g77,g76)
    c: Horizontal(g77)
    c: Coincident(g78,g34)
    c: Coincident(g78,g28)
    c: Horizontal(g78)
    c: Coincident(g79,g28)
    c: Coincident(g79,g46)
    c: Coincident(g80,g40)
    c: Coincident(g80,g46)
    c: Horizontal(g80)
    c: Coincident(g81,g34)
    c: Coincident(g81,g40)
    c: Vertical(g81)
    c: Block(g34)
    c: Block(g40)
    c: Block(g28)
    c: Coincident(g82,g75)
    c: Coincident(g82,g16)
    c: Horizontal(g82)
    c: Coincident(g83,g16)
    c: Block(g82)
    c: Block(g83)
    c: Block(g16)
    c: Coincident(g84,g83)
    c: Block(g84)
    c: Coincident(g85,g84)
    c: Block(g85)
    c: Coincident(g86,g85)
    c: Coincident(g87,g86)
    c: Coincident(g87,g71)
    c: Block(g87)
    c: Coincident(g88,g71)
    c: Coincident(g88,g3)
    c: Block(g88)
    c: Coincident(g89,g74)
    c: Coincident(g89,g68)
    c: Block(g70)
    c: Block(g68)
    c: Block(g69)
    c: Block(g22)
    c: Block(g50)
    c: Block(g56)
    c: Horizontal(g90)
    c: Distance(g90) = 7
    c: Horizontal(g91)
    c: Distance(g91) = 7
    c: Vertical(g92)
    c: Distance(g92) = 4
    c: Vertical(g93)
    c: Distance(g93) = 10
    c: Coincident(g94,g93)
    c: Coincident(g95,g92)
    c: Block(g95)
    c: Block(g94)
    c: Coincident(g96,g94)
    c: Coincident(g96,g90)
    c: Vertical(g96)
    c: Coincident(g97,g95)
    c: Coincident(g97,g91)
    c: Vertical(g97)
    c: Coincident(g98,g92)
    c: Coincident(g98,g93)
    c: Horizontal(g98)
    c: Horizontal(g99)
    c: Distance(g99) = 4
    c: Horizontal(g100)
    c: Distance(g100) = 4
    c: Coincident(g101,g99)
    c: Vertical(g101)
    c: Coincident(g102,g100)
    c: Vertical(g102)
    c: Distance(g101) = 4
    c: Distance(g102) = 4
    c: Coincident(g103,g101)
    c: Coincident(g103,g102)
    c: Block(g103)
    c: Coincident(g104,g56)
    c: Coincident(g104,g90)
    c: Vertical(g104)
    c: Block(g104)
    c: Coincident(g105,g91)
    c: Coincident(g105,g77)
    c: Vertical(g105)
    c: Block(g77)
    c: Block(g105)
    c: Coincident(g106,g100)
    c: Coincident(g106,g50)
    c: Vertical(g106)
    c: Coincident(g107,g22)
    c: Coincident(g107,g99)
    c: Vertical(g107)
FEATURE [Sketcher::SketchObject] Sketch009  label="middleBottom"
  FullyConstrained = true
  sketch-geometry (109):
    g0: Circle CenterX=175.022 CenterY=5.37834 CenterZ=0 NormalX=0 NormalY=0 NormalZ=1 AngleXU=0 Radius=1
    g1: Circle CenterX=179.022 CenterY=7.57463 CenterZ=0 NormalX=0 NormalY=0 NormalZ=1 AngleXU=0 Radius=1
    g2: Circle CenterX=179.022 CenterY=5.34704 CenterZ=0 NormalX=0 NormalY=0 NormalZ=1 AngleXU=0 Radius=1
    g3: BSplineCurve PolesCount=3 KnotsCount=2 Degree=2 IsPeriodic=0
    g4: GeomPoint X=175.022 Y=5.37834 Z=0
    g5: GeomPoint X=179.022 Y=5.34704 Z=0
    g6: Circle CenterX=189.124 CenterY=5.37834 CenterZ=0 NormalX=0 NormalY=0 NormalZ=1 AngleXU=0 Radius=1
    g7: Circle CenterX=185.124 CenterY=7.57463 CenterZ=0 NormalX=0 NormalY=0 NormalZ=1 AngleXU=0 Radius=1
    g8: Circle CenterX=185.124 CenterY=5.34704 CenterZ=0 NormalX=0 NormalY=0 NormalZ=1 AngleXU=0 Radius=1
    g9: BSplineCurve PolesCount=3 KnotsCount=2 Degree=2 IsPeriodic=0
    g10: GeomPoint X=189.124 Y=5.37834 Z=0
    g11: GeomPoint X=185.124 Y=5.34704 Z=0
    g12: Circle CenterX=224.513 CenterY=-14.0532 CenterZ=0 NormalX=0 NormalY=0 NormalZ=1 AngleXU=0 Radius=1
    g13: Circle CenterX=236.584 CenterY=-24.2775 CenterZ=0 NormalX=0 NormalY=0 NormalZ=1 AngleXU=0 Radius=1
    g14: BSplineCurve PolesCount=3 KnotsCount=2 Degree=2 IsPeriodic=0
    g15: GeomPoint X=236.584 Y=-24.2775 Z=0
    g16: Circle CenterX=125.607 CenterY=-21.7539 CenterZ=0 NormalX=0 NormalY=0 NormalZ=1 AngleXU=0 Radius=1
    g17: Circle CenterX=139.632 CenterY=-14.0532 CenterZ=0 NormalX=0 NormalY=0 NormalZ=1 AngleXU=0 Radius=1
    g18: Circle CenterX=127.325 CenterY=-24.2775 CenterZ=0 NormalX=0 NormalY=0 NormalZ=1 AngleXU=0 Radius=1
    g19: BSplineCurve PolesCount=3 KnotsCount=2 Degree=2 IsPeriodic=0
    g20: GeomPoint X=125.607 Y=-21.7539 Z=0
    g21: GeomPoint X=127.325 Y=-24.2775 Z=0
    g22: Circle CenterX=179.022 CenterY=-85.8163 CenterZ=0 NormalX=0 NormalY=0 NormalZ=1 AngleXU=0 Radius=1
    g23: Circle CenterX=179.022 CenterY=-91.7794 CenterZ=0 NormalX=0 NormalY=0 NormalZ=1 AngleXU=0 Radius=1
    g24: Circle CenterX=171.895 CenterY=-91.8014 CenterZ=0 NormalX=0 NormalY=0 NormalZ=1 AngleXU=0 Radius=1
    g25: BSplineCurve PolesCount=3 KnotsCount=2 Degree=2 IsPeriodic=0
    g26: GeomPoint X=179.022 Y=-85.8163 Z=0
    g27: GeomPoint X=171.895 Y=-91.8014 Z=0
    g28: Circle CenterX=185.124 CenterY=-86.2028 CenterZ=0 NormalX=0 NormalY=0 NormalZ=1 AngleXU=0 Radius=1
    g29: Circle CenterX=185.124 CenterY=-91.7794 CenterZ=0 NormalX=0 NormalY=0 NormalZ=1 AngleXU=0 Radius=1
    g30: Circle CenterX=191.747 CenterY=-91.7794 CenterZ=0 NormalX=0 NormalY=0 NormalZ=1 AngleXU=0 Radius=1
    g31: BSplineCurve PolesCount=3 KnotsCount=2 Degree=2 IsPeriodic=0
    g32: GeomPoint X=185.124 Y=-86.2028 Z=0
    g33: GeomPoint X=191.747 Y=-91.7794 Z=0
    g34: BSplineCurve PolesCount=5 KnotsCount=3 Degree=3 IsPeriodic=0
    g35: LineSegment StartX=132.072 StartY=-100.779 StartZ=0 EndX=132.072 EndY=-103.779 EndZ=0
    g36: GeomPoint X=232.072 Y=-94.7794 Z=0
    g37: GeomPoint X=223.072 Y=-97.7794 Z=0
    g38: Circle CenterX=232.072 CenterY=-94.7794 CenterZ=0 NormalX=0 NormalY=0 NormalZ=1 AngleXU=0 Radius=1
    g39: Circle CenterX=232.072 CenterY=-100.779 CenterZ=0 NormalX=0 NormalY=0 NormalZ=1 AngleXU=0 Radius=1
    g40: BSplineCurve PolesCount=5 KnotsCount=3 Degree=3 IsPeriodic=0
    g41: GeomPoint X=232.072 Y=-100.779 Z=0
    g42: LineSegment StartX=123.656 StartY=-37.1092 StartZ=0 EndX=122.136 EndY=-35.2714 EndZ=0
    g43: LineSegment StartX=117.05 StartY=-39.4781 StartZ=0 EndX=115.291 EndY=-37.3514 EndZ=0
    g44: LineSegment StartX=120.377 StartY=-33.1447 StartZ=0 EndX=118.86 EndY=-31.3104 EndZ=0
    g45: ArcOfCircle CenterX=116.562 CenterY=-19.6236 CenterZ=0 NormalX=0 NormalY=0 NormalZ=1 AngleXU=0 Radius=4.24264 StartAngle=1.28753 EndAngle=5.99992
    g46: LineSegment StartX=240.266 StartY=-37.1092 StartZ=0 EndX=189.124 EndY=5.37834 EndZ=0
    g47: LineSegment StartX=191.747 StartY=-91.7794 StartZ=0 EndX=232.072 EndY=-91.7794 EndZ=0
    g48: LineSegment StartX=232.072 StartY=-91.7794 StartZ=0 EndX=232.072 EndY=-94.7794 EndZ=0
    g49: LineSegment StartX=232.072 StartY=-100.779 StartZ=0 EndX=232.072 EndY=-103.779 EndZ=0
    g50: LineSegment StartX=132.072 StartY=-103.779 StartZ=0 EndX=232.072 EndY=-103.779 EndZ=0
    g51: LineSegment StartX=132.072 StartY=-91.8014 StartZ=0 EndX=132.072 EndY=-94.7791 EndZ=0
    g52: LineSegment StartX=132.072 StartY=-91.8014 StartZ=0 EndX=171.895 EndY=-91.8014 EndZ=0
    g53: LineSegment StartX=179.022 StartY=-85.8163 StartZ=0 EndX=179.022 EndY=5.34704 EndZ=0
    g54: LineSegment StartX=175.022 StartY=5.37834 StartZ=0 EndX=123.656 EndY=-37.1092 EndZ=0
    g55: LineSegment StartX=185.124 StartY=5.34704 StartZ=0 EndX=185.124 EndY=-86.2028 EndZ=0
    g56: LineSegment StartX=122.136 StartY=-35.2714 StartZ=0 EndX=117.05 EndY=-39.4781 EndZ=0
    g57: LineSegment StartX=115.291 StartY=-37.3514 StartZ=0 EndX=120.377 EndY=-33.1447 EndZ=0
    g58: LineSegment StartX=118.86 StartY=-31.3104 StartZ=0 EndX=127.325 EndY=-24.2775 EndZ=0
    g59: LineSegment StartX=125.607 StartY=-21.7539 StartZ=0 EndX=124.815 EndY=-22.1887 EndZ=0
    g60: LineSegment StartX=123.265 StartY=-19.3655 StartZ=0 EndX=124.815 EndY=-22.1887 EndZ=0
    g61: LineSegment StartX=120.636 StartY=-20.8094 StartZ=0 EndX=123.265 EndY=-19.3655 EndZ=0
    g62: LineSegment StartX=117.748 StartY=-15.55 StartZ=0 EndX=120.377 EndY=-14.1062 EndZ=0
    g63: LineSegment StartX=120.377 StartY=-14.1062 StartZ=0 EndX=118.934 EndY=-11.4765 EndZ=0
    g64: LineSegment StartX=236.584 StartY=-24.2775 StartZ=0 EndX=245.072 EndY=-31.3037 EndZ=0
    g65: LineSegment StartX=245.072 StartY=-31.3037 StartZ=0 EndX=243.535 EndY=-33.1602 EndZ=0
    g66: LineSegment StartX=243.535 StartY=-33.1602 StartZ=0 EndX=248.619 EndY=-37.3688 EndZ=0
    g67: LineSegment StartX=248.619 StartY=-37.3688 StartZ=0 EndX=246.855 EndY=-39.5064 EndZ=0
    g68: LineSegment StartX=246.855 StartY=-39.5064 StartZ=0 EndX=241.778 EndY=-35.2889 EndZ=0
    g69: LineSegment StartX=241.778 StartY=-35.2889 StartZ=0 EndX=240.266 EndY=-37.1092 EndZ=0
    g70: LineSegment StartX=243.628 StartY=-14.0323 StartZ=0 EndX=246.258 EndY=-15.476 EndZ=0
    g71: LineSegment StartX=240.741 StartY=-19.2917 StartZ=0 EndX=243.37 EndY=-20.7355 EndZ=0
    g72: ArcOfCircle CenterX=247.444 CenterY=-19.5496 CenterZ=0 NormalX=0 NormalY=0 NormalZ=1 AngleXU=0 Radius=4.24264 StartAngle=3.4249 EndAngle=8.13729
    g73: LineSegment StartX=240.741 StartY=-19.2917 StartZ=0 EndX=239.201 EndY=-22.0968 EndZ=0
    g74: LineSegment StartX=238.538 StartY=-21.7516 StartZ=0 EndX=239.201 EndY=-22.0968 EndZ=0
    g75: LineSegment StartX=245.072 StartY=-11.4025 StartZ=0 EndX=243.628 EndY=-14.0323 EndZ=0
    g76-g91: Circle x16 (B-spline internal-alignment scaffolding for g92; pole/knot coordinates omitted)
    g92: BSplineCurve PolesCount=16 KnotsCount=14 Degree=3 IsPeriodic=0
    g93-g106: GeomPoint x14 (B-spline internal-alignment scaffolding for g92; pole/knot coordinates omitted)
    g107: LineSegment StartX=165.871 StartY=14.2956 StartZ=0 EndX=118.934 EndY=-11.4765 EndZ=0
    g108: LineSegment StartX=198.264 StartY=14.2963 StartZ=0 EndX=245.072 EndY=-11.4025 EndZ=0
  constraints (146):
    c: Weight(g0) = 1
    c: Equal(g0,g1)
    c: Equal(g0,g2)
    c: InternalAlignment(g0,g3)
    c: InternalAlignment(g1,g3)
    c: InternalAlignment(g2,g3)
    c: InternalAlignment(g4,g3)
    c: InternalAlignment(g5,g3)
    c: Weight(g6) = 1
    c: Equal(g6,g7)
    c: Equal(g6,g8)
    c: InternalAlignment(g6,g9)
    c: InternalAlignment(g7,g9)
    c: InternalAlignment(g8,g9)
    c: InternalAlignment(g10,g9)
    c: InternalAlignment(g11,g9)
    c: Block(g9)
    c: Block(g3)
    c: InternalAlignment(g12,g14)
    c: InternalAlignment(g13,g14)
    c: InternalAlignment(g15,g14)
    c: Block(g14)
    c: Weight(g16) = 1
    c: Equal(g16,g17)
    c: Equal(g16,g18)
    c: InternalAlignment(g16,g19)
    c: InternalAlignment(g17,g19)
    c: InternalAlignment(g18,g19)
    c: InternalAlignment(g20,g19)
    c: InternalAlignment(g21,g19)
    c: Block(g19)
    c: Weight(g22) = 1
    c: Equal(g22,g23)
    c: Equal(g22,g24)
    c: InternalAlignment(g22,g25)
    c: InternalAlignment(g23,g25)
    c: InternalAlignment(g24,g25)
    c: InternalAlignment(g26,g25)
    c: InternalAlignment(g27,g25)
    c: Weight(g28) = 1
    c: Equal(g28,g29)
    c: Equal(g28,g30)
    c: InternalAlignment(g28,g31)
    c: InternalAlignment(g29,g31)
    c: InternalAlignment(g30,g31)
    c: InternalAlignment(g32,g31)
    c: InternalAlignment(g33,g31)
    c: Block(g31)
    c: Block(g25)
    c: Block(g34)
    c: Coincident(g35,g34)
    c: Vertical(g35)
    c: Block(g35)
    c: Equal(g38,g39)
    c: InternalAlignment(g38,g40)
    c: InternalAlignment(g39,g40)
    c: InternalAlignment(g36,g40)
    c: InternalAlignment(g37,g40)
    c: InternalAlignment(g41,g40)
    c: Block(g40)
    c: Distance(g42) = 2.385
    c: Distance(g43) = 2.76
    c: Parallel(g42,g44)
    c: Block(g45)
    c: Coincident(g46,g9)
    c: Coincident(g47,g31)
    c: Horizontal(g47)
    c: Block(g47)
    c: Coincident(g48,g47)
    c: Coincident(g48,g40)
    c: Vertical(g48)
    c: Block(g48)
    c: Coincident(g49,g40)
    c: Vertical(g49)
    c: Block(g49)
    c: Coincident(g50,g35)
    c: Coincident(g50,g49)
    c: Horizontal(g50)
    c: Block(g50)
    c: Coincident(g51,g34)
    c: Vertical(g51)
    c: Coincident(g52,g51)
    c: Coincident(g52,g25)
    c: Horizontal(g52)
    c: Coincident(g53,g25)
    c: Coincident(g53,g3)
    c: Vertical(g53)
    c: Coincident(g54,g3)
    c: Coincident(g54,g42)
    c: Coincident(g55,g9)
    c: Coincident(g55,g31)
    c: Vertical(g55)
    c: Block(g42)
    c: Coincident(g56,g42)
    c: Coincident(g56,g43)
    c: Coincident(g57,g43)
    c: Coincident(g57,g44)
    c: Block(g57)
    c: Block(g56)
    c: Coincident(g58,g44)
    c: Coincident(g58,g19)
    c: Block(g58)
    c: Coincident(g59,g19)
    c: Block(g59)
    c: Coincident(g60,g59)
    c: Block(g60)
    c: Coincident(g61,g45)
    c: Coincident(g61,g60)
    c: Coincident(g62,g45)
    c: Coincident(g63,g62)
    c: Block(g63)
    c: Coincident(g64,g14)
    c: Block(g64)
    c: Coincident(g65,g64)
    c: Coincident(g66,g65)
    c: Coincident(g67,g66)
    c: Coincident(g68,g67)
    c: Coincident(g69,g68)
    c: Coincident(g69,g46)
    c: Block(g46)
    c: Block(g68)
    c: Block(g66)
    c: Distance(g70) = 3
    c: Distance(g71) = 3
    c: Coincident(g72,g70)
    c: Coincident(g72,g71)
    c: Block(g72)
    c: Coincident(g73,g71)
    c: Distance(g73) = 3.2
    c: Coincident(g74,g14)
    c: Coincident(g74,g73)
    c: Coincident(g75,g70)
    c: Block(g75)
    c: Block(g73)
    c: Distance(g63) = 3
    c: Distance(g60) = 3.22077
    c: Weight(g76) = 1
    c: Equal(g76, g77-g91) x15
    c: InternalAlignment(g76-g91 -> g92) x16
    c: InternalAlignment(g93-g106 -> g92) x14
    c: Coincident(g107,g92)
    c: Coincident(g107,g63)
    c: Block(g107)
    c: Block(g92)
    c: Coincident(g108,g92)
    c: Coincident(g108,g75)
FEATURE [Sketcher::SketchObject] Sketch010  label="legBottomBack"
  FullyConstrained = true
  MapMode = 4
  Placement = pos=(0,0,0) rot=(0.57735,0.57735,0.57735;2.0944rad)
  sketch-geometry (76):
    g0: Circle CenterX=-17.0256 CenterY=-190.268 CenterZ=0 NormalX=0 NormalY=0 NormalZ=1 AngleXU=0 Radius=10.5072
    g1: Circle CenterX=-37.7758 CenterY=-187.672 CenterZ=0 NormalX=0 NormalY=0 NormalZ=1 AngleXU=0 Radius=5.64388
    g2: Circle CenterX=-51.4606 CenterY=-185.091 CenterZ=0 NormalX=0 NormalY=0 NormalZ=1 AngleXU=0 Radius=3.01653
    g3: Circle CenterX=-60.4835 CenterY=-182.688 CenterZ=0 NormalX=0 NormalY=0 NormalZ=1 AngleXU=0 Radius=2.12826
    g4: Circle CenterX=-3.29005 CenterY=-177.662 CenterZ=0 NormalX=0 NormalY=0 NormalZ=1 AngleXU=0 Radius=3.26661
    g5: ArcOfCircle CenterX=11.0205 CenterY=-198.019 CenterZ=0 NormalX=0 NormalY=0 NormalZ=1 AngleXU=0 Radius=13 StartAngle=2.78068 EndAngle=5.92131
    g6: LineSegment StartX=5.08312 StartY=-176.581 StartZ=0 EndX=-1.14188 EndY=-193.429 EndZ=0
    g7: ArcOfCircle CenterX=17.2475 CenterY=-181.166 CenterZ=0 NormalX=0 NormalY=0 NormalZ=1 AngleXU=0 Radius=13 StartAngle=1.21042 EndAngle=2.78109
    g8: LineSegment StartX=38.8952 StartY=-231.233 StartZ=0 EndX=39.9512 EndY=-228.425 EndZ=0
    g9: ArcOfCircle CenterX=46.9911 CenterY=-209.705 CenterZ=0 NormalX=0 NormalY=0 NormalZ=1 AngleXU=0 Radius=20 StartAngle=2.78766 EndAngle=4.35269
    g10: LineSegment StartX=23.7323 StartY=-126.969 StartZ=0 EndX=17.4091 EndY=-143.817 EndZ=0
    g11: ArcOfCircle CenterX=29.5716 CenterY=-148.408 CenterZ=0 NormalX=0 NormalY=0 NormalZ=1 AngleXU=0 Radius=13 StartAngle=2.78068 EndAngle=4.35262
    g12: ArcOfCircle CenterX=35.8967 CenterY=-131.555 CenterZ=0 NormalX=0 NormalY=0 NormalZ=1 AngleXU=0 Radius=13 StartAngle=1.21584 EndAngle=2.78109
    g13: ArcOfCircle CenterX=48.1805 CenterY=-98.7782 CenterZ=0 NormalX=0 NormalY=0 NormalZ=1 AngleXU=0 Radius=13 StartAngle=2.78068 EndAngle=4.35005
    g14: LineSegment StartX=42.354 StartY=-77.3391 StartZ=0 EndX=36.018 EndY=-94.1875 EndZ=0
    g15: ArcOfCircle CenterX=54.5183 CenterY=-81.9247 CenterZ=0 NormalX=0 NormalY=0 NormalZ=1 AngleXU=0 Radius=13 StartAngle=2.42113 EndAngle=2.78109
    g16: ArcOfCircle CenterX=20.184 CenterY=-217.506 CenterZ=0 NormalX=0 NormalY=0 NormalZ=1 AngleXU=0 Radius=3.81084 StartAngle=1.88136 EndAngle=6.80465
    g17: LineSegment StartX=38.4753 StartY=-115.966 StartZ=0 EndX=41.2852 EndY=-117.017 EndZ=0
    g18: ArcOfCircle CenterX=36.3663 CenterY=-113.042 CenterZ=0 NormalX=0 NormalY=0 NormalZ=1 AngleXU=0 Radius=3.60555 StartAngle=0.230024 EndAngle=5.3372
    g19: LineSegment StartX=39.8769 StartY=-112.22 StartZ=0 EndX=42.6867 EndY=-113.271 EndZ=0
    g20: LineSegment StartX=19.9036 StartY=-165.61 StartZ=0 EndX=22.7134 EndY=-166.661 EndZ=0
    g21: ArcOfCircle CenterX=17.7945 CenterY=-162.686 CenterZ=0 NormalX=0 NormalY=0 NormalZ=1 AngleXU=0 Radius=3.60555 StartAngle=0.230024 EndAngle=5.3372
    g22: LineSegment StartX=21.3051 StartY=-161.864 StartZ=0 EndX=24.1149 EndY=-162.915 EndZ=0
    g23: LineSegment StartX=41.085 StartY=-66.3176 StartZ=0 EndX=46.0385 EndY=-62.5254 EndZ=0
    g24: LineSegment StartX=48.9563 StartY=-66.3367 StartZ=0 EndX=44.7488 EndY=-73.3482 EndZ=0
    g25: ArcOfCircle CenterX=49.8795 CenterY=-62.6074 CenterZ=0 NormalX=0 NormalY=0 NormalZ=1 AngleXU=0 Radius=3.84187 StartAngle=4.46973 EndAngle=9.40343
    g26: LineSegment StartX=43.5724 StartY=-110.934 StartZ=0 EndX=42.6867 EndY=-113.271 EndZ=0
    g27: LineSegment StartX=40.4148 StartY=-119.365 StartZ=0 EndX=41.2852 EndY=-117.017 EndZ=0
    g28: LineSegment StartX=21.8316 StartY=-169.001 StartZ=0 EndX=22.7134 EndY=-166.661 EndZ=0
    g29: LineSegment StartX=24.9948 StartY=-160.575 StartZ=0 EndX=24.1149 EndY=-162.915 EndZ=0
    g30: LineSegment StartX=23.1786 StartY=-202.622 StartZ=0 EndX=19.0195 EndY=-213.878 EndZ=0
    g31: LineSegment StartX=28.2308 StartY=-202.773 StartZ=0 EndX=23.4884 EndY=-215.608 EndZ=0
    g32: LineSegment StartX=-76.2249 StartY=-179.393 StartZ=0 EndX=-72.8553 EndY=-180.66 EndZ=0
    g33: ArcOfCircle CenterX=-71.1257 CenterY=-183.448 CenterZ=0 NormalX=0 NormalY=0 NormalZ=1 AngleXU=0 Radius=3.28025 StartAngle=3.43759 EndAngle=8.40938
    g34: LineSegment StartX=-79.0409 StartY=-186.881 StartZ=0 EndX=38.8952 EndY=-231.233 EndZ=0
    g35-g53: Circle x19 (B-spline internal-alignment scaffolding for g54; pole/knot coordinates omitted)
    g54: BSplineCurve PolesCount=19 KnotsCount=17 Degree=3 IsPeriodic=0
    g55-g71: GeomPoint x17 (B-spline internal-alignment scaffolding for g54; pole/knot coordinates omitted)
    g72: LineSegment StartX=-74.2633 StartY=-184.404 StartZ=0 EndX=-77.6329 EndY=-183.137 EndZ=0
    g73: LineSegment StartX=-79.0409 StartY=-186.881 StartZ=0 EndX=-77.6329 EndY=-183.137 EndZ=0
    g74: LineSegment StartX=8.65492 StartY=-152.553 StartZ=0 EndX=41.085 EndY=-66.3176 EndZ=0
    g75: LineSegment StartX=-74.4658 StartY=-174.715 StartZ=0 EndX=-76.2249 EndY=-179.393 EndZ=0
  constraints (76):
    c: Block(g5)
    c: Block(g7)
    c: Block(g0)
    c: Block(g4)
    c: Block(g1)
    c: Block(g2)
    c: Block(g3)
    c: Block(g9)
    c: Coincident(g8,g9)
    c: Block(g8)
    c: Coincident(g6,g7)
    c: Coincident(g6,g5)
    c: Block(g11)
    c: Block(g12)
    c: Coincident(g10,g12)
    c: Coincident(g10,g11)
    c: Block(g13)
    c: Block(g15)
    c: Coincident(g14,g15)
    c: Coincident(g14,g13)
    c: Block(g16)
    c: Block(g18)
    c: Coincident(g19,g18)
    c: Coincident(g17,g18)
    c: Parallel(g19,g17)
    c: Block(g17)
    c: Block(g19)
    c: Block(g21)
    c: Coincident(g22,g21)
    c: Coincident(g20,g21)
    c: Parallel(g22,g20)
    c: Block(g20)
    c: Block(g22)
    c: Block(g23)
    c: Coincident(g25,g23)
    c: Coincident(g25,g24)
    c: Block(g25)
    c: Block(g24)
    c: Coincident(g26,g19)
    c: Block(g26)
    c: Coincident(g27,g17)
    c: Block(g27)
    c: Coincident(g28,g20)
    c: Coincident(g29,g22)
    c: Block(g29)
    c: Block(g28)
    c: Coincident(g30,g5)
    c: Coincident(g30,g16)
    c: Block(g30)
    c: Coincident(g7,g28)
    c: Coincident(g11,g29)
    c: Coincident(g12,g27)
    c: Coincident(g13,g26)
    c: Coincident(g15,g24)
    c: Coincident(g31,g9)
    c: Coincident(g31,g16)
    c: Distance(g32) = 3.6
    c: Block(g32)
    c: Coincident(g33,g32)
    c: Coincident(g34,g8)
    c: Weight(g35) = 1
    c: Equal(g35, g36-g53) x18
    c: InternalAlignment(g35-g53 -> g54) x19
    c: InternalAlignment(g55-g71 -> g54) x17
    c: Block(g33)
    c: Block(g54)
    c: Coincident(g72,g33)
    c: Coincident(g73,g34)
    c: Block(g34)
    c: Parallel(g72,g34)
    c: Perpendicular(g73,g34)
    c: Coincident(g72,g73)
    c: Coincident(g74,g54)
    c: Coincident(g74,g23)
    c: Coincident(g75,g54)
    c: Coincident(g75,g32)
FEATURE [Sketcher::SketchObject] Sketch011  label="legBottomFront"
  FullyConstrained = true
  MapMode = 4
  Placement = pos=(0,0,0) rot=(0.57735,0.57735,0.57735;2.0944rad)
  sketch-geometry (13):
    g0: LineSegment StartX=-199.665 StartY=-138.314 StartZ=0 EndX=-200.721 EndY=-141.122 EndZ=0
    g1: LineSegment StartX=-200.721 StartY=-141.122 StartZ=0 EndX=-79.0409 EndY=-186.881 EndZ=0
    g2: ArcOfCircle CenterX=-71.1257 CenterY=-183.448 CenterZ=0 NormalX=0 NormalY=0 NormalZ=1 AngleXU=0 Radius=3.28025 StartAngle=3.43759 EndAngle=8.40938
    g3: LineSegment StartX=-74.4626 StartY=-174.707 StartZ=0 EndX=-76.2249 EndY=-179.393 EndZ=0
    g4: LineSegment StartX=-76.2249 StartY=-179.393 StartZ=0 EndX=-72.8553 EndY=-180.66 EndZ=0
    g5: Circle CenterX=-74.4626 CenterY=-174.707 CenterZ=0 NormalX=0 NormalY=0 NormalZ=1 AngleXU=0 Radius=1
    g6: Circle CenterX=-130.185 CenterY=-164.454 CenterZ=0 NormalX=0 NormalY=0 NormalZ=1 AngleXU=0 Radius=1
    g7: Circle CenterX=-199.665 CenterY=-138.314 CenterZ=0 NormalX=0 NormalY=0 NormalZ=1 AngleXU=0 Radius=1
    g8: BSplineCurve PolesCount=3 KnotsCount=2 Degree=2 IsPeriodic=0
    g9: GeomPoint X=-74.4626 Y=-174.707 Z=0
    g10: GeomPoint X=-199.665 Y=-138.314 Z=0
    g11: LineSegment StartX=-77.6329 StartY=-183.137 StartZ=0 EndX=-79.0409 EndY=-186.881 EndZ=0
    g12: LineSegment StartX=-77.6329 StartY=-183.137 StartZ=0 EndX=-74.2633 EndY=-184.404 EndZ=0
  constraints (24):
    c: Coincident(g1,g0)
    c: Block(g0)
    c: Perpendicular(g1,g0)
    c: Distance(g1) = 130
    c: Coincident(g4,g3)
    c: Coincident(g4,g2)
    c: Block(g2)
    c: Block(g4)
    c: Coincident(g8,g3)
    c: Weight(g5) = 1
    c: Equal(g5,g6)
    c: Equal(g5,g7)
    c: Coincident(g8,g0)
    c: InternalAlignment(g5,g8)
    c: InternalAlignment(g6,g8)
    c: InternalAlignment(g7,g8)
    c: InternalAlignment(g9,g8)
    c: InternalAlignment(g10,g8)
    c: Block(g8)
    c: Block(g3)
    c: Coincident(g11,g1)
    c: Coincident(g12,g11)
    c: Coincident(g12,g2)
    c: Block(g12)
FEATURE [Sketcher::SketchObject] Sketch
  FullyConstrained = false
  Placement = pos=(0,0,0) rot=(-1,0,0;4.71239rad)
  sketch-geometry (10):
    g0: LineSegment StartX=19.9194 StartY=-5.9387 StartZ=0 EndX=79.9194 EndY=-5.9387 EndZ=0
    g1: LineSegment StartX=19.9194 StartY=-115.939 StartZ=0 EndX=24.9194 EndY=-115.939 EndZ=0
    g2: LineSegment StartX=79.9194 StartY=-5.9387 StartZ=0 EndX=79.9194 EndY=-10.9387 EndZ=0
    g3: Circle CenterX=79.9194 CenterY=-10.9387 CenterZ=0 NormalX=0 NormalY=0 NormalZ=1 AngleXU=0 Radius=1
    g4: Circle CenterX=24.9194 CenterY=-10.9387 CenterZ=0 NormalX=0 NormalY=0 NormalZ=1 AngleXU=0 Radius=1
    g5: Circle CenterX=24.9194 CenterY=-115.939 CenterZ=0 NormalX=0 NormalY=0 NormalZ=1 AngleXU=0 Radius=1
    g6: BSplineCurve PolesCount=3 KnotsCount=2 Degree=2 IsPeriodic=0
    g7: GeomPoint X=79.9194 Y=-10.9387 Z=0
    g8: GeomPoint X=24.9194 Y=-115.939 Z=0
    g9: LineSegment StartX=19.9194 StartY=-5.9387 StartZ=0 EndX=19.9194 EndY=-115.939 EndZ=0
  constraints (20):
    c: Horizontal(g0)
    c: Distance(g0) = 60
    c: Horizontal(g1)
    c: Distance(g1) = 5
    c: Coincident(g2,g0)
    c: Vertical(g2)
    c: Distance(g2) = 5
    c: Coincident(g6,g2)
    c: Weight(g3) = 1
    c: Equal(g3,g4)
    c: Equal(g3,g5)
    c: Coincident(g6,g1)
    c: InternalAlignment(g3,g6)
    c: InternalAlignment(g4,g6)
    c: InternalAlignment(g5,g6)
    c: InternalAlignment(g7,g6)
    c: InternalAlignment(g8,g6)
    c: Coincident(g9,g0)
    c: Coincident(g9,g1)
    c: Vertical(g9)
